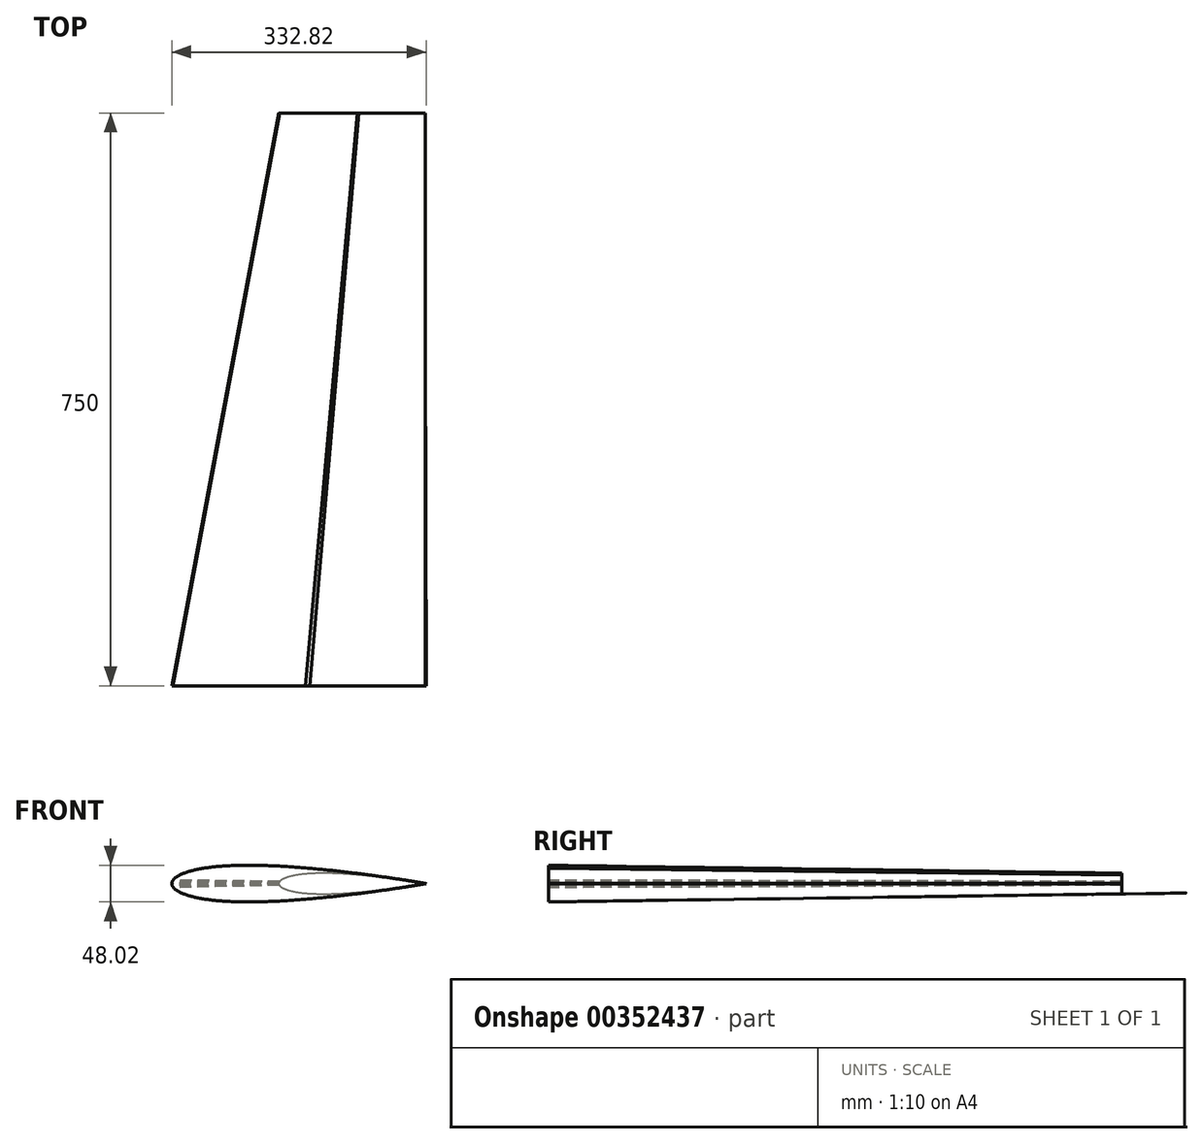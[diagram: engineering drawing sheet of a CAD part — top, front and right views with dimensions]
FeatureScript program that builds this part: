
annotation { "Feature Type Name" : "Feature", "Feature Type Description" : "" }
export const myFeature = defineFeature(function(context is Context, id is Id, definition is map)
    precondition{}
    {
        {
            var Q0;
            Q0=qCreatedBy(makeId("Front.planeOp"),FACE);
            cPlane(context, id + "F0", {"entities" : qUnion([Q0]), "cplaneType" : CPlaneType.OFFSET, "offset" : 750 * mm, "oppositeDirection" : true, "width" : 150 * mm, "height" : 150 * mm});
        }
        {
            var Q0;
            Q0=qCreatedBy(makeId("Front.planeOp"),FACE);
            var sketch = newSketch(context, id + "F1", { "sketchPlane" : qUnion([Q0])});
            skLineSegment(sketch, "E0", {"start": v(-170, 0) * mm, "end": v(170, 0) * mm, "construction": true});
            skLineSegment(sketch, "E1", {"start": v(170, 0.54) * mm, "end": v(169.98, 0.54) * mm});
            skLineSegment(sketch, "E2", {"start": v(169.98, 0.54) * mm, "end": v(169.92, 0.55) * mm});
            skLineSegment(sketch, "E3", {"start": v(169.92, 0.55) * mm, "end": v(169.8, 0.57) * mm});
            skLineSegment(sketch, "E4", {"start": v(169.8, 0.57) * mm, "end": v(169.66, 0.6) * mm});
            skLineSegment(sketch, "E5", {"start": v(169.66, 0.6) * mm, "end": v(169.47, 0.63) * mm});
            skLineSegment(sketch, "E6", {"start": v(169.47, 0.63) * mm, "end": v(169.24, 0.67) * mm});
            skLineSegment(sketch, "E7", {"start": v(169.24, 0.67) * mm, "end": v(168.96, 0.72) * mm});
            skLineSegment(sketch, "E8", {"start": v(168.96, 0.72) * mm, "end": v(168.65, 0.77) * mm});
            skLineSegment(sketch, "E9", {"start": v(168.65, 0.77) * mm, "end": v(168.29, 0.84) * mm});
            skLineSegment(sketch, "E10", {"start": v(168.29, 0.84) * mm, "end": v(167.89, 0.9) * mm});
            skLineSegment(sketch, "E11", {"start": v(167.89, 0.9) * mm, "end": v(167.44, 0.98) * mm});
            skLineSegment(sketch, "E12", {"start": v(167.44, 0.98) * mm, "end": v(166.96, 1.07) * mm});
            skLineSegment(sketch, "E13", {"start": v(166.96, 1.07) * mm, "end": v(166.43, 1.16) * mm});
            skLineSegment(sketch, "E14", {"start": v(166.43, 1.16) * mm, "end": v(165.86, 1.26) * mm});
            skLineSegment(sketch, "E15", {"start": v(165.86, 1.26) * mm, "end": v(165.26, 1.36) * mm});
            skLineSegment(sketch, "E16", {"start": v(165.26, 1.36) * mm, "end": v(164.6, 1.47) * mm});
            skLineSegment(sketch, "E17", {"start": v(164.6, 1.47) * mm, "end": v(163.91, 1.6) * mm});
            skLineSegment(sketch, "E18", {"start": v(163.91, 1.6) * mm, "end": v(163.18, 1.72) * mm});
            skLineSegment(sketch, "E19", {"start": v(163.18, 1.72) * mm, "end": v(162.4, 1.85) * mm});
            skLineSegment(sketch, "E20", {"start": v(162.4, 1.85) * mm, "end": v(161.6, 1.99) * mm});
            skLineSegment(sketch, "E21", {"start": v(161.6, 1.99) * mm, "end": v(160.74, 2.13) * mm});
            skLineSegment(sketch, "E22", {"start": v(160.74, 2.13) * mm, "end": v(159.85, 2.28) * mm});
            skLineSegment(sketch, "E23", {"start": v(159.85, 2.28) * mm, "end": v(158.92, 2.44) * mm});
            skLineSegment(sketch, "E24", {"start": v(158.92, 2.44) * mm, "end": v(157.94, 2.6) * mm});
            skLineSegment(sketch, "E25", {"start": v(157.94, 2.6) * mm, "end": v(156.93, 2.77) * mm});
            skLineSegment(sketch, "E26", {"start": v(156.93, 2.77) * mm, "end": v(155.88, 2.95) * mm});
            skLineSegment(sketch, "E27", {"start": v(155.88, 2.95) * mm, "end": v(154.79, 3.13) * mm});
            skLineSegment(sketch, "E28", {"start": v(154.79, 3.13) * mm, "end": v(153.66, 3.32) * mm});
            skLineSegment(sketch, "E29", {"start": v(153.66, 3.32) * mm, "end": v(152.5, 3.51) * mm});
            skLineSegment(sketch, "E30", {"start": v(152.5, 3.51) * mm, "end": v(151.29, 3.7) * mm});
            skLineSegment(sketch, "E31", {"start": v(151.29, 3.7) * mm, "end": v(150.05, 3.91) * mm});
            skLineSegment(sketch, "E32", {"start": v(150.05, 3.91) * mm, "end": v(148.76, 4.12) * mm});
            skLineSegment(sketch, "E33", {"start": v(148.76, 4.12) * mm, "end": v(147.45, 4.34) * mm});
            skLineSegment(sketch, "E34", {"start": v(147.45, 4.34) * mm, "end": v(146.1, 4.55) * mm});
            skLineSegment(sketch, "E35", {"start": v(146.1, 4.55) * mm, "end": v(144.7, 4.78) * mm});
            skLineSegment(sketch, "E36", {"start": v(144.7, 4.78) * mm, "end": v(143.28, 5) * mm});
            skLineSegment(sketch, "E37", {"start": v(143.28, 5) * mm, "end": v(141.81, 5.24) * mm});
            skLineSegment(sketch, "E38", {"start": v(141.81, 5.24) * mm, "end": v(140.32, 5.48) * mm});
            skLineSegment(sketch, "E39", {"start": v(140.32, 5.48) * mm, "end": v(138.78, 5.72) * mm});
            skLineSegment(sketch, "E40", {"start": v(138.78, 5.72) * mm, "end": v(137.22, 5.96) * mm});
            skLineSegment(sketch, "E41", {"start": v(137.22, 5.96) * mm, "end": v(135.62, 6.21) * mm});
            skLineSegment(sketch, "E42", {"start": v(135.62, 6.21) * mm, "end": v(133.98, 6.47) * mm});
            skLineSegment(sketch, "E43", {"start": v(133.98, 6.47) * mm, "end": v(132.31, 6.72) * mm});
            skLineSegment(sketch, "E44", {"start": v(132.31, 6.72) * mm, "end": v(130.6, 6.98) * mm});
            skLineSegment(sketch, "E45", {"start": v(130.6, 6.98) * mm, "end": v(128.88, 7.25) * mm});
            skLineSegment(sketch, "E46", {"start": v(128.88, 7.25) * mm, "end": v(127.1, 7.52) * mm});
            skLineSegment(sketch, "E47", {"start": v(127.1, 7.52) * mm, "end": v(125.31, 7.79) * mm});
            skLineSegment(sketch, "E48", {"start": v(125.31, 7.79) * mm, "end": v(123.48, 8.06) * mm});
            skLineSegment(sketch, "E49", {"start": v(123.48, 8.06) * mm, "end": v(121.62, 8.34) * mm});
            skLineSegment(sketch, "E50", {"start": v(121.62, 8.34) * mm, "end": v(119.73, 8.62) * mm});
            skLineSegment(sketch, "E51", {"start": v(119.73, 8.62) * mm, "end": v(117.81, 8.9) * mm});
            skLineSegment(sketch, "E52", {"start": v(117.81, 8.9) * mm, "end": v(115.86, 9.18) * mm});
            skLineSegment(sketch, "E53", {"start": v(115.86, 9.18) * mm, "end": v(113.89, 9.47) * mm});
            skLineSegment(sketch, "E54", {"start": v(113.89, 9.47) * mm, "end": v(111.88, 9.76) * mm});
            skLineSegment(sketch, "E55", {"start": v(111.88, 9.76) * mm, "end": v(109.84, 10.05) * mm});
            skLineSegment(sketch, "E56", {"start": v(109.84, 10.05) * mm, "end": v(107.78, 10.34) * mm});
            skLineSegment(sketch, "E57", {"start": v(107.78, 10.34) * mm, "end": v(105.7, 10.63) * mm});
            skLineSegment(sketch, "E58", {"start": v(105.7, 10.63) * mm, "end": v(103.58, 10.93) * mm});
            skLineSegment(sketch, "E59", {"start": v(103.58, 10.93) * mm, "end": v(101.44, 11.23) * mm});
            skLineSegment(sketch, "E60", {"start": v(101.44, 11.23) * mm, "end": v(99.27, 11.52) * mm});
            skLineSegment(sketch, "E61", {"start": v(99.27, 11.52) * mm, "end": v(97.08, 11.82) * mm});
            skLineSegment(sketch, "E62", {"start": v(97.08, 11.82) * mm, "end": v(94.86, 12.12) * mm});
            skLineSegment(sketch, "E63", {"start": v(94.86, 12.12) * mm, "end": v(92.63, 12.42) * mm});
            skLineSegment(sketch, "E64", {"start": v(92.63, 12.42) * mm, "end": v(90.36, 12.73) * mm});
            skLineSegment(sketch, "E65", {"start": v(90.36, 12.73) * mm, "end": v(88.08, 13.03) * mm});
            skLineSegment(sketch, "E66", {"start": v(88.08, 13.03) * mm, "end": v(85.77, 13.33) * mm});
            skLineSegment(sketch, "E67", {"start": v(85.77, 13.33) * mm, "end": v(83.45, 13.63) * mm});
            skLineSegment(sketch, "E68", {"start": v(83.45, 13.63) * mm, "end": v(81.1, 13.94) * mm});
            skLineSegment(sketch, "E69", {"start": v(81.1, 13.94) * mm, "end": v(78.73, 14.24) * mm});
            skLineSegment(sketch, "E70", {"start": v(78.73, 14.24) * mm, "end": v(76.34, 14.54) * mm});
            skLineSegment(sketch, "E71", {"start": v(76.34, 14.54) * mm, "end": v(73.93, 14.84) * mm});
            skLineSegment(sketch, "E72", {"start": v(73.93, 14.84) * mm, "end": v(71.5, 15.14) * mm});
            skLineSegment(sketch, "E73", {"start": v(71.5, 15.14) * mm, "end": v(69.06, 15.44) * mm});
            skLineSegment(sketch, "E74", {"start": v(69.06, 15.44) * mm, "end": v(66.6, 15.74) * mm});
            skLineSegment(sketch, "E75", {"start": v(66.6, 15.74) * mm, "end": v(64.13, 16.04) * mm});
            skLineSegment(sketch, "E76", {"start": v(64.13, 16.04) * mm, "end": v(61.63, 16.34) * mm});
            skLineSegment(sketch, "E77", {"start": v(61.63, 16.34) * mm, "end": v(59.12, 16.63) * mm});
            skLineSegment(sketch, "E78", {"start": v(59.12, 16.63) * mm, "end": v(56.6, 16.92) * mm});
            skLineSegment(sketch, "E79", {"start": v(56.6, 16.92) * mm, "end": v(54.06, 17.22) * mm});
            skLineSegment(sketch, "E80", {"start": v(54.06, 17.22) * mm, "end": v(51.51, 17.5) * mm});
            skLineSegment(sketch, "E81", {"start": v(51.51, 17.5) * mm, "end": v(48.95, 17.8) * mm});
            skLineSegment(sketch, "E82", {"start": v(48.95, 17.8) * mm, "end": v(46.37, 18.08) * mm});
            skLineSegment(sketch, "E83", {"start": v(46.37, 18.08) * mm, "end": v(43.78, 18.36) * mm});
            skLineSegment(sketch, "E84", {"start": v(43.78, 18.36) * mm, "end": v(41.18, 18.64) * mm});
            skLineSegment(sketch, "E85", {"start": v(41.18, 18.64) * mm, "end": v(38.58, 18.92) * mm});
            skLineSegment(sketch, "E86", {"start": v(38.58, 18.92) * mm, "end": v(35.96, 19.2) * mm});
            skLineSegment(sketch, "E87", {"start": v(35.96, 19.2) * mm, "end": v(33.33, 19.46) * mm});
            skLineSegment(sketch, "E88", {"start": v(33.33, 19.46) * mm, "end": v(30.7, 19.73) * mm});
            skLineSegment(sketch, "E89", {"start": v(30.7, 19.73) * mm, "end": v(28.05, 20) * mm});
            skLineSegment(sketch, "E90", {"start": v(28.05, 20) * mm, "end": v(25.4, 20.25) * mm});
            skLineSegment(sketch, "E91", {"start": v(25.4, 20.25) * mm, "end": v(22.74, 20.51) * mm});
            skLineSegment(sketch, "E92", {"start": v(22.74, 20.51) * mm, "end": v(20.08, 20.76) * mm});
            skLineSegment(sketch, "E93", {"start": v(20.08, 20.76) * mm, "end": v(17.41, 21) * mm});
            skLineSegment(sketch, "E94", {"start": v(17.41, 21) * mm, "end": v(14.74, 21.25) * mm});
            skLineSegment(sketch, "E95", {"start": v(14.74, 21.25) * mm, "end": v(12.07, 21.5) * mm});
            skLineSegment(sketch, "E96", {"start": v(12.07, 21.5) * mm, "end": v(9.39, 21.72) * mm});
            skLineSegment(sketch, "E97", {"start": v(9.39, 21.72) * mm, "end": v(6.7, 21.95) * mm});
            skLineSegment(sketch, "E98", {"start": v(6.7, 21.95) * mm, "end": v(4.03, 22.18) * mm});
            skLineSegment(sketch, "E99", {"start": v(4.03, 22.18) * mm, "end": v(1.34, 22.4) * mm});
            skLineSegment(sketch, "E100", {"start": v(1.34, 22.4) * mm, "end": v(-1.34, 22.6) * mm});
            skLineSegment(sketch, "E101", {"start": v(-1.34, 22.6) * mm, "end": v(-4.03, 22.81) * mm});
            skLineSegment(sketch, "E102", {"start": v(-4.03, 22.81) * mm, "end": v(-6.7, 23.01) * mm});
            skLineSegment(sketch, "E103", {"start": v(-6.7, 23.01) * mm, "end": v(-9.39, 23.2) * mm});
            skLineSegment(sketch, "E104", {"start": v(-9.39, 23.2) * mm, "end": v(-12.07, 23.4) * mm});
            skLineSegment(sketch, "E105", {"start": v(-12.07, 23.4) * mm, "end": v(-14.74, 23.57) * mm});
            skLineSegment(sketch, "E106", {"start": v(-14.74, 23.57) * mm, "end": v(-17.41, 23.74) * mm});
            skLineSegment(sketch, "E107", {"start": v(-17.41, 23.74) * mm, "end": v(-20.08, 23.91) * mm});
            skLineSegment(sketch, "E108", {"start": v(-20.08, 23.91) * mm, "end": v(-22.74, 24.07) * mm});
            skLineSegment(sketch, "E109", {"start": v(-22.74, 24.07) * mm, "end": v(-25.4, 24.22) * mm});
            skLineSegment(sketch, "E110", {"start": v(-25.4, 24.22) * mm, "end": v(-28.05, 24.37) * mm});
            skLineSegment(sketch, "E111", {"start": v(-28.05, 24.37) * mm, "end": v(-30.7, 24.5) * mm});
            skLineSegment(sketch, "E112", {"start": v(-30.7, 24.5) * mm, "end": v(-33.33, 24.63) * mm});
            skLineSegment(sketch, "E113", {"start": v(-33.33, 24.63) * mm, "end": v(-35.96, 24.75) * mm});
            skLineSegment(sketch, "E114", {"start": v(-35.96, 24.75) * mm, "end": v(-38.58, 24.86) * mm});
            skLineSegment(sketch, "E115", {"start": v(-38.58, 24.86) * mm, "end": v(-41.18, 24.97) * mm});
            skLineSegment(sketch, "E116", {"start": v(-41.18, 24.97) * mm, "end": v(-43.78, 25.06) * mm});
            skLineSegment(sketch, "E117", {"start": v(-43.78, 25.06) * mm, "end": v(-46.37, 25.15) * mm});
            skLineSegment(sketch, "E118", {"start": v(-46.37, 25.15) * mm, "end": v(-48.95, 25.23) * mm});
            skLineSegment(sketch, "E119", {"start": v(-48.95, 25.23) * mm, "end": v(-51.51, 25.3) * mm});
            skLineSegment(sketch, "E120", {"start": v(-51.51, 25.3) * mm, "end": v(-54.06, 25.35) * mm});
            skLineSegment(sketch, "E121", {"start": v(-54.06, 25.35) * mm, "end": v(-56.6, 25.4) * mm});
            skLineSegment(sketch, "E122", {"start": v(-56.6, 25.4) * mm, "end": v(-59.12, 25.44) * mm});
            skLineSegment(sketch, "E123", {"start": v(-59.12, 25.44) * mm, "end": v(-61.63, 25.47) * mm});
            skLineSegment(sketch, "E124", {"start": v(-61.63, 25.47) * mm, "end": v(-64.13, 25.5) * mm});
            skLineSegment(sketch, "E125", {"start": v(-64.13, 25.5) * mm, "end": v(-66.6, 25.5) * mm});
            skLineSegment(sketch, "E126", {"start": v(-66.6, 25.5) * mm, "end": v(-69.06, 25.5) * mm});
            skLineSegment(sketch, "E127", {"start": v(-69.06, 25.5) * mm, "end": v(-71.5, 25.5) * mm});
            skLineSegment(sketch, "E128", {"start": v(-71.5, 25.5) * mm, "end": v(-73.93, 25.48) * mm});
            skLineSegment(sketch, "E129", {"start": v(-73.93, 25.48) * mm, "end": v(-76.34, 25.45) * mm});
            skLineSegment(sketch, "E130", {"start": v(-76.34, 25.45) * mm, "end": v(-78.73, 25.4) * mm});
            skLineSegment(sketch, "E131", {"start": v(-78.73, 25.4) * mm, "end": v(-81.1, 25.36) * mm});
            skLineSegment(sketch, "E132", {"start": v(-81.1, 25.36) * mm, "end": v(-83.45, 25.3) * mm});
            skLineSegment(sketch, "E133", {"start": v(-83.45, 25.3) * mm, "end": v(-85.77, 25.23) * mm});
            skLineSegment(sketch, "E134", {"start": v(-85.77, 25.23) * mm, "end": v(-88.08, 25.14) * mm});
            skLineSegment(sketch, "E135", {"start": v(-88.08, 25.14) * mm, "end": v(-90.36, 25.05) * mm});
            skLineSegment(sketch, "E136", {"start": v(-90.36, 25.05) * mm, "end": v(-92.63, 24.95) * mm});
            skLineSegment(sketch, "E137", {"start": v(-92.63, 24.95) * mm, "end": v(-94.86, 24.83) * mm});
            skLineSegment(sketch, "E138", {"start": v(-94.86, 24.83) * mm, "end": v(-97.08, 24.7) * mm});
            skLineSegment(sketch, "E139", {"start": v(-97.08, 24.7) * mm, "end": v(-99.27, 24.57) * mm});
            skLineSegment(sketch, "E140", {"start": v(-99.27, 24.57) * mm, "end": v(-101.44, 24.42) * mm});
            skLineSegment(sketch, "E141", {"start": v(-101.44, 24.42) * mm, "end": v(-103.58, 24.27) * mm});
            skLineSegment(sketch, "E142", {"start": v(-103.58, 24.27) * mm, "end": v(-105.7, 24.1) * mm});
            skLineSegment(sketch, "E143", {"start": v(-105.7, 24.1) * mm, "end": v(-107.78, 23.92) * mm});
            skLineSegment(sketch, "E144", {"start": v(-107.78, 23.92) * mm, "end": v(-109.84, 23.73) * mm});
            skLineSegment(sketch, "E145", {"start": v(-109.84, 23.73) * mm, "end": v(-111.88, 23.53) * mm});
            skLineSegment(sketch, "E146", {"start": v(-111.88, 23.53) * mm, "end": v(-113.89, 23.32) * mm});
            skLineSegment(sketch, "E147", {"start": v(-113.89, 23.32) * mm, "end": v(-115.86, 23.1) * mm});
            skLineSegment(sketch, "E148", {"start": v(-115.86, 23.1) * mm, "end": v(-117.81, 22.87) * mm});
            skLineSegment(sketch, "E149", {"start": v(-117.81, 22.87) * mm, "end": v(-119.73, 22.62) * mm});
            skLineSegment(sketch, "E150", {"start": v(-119.73, 22.62) * mm, "end": v(-121.62, 22.37) * mm});
            skLineSegment(sketch, "E151", {"start": v(-121.62, 22.37) * mm, "end": v(-123.48, 22.1) * mm});
            skLineSegment(sketch, "E152", {"start": v(-123.48, 22.1) * mm, "end": v(-125.31, 21.83) * mm});
            skLineSegment(sketch, "E153", {"start": v(-125.31, 21.83) * mm, "end": v(-127.1, 21.55) * mm});
            skLineSegment(sketch, "E154", {"start": v(-127.1, 21.55) * mm, "end": v(-128.88, 21.26) * mm});
            skLineSegment(sketch, "E155", {"start": v(-128.88, 21.26) * mm, "end": v(-130.6, 20.95) * mm});
            skLineSegment(sketch, "E156", {"start": v(-130.6, 20.95) * mm, "end": v(-132.31, 20.64) * mm});
            skLineSegment(sketch, "E157", {"start": v(-132.31, 20.64) * mm, "end": v(-133.98, 20.32) * mm});
            skLineSegment(sketch, "E158", {"start": v(-133.98, 20.32) * mm, "end": v(-135.62, 19.98) * mm});
            skLineSegment(sketch, "E159", {"start": v(-135.62, 19.98) * mm, "end": v(-137.22, 19.64) * mm});
            skLineSegment(sketch, "E160", {"start": v(-137.22, 19.64) * mm, "end": v(-138.78, 19.29) * mm});
            skLineSegment(sketch, "E161", {"start": v(-138.78, 19.29) * mm, "end": v(-140.32, 18.93) * mm});
            skLineSegment(sketch, "E162", {"start": v(-140.32, 18.93) * mm, "end": v(-141.81, 18.56) * mm});
            skLineSegment(sketch, "E163", {"start": v(-141.81, 18.56) * mm, "end": v(-143.28, 18.18) * mm});
            skLineSegment(sketch, "E164", {"start": v(-143.28, 18.18) * mm, "end": v(-144.7, 17.8) * mm});
            skLineSegment(sketch, "E165", {"start": v(-144.7, 17.8) * mm, "end": v(-146.1, 17.4) * mm});
            skLineSegment(sketch, "E166", {"start": v(-146.1, 17.4) * mm, "end": v(-147.45, 17) * mm});
            skLineSegment(sketch, "E167", {"start": v(-147.45, 17) * mm, "end": v(-148.76, 16.58) * mm});
            skLineSegment(sketch, "E168", {"start": v(-148.76, 16.58) * mm, "end": v(-150.05, 16.16) * mm});
            skLineSegment(sketch, "E169", {"start": v(-150.05, 16.16) * mm, "end": v(-151.29, 15.73) * mm});
            skLineSegment(sketch, "E170", {"start": v(-151.29, 15.73) * mm, "end": v(-152.5, 15.3) * mm});
            skLineSegment(sketch, "E171", {"start": v(-152.5, 15.3) * mm, "end": v(-153.66, 14.85) * mm});
            skLineSegment(sketch, "E172", {"start": v(-153.66, 14.85) * mm, "end": v(-154.79, 14.4) * mm});
            skLineSegment(sketch, "E173", {"start": v(-154.79, 14.4) * mm, "end": v(-155.88, 13.95) * mm});
            skLineSegment(sketch, "E174", {"start": v(-155.88, 13.95) * mm, "end": v(-156.93, 13.48) * mm});
            skLineSegment(sketch, "E175", {"start": v(-156.93, 13.48) * mm, "end": v(-157.94, 13) * mm});
            skLineSegment(sketch, "E176", {"start": v(-157.94, 13) * mm, "end": v(-158.92, 12.53) * mm});
            skLineSegment(sketch, "E177", {"start": v(-158.92, 12.53) * mm, "end": v(-159.85, 12.04) * mm});
            skLineSegment(sketch, "E178", {"start": v(-159.85, 12.04) * mm, "end": v(-160.74, 11.55) * mm});
            skLineSegment(sketch, "E179", {"start": v(-160.74, 11.55) * mm, "end": v(-161.6, 11.05) * mm});
            skLineSegment(sketch, "E180", {"start": v(-161.6, 11.05) * mm, "end": v(-162.4, 10.55) * mm});
            skLineSegment(sketch, "E181", {"start": v(-162.4, 10.55) * mm, "end": v(-163.18, 10.04) * mm});
            skLineSegment(sketch, "E182", {"start": v(-163.18, 10.04) * mm, "end": v(-163.91, 9.53) * mm});
            skLineSegment(sketch, "E183", {"start": v(-163.91, 9.53) * mm, "end": v(-164.6, 9) * mm});
            skLineSegment(sketch, "E184", {"start": v(-164.6, 9) * mm, "end": v(-165.26, 8.48) * mm});
            skLineSegment(sketch, "E185", {"start": v(-165.26, 8.48) * mm, "end": v(-165.86, 7.95) * mm});
            skLineSegment(sketch, "E186", {"start": v(-165.86, 7.95) * mm, "end": v(-166.43, 7.4) * mm});
            skLineSegment(sketch, "E187", {"start": v(-166.43, 7.4) * mm, "end": v(-166.96, 6.87) * mm});
            skLineSegment(sketch, "E188", {"start": v(-166.96, 6.87) * mm, "end": v(-167.44, 6.32) * mm});
            skLineSegment(sketch, "E189", {"start": v(-167.44, 6.32) * mm, "end": v(-167.89, 5.77) * mm});
            skLineSegment(sketch, "E190", {"start": v(-167.89, 5.77) * mm, "end": v(-168.29, 5.2) * mm});
            skLineSegment(sketch, "E191", {"start": v(-168.29, 5.2) * mm, "end": v(-168.65, 4.65) * mm});
            skLineSegment(sketch, "E192", {"start": v(-168.65, 4.65) * mm, "end": v(-168.96, 4.08) * mm});
            skLineSegment(sketch, "E193", {"start": v(-168.96, 4.08) * mm, "end": v(-169.24, 3.51) * mm});
            skLineSegment(sketch, "E194", {"start": v(-169.24, 3.51) * mm, "end": v(-169.47, 2.94) * mm});
            skLineSegment(sketch, "E195", {"start": v(-169.47, 2.94) * mm, "end": v(-169.66, 2.36) * mm});
            skLineSegment(sketch, "E196", {"start": v(-169.66, 2.36) * mm, "end": v(-169.8, 1.77) * mm});
            skLineSegment(sketch, "E197", {"start": v(-169.8, 1.77) * mm, "end": v(-169.92, 1.19) * mm});
            skLineSegment(sketch, "E198", {"start": v(-169.92, 1.19) * mm, "end": v(-169.98, 0.6) * mm});
            skLineSegment(sketch, "E199", {"start": v(-169.98, 0.6) * mm, "end": v(-170, 0) * mm});
            skLineSegment(sketch, "E200", {"start": v(-170, 0) * mm, "end": v(-169.98, -0.6) * mm});
            skLineSegment(sketch, "E201", {"start": v(-169.98, -0.6) * mm, "end": v(-169.92, -1.19) * mm});
            skLineSegment(sketch, "E202", {"start": v(-169.92, -1.19) * mm, "end": v(-169.8, -1.77) * mm});
            skLineSegment(sketch, "E203", {"start": v(-169.8, -1.77) * mm, "end": v(-169.66, -2.36) * mm});
            skLineSegment(sketch, "E204", {"start": v(-169.66, -2.36) * mm, "end": v(-169.47, -2.94) * mm});
            skLineSegment(sketch, "E205", {"start": v(-169.47, -2.94) * mm, "end": v(-169.24, -3.51) * mm});
            skLineSegment(sketch, "E206", {"start": v(-169.24, -3.51) * mm, "end": v(-168.96, -4.08) * mm});
            skLineSegment(sketch, "E207", {"start": v(-168.96, -4.08) * mm, "end": v(-168.65, -4.65) * mm});
            skLineSegment(sketch, "E208", {"start": v(-168.65, -4.65) * mm, "end": v(-168.29, -5.2) * mm});
            skLineSegment(sketch, "E209", {"start": v(-168.29, -5.2) * mm, "end": v(-167.89, -5.77) * mm});
            skLineSegment(sketch, "E210", {"start": v(-167.89, -5.77) * mm, "end": v(-167.44, -6.32) * mm});
            skLineSegment(sketch, "E211", {"start": v(-167.44, -6.32) * mm, "end": v(-166.96, -6.87) * mm});
            skLineSegment(sketch, "E212", {"start": v(-166.96, -6.87) * mm, "end": v(-166.43, -7.4) * mm});
            skLineSegment(sketch, "E213", {"start": v(-166.43, -7.4) * mm, "end": v(-165.86, -7.95) * mm});
            skLineSegment(sketch, "E214", {"start": v(-165.86, -7.95) * mm, "end": v(-165.26, -8.48) * mm});
            skLineSegment(sketch, "E215", {"start": v(-165.26, -8.48) * mm, "end": v(-164.6, -9) * mm});
            skLineSegment(sketch, "E216", {"start": v(-164.6, -9) * mm, "end": v(-163.91, -9.53) * mm});
            skLineSegment(sketch, "E217", {"start": v(-163.91, -9.53) * mm, "end": v(-163.18, -10.04) * mm});
            skLineSegment(sketch, "E218", {"start": v(-163.18, -10.04) * mm, "end": v(-162.4, -10.55) * mm});
            skLineSegment(sketch, "E219", {"start": v(-162.4, -10.55) * mm, "end": v(-161.6, -11.05) * mm});
            skLineSegment(sketch, "E220", {"start": v(-161.6, -11.05) * mm, "end": v(-160.74, -11.55) * mm});
            skLineSegment(sketch, "E221", {"start": v(-160.74, -11.55) * mm, "end": v(-159.85, -12.04) * mm});
            skLineSegment(sketch, "E222", {"start": v(-159.85, -12.04) * mm, "end": v(-158.92, -12.53) * mm});
            skLineSegment(sketch, "E223", {"start": v(-158.92, -12.53) * mm, "end": v(-157.94, -13) * mm});
            skLineSegment(sketch, "E224", {"start": v(-157.94, -13) * mm, "end": v(-156.93, -13.48) * mm});
            skLineSegment(sketch, "E225", {"start": v(-156.93, -13.48) * mm, "end": v(-155.88, -13.95) * mm});
            skLineSegment(sketch, "E226", {"start": v(-155.88, -13.95) * mm, "end": v(-154.79, -14.4) * mm});
            skLineSegment(sketch, "E227", {"start": v(-154.79, -14.4) * mm, "end": v(-153.66, -14.85) * mm});
            skLineSegment(sketch, "E228", {"start": v(-153.66, -14.85) * mm, "end": v(-152.5, -15.3) * mm});
            skLineSegment(sketch, "E229", {"start": v(-152.5, -15.3) * mm, "end": v(-151.29, -15.73) * mm});
            skLineSegment(sketch, "E230", {"start": v(-151.29, -15.73) * mm, "end": v(-150.05, -16.16) * mm});
            skLineSegment(sketch, "E231", {"start": v(-150.05, -16.16) * mm, "end": v(-148.76, -16.58) * mm});
            skLineSegment(sketch, "E232", {"start": v(-148.76, -16.58) * mm, "end": v(-147.45, -17) * mm});
            skLineSegment(sketch, "E233", {"start": v(-147.45, -17) * mm, "end": v(-146.1, -17.4) * mm});
            skLineSegment(sketch, "E234", {"start": v(-146.1, -17.4) * mm, "end": v(-144.7, -17.8) * mm});
            skLineSegment(sketch, "E235", {"start": v(-144.7, -17.8) * mm, "end": v(-143.28, -18.18) * mm});
            skLineSegment(sketch, "E236", {"start": v(-143.28, -18.18) * mm, "end": v(-141.81, -18.56) * mm});
            skLineSegment(sketch, "E237", {"start": v(-141.81, -18.56) * mm, "end": v(-140.32, -18.93) * mm});
            skLineSegment(sketch, "E238", {"start": v(-140.32, -18.93) * mm, "end": v(-138.78, -19.29) * mm});
            skLineSegment(sketch, "E239", {"start": v(-138.78, -19.29) * mm, "end": v(-137.22, -19.64) * mm});
            skLineSegment(sketch, "E240", {"start": v(-137.22, -19.64) * mm, "end": v(-135.62, -19.98) * mm});
            skLineSegment(sketch, "E241", {"start": v(-135.62, -19.98) * mm, "end": v(-133.98, -20.32) * mm});
            skLineSegment(sketch, "E242", {"start": v(-133.98, -20.32) * mm, "end": v(-132.31, -20.64) * mm});
            skLineSegment(sketch, "E243", {"start": v(-132.31, -20.64) * mm, "end": v(-130.6, -20.95) * mm});
            skLineSegment(sketch, "E244", {"start": v(-130.6, -20.95) * mm, "end": v(-128.88, -21.26) * mm});
            skLineSegment(sketch, "E245", {"start": v(-128.88, -21.26) * mm, "end": v(-127.1, -21.55) * mm});
            skLineSegment(sketch, "E246", {"start": v(-127.1, -21.55) * mm, "end": v(-125.31, -21.83) * mm});
            skLineSegment(sketch, "E247", {"start": v(-125.31, -21.83) * mm, "end": v(-123.48, -22.1) * mm});
            skLineSegment(sketch, "E248", {"start": v(-123.48, -22.1) * mm, "end": v(-121.62, -22.37) * mm});
            skLineSegment(sketch, "E249", {"start": v(-121.62, -22.37) * mm, "end": v(-119.73, -22.62) * mm});
            skLineSegment(sketch, "E250", {"start": v(-119.73, -22.62) * mm, "end": v(-117.81, -22.87) * mm});
            skLineSegment(sketch, "E251", {"start": v(-117.81, -22.87) * mm, "end": v(-115.86, -23.1) * mm});
            skLineSegment(sketch, "E252", {"start": v(-115.86, -23.1) * mm, "end": v(-113.89, -23.32) * mm});
            skLineSegment(sketch, "E253", {"start": v(-113.89, -23.32) * mm, "end": v(-111.88, -23.53) * mm});
            skLineSegment(sketch, "E254", {"start": v(-111.88, -23.53) * mm, "end": v(-109.84, -23.73) * mm});
            skLineSegment(sketch, "E255", {"start": v(-109.84, -23.73) * mm, "end": v(-107.78, -23.92) * mm});
            skLineSegment(sketch, "E256", {"start": v(-107.78, -23.92) * mm, "end": v(-105.7, -24.1) * mm});
            skLineSegment(sketch, "E257", {"start": v(-105.7, -24.1) * mm, "end": v(-103.58, -24.27) * mm});
            skLineSegment(sketch, "E258", {"start": v(-103.58, -24.27) * mm, "end": v(-101.44, -24.42) * mm});
            skLineSegment(sketch, "E259", {"start": v(-101.44, -24.42) * mm, "end": v(-99.27, -24.57) * mm});
            skLineSegment(sketch, "E260", {"start": v(-99.27, -24.57) * mm, "end": v(-97.08, -24.7) * mm});
            skLineSegment(sketch, "E261", {"start": v(-97.08, -24.7) * mm, "end": v(-94.86, -24.83) * mm});
            skLineSegment(sketch, "E262", {"start": v(-94.86, -24.83) * mm, "end": v(-92.63, -24.95) * mm});
            skLineSegment(sketch, "E263", {"start": v(-92.63, -24.95) * mm, "end": v(-90.36, -25.05) * mm});
            skLineSegment(sketch, "E264", {"start": v(-90.36, -25.05) * mm, "end": v(-88.08, -25.14) * mm});
            skLineSegment(sketch, "E265", {"start": v(-88.08, -25.14) * mm, "end": v(-85.77, -25.23) * mm});
            skLineSegment(sketch, "E266", {"start": v(-85.77, -25.23) * mm, "end": v(-83.45, -25.3) * mm});
            skLineSegment(sketch, "E267", {"start": v(-83.45, -25.3) * mm, "end": v(-81.1, -25.36) * mm});
            skLineSegment(sketch, "E268", {"start": v(-81.1, -25.36) * mm, "end": v(-78.73, -25.4) * mm});
            skLineSegment(sketch, "E269", {"start": v(-78.73, -25.4) * mm, "end": v(-76.34, -25.45) * mm});
            skLineSegment(sketch, "E270", {"start": v(-76.34, -25.45) * mm, "end": v(-73.93, -25.48) * mm});
            skLineSegment(sketch, "E271", {"start": v(-73.93, -25.48) * mm, "end": v(-71.5, -25.5) * mm});
            skLineSegment(sketch, "E272", {"start": v(-71.5, -25.5) * mm, "end": v(-69.06, -25.5) * mm});
            skLineSegment(sketch, "E273", {"start": v(-69.06, -25.5) * mm, "end": v(-66.6, -25.5) * mm});
            skLineSegment(sketch, "E274", {"start": v(-66.6, -25.5) * mm, "end": v(-64.13, -25.5) * mm});
            skLineSegment(sketch, "E275", {"start": v(-64.13, -25.5) * mm, "end": v(-61.63, -25.47) * mm});
            skLineSegment(sketch, "E276", {"start": v(-61.63, -25.47) * mm, "end": v(-59.12, -25.44) * mm});
            skLineSegment(sketch, "E277", {"start": v(-59.12, -25.44) * mm, "end": v(-56.6, -25.4) * mm});
            skLineSegment(sketch, "E278", {"start": v(-56.6, -25.4) * mm, "end": v(-54.06, -25.35) * mm});
            skLineSegment(sketch, "E279", {"start": v(-54.06, -25.35) * mm, "end": v(-51.51, -25.3) * mm});
            skLineSegment(sketch, "E280", {"start": v(-51.51, -25.3) * mm, "end": v(-48.95, -25.23) * mm});
            skLineSegment(sketch, "E281", {"start": v(-48.95, -25.23) * mm, "end": v(-46.37, -25.15) * mm});
            skLineSegment(sketch, "E282", {"start": v(-46.37, -25.15) * mm, "end": v(-43.78, -25.06) * mm});
            skLineSegment(sketch, "E283", {"start": v(-43.78, -25.06) * mm, "end": v(-41.18, -24.97) * mm});
            skLineSegment(sketch, "E284", {"start": v(-41.18, -24.97) * mm, "end": v(-38.58, -24.86) * mm});
            skLineSegment(sketch, "E285", {"start": v(-38.58, -24.86) * mm, "end": v(-35.96, -24.75) * mm});
            skLineSegment(sketch, "E286", {"start": v(-35.96, -24.75) * mm, "end": v(-33.33, -24.63) * mm});
            skLineSegment(sketch, "E287", {"start": v(-33.33, -24.63) * mm, "end": v(-30.7, -24.5) * mm});
            skLineSegment(sketch, "E288", {"start": v(-30.7, -24.5) * mm, "end": v(-28.05, -24.37) * mm});
            skLineSegment(sketch, "E289", {"start": v(-28.05, -24.37) * mm, "end": v(-25.4, -24.22) * mm});
            skLineSegment(sketch, "E290", {"start": v(-25.4, -24.22) * mm, "end": v(-22.74, -24.07) * mm});
            skLineSegment(sketch, "E291", {"start": v(-22.74, -24.07) * mm, "end": v(-20.08, -23.91) * mm});
            skLineSegment(sketch, "E292", {"start": v(-20.08, -23.91) * mm, "end": v(-17.41, -23.74) * mm});
            skLineSegment(sketch, "E293", {"start": v(-17.41, -23.74) * mm, "end": v(-14.74, -23.57) * mm});
            skLineSegment(sketch, "E294", {"start": v(-14.74, -23.57) * mm, "end": v(-12.07, -23.4) * mm});
            skLineSegment(sketch, "E295", {"start": v(-12.07, -23.4) * mm, "end": v(-9.39, -23.2) * mm});
            skLineSegment(sketch, "E296", {"start": v(-9.39, -23.2) * mm, "end": v(-6.7, -23.01) * mm});
            skLineSegment(sketch, "E297", {"start": v(-6.7, -23.01) * mm, "end": v(-4.03, -22.81) * mm});
            skLineSegment(sketch, "E298", {"start": v(-4.03, -22.81) * mm, "end": v(-1.34, -22.6) * mm});
            skLineSegment(sketch, "E299", {"start": v(-1.34, -22.6) * mm, "end": v(1.34, -22.4) * mm});
            skLineSegment(sketch, "E300", {"start": v(1.34, -22.4) * mm, "end": v(4.03, -22.18) * mm});
            skLineSegment(sketch, "E301", {"start": v(4.03, -22.18) * mm, "end": v(6.7, -21.95) * mm});
            skLineSegment(sketch, "E302", {"start": v(6.7, -21.95) * mm, "end": v(9.39, -21.72) * mm});
            skLineSegment(sketch, "E303", {"start": v(9.39, -21.72) * mm, "end": v(12.07, -21.5) * mm});
            skLineSegment(sketch, "E304", {"start": v(12.07, -21.5) * mm, "end": v(14.74, -21.25) * mm});
            skLineSegment(sketch, "E305", {"start": v(14.74, -21.25) * mm, "end": v(17.41, -21) * mm});
            skLineSegment(sketch, "E306", {"start": v(17.41, -21) * mm, "end": v(20.08, -20.76) * mm});
            skLineSegment(sketch, "E307", {"start": v(20.08, -20.76) * mm, "end": v(22.74, -20.51) * mm});
            skLineSegment(sketch, "E308", {"start": v(22.74, -20.51) * mm, "end": v(25.4, -20.25) * mm});
            skLineSegment(sketch, "E309", {"start": v(25.4, -20.25) * mm, "end": v(28.05, -20) * mm});
            skLineSegment(sketch, "E310", {"start": v(28.05, -20) * mm, "end": v(30.7, -19.73) * mm});
            skLineSegment(sketch, "E311", {"start": v(30.7, -19.73) * mm, "end": v(33.33, -19.46) * mm});
            skLineSegment(sketch, "E312", {"start": v(33.33, -19.46) * mm, "end": v(35.96, -19.2) * mm});
            skLineSegment(sketch, "E313", {"start": v(35.96, -19.2) * mm, "end": v(38.58, -18.92) * mm});
            skLineSegment(sketch, "E314", {"start": v(38.58, -18.92) * mm, "end": v(41.18, -18.64) * mm});
            skLineSegment(sketch, "E315", {"start": v(41.18, -18.64) * mm, "end": v(43.78, -18.36) * mm});
            skLineSegment(sketch, "E316", {"start": v(43.78, -18.36) * mm, "end": v(46.37, -18.08) * mm});
            skLineSegment(sketch, "E317", {"start": v(46.37, -18.08) * mm, "end": v(48.95, -17.8) * mm});
            skLineSegment(sketch, "E318", {"start": v(48.95, -17.8) * mm, "end": v(51.51, -17.5) * mm});
            skLineSegment(sketch, "E319", {"start": v(51.51, -17.5) * mm, "end": v(54.06, -17.22) * mm});
            skLineSegment(sketch, "E320", {"start": v(54.06, -17.22) * mm, "end": v(56.6, -16.92) * mm});
            skLineSegment(sketch, "E321", {"start": v(56.6, -16.92) * mm, "end": v(59.12, -16.63) * mm});
            skLineSegment(sketch, "E322", {"start": v(59.12, -16.63) * mm, "end": v(61.63, -16.34) * mm});
            skLineSegment(sketch, "E323", {"start": v(61.63, -16.34) * mm, "end": v(64.13, -16.04) * mm});
            skLineSegment(sketch, "E324", {"start": v(64.13, -16.04) * mm, "end": v(66.6, -15.74) * mm});
            skLineSegment(sketch, "E325", {"start": v(66.6, -15.74) * mm, "end": v(69.06, -15.44) * mm});
            skLineSegment(sketch, "E326", {"start": v(69.06, -15.44) * mm, "end": v(71.5, -15.14) * mm});
            skLineSegment(sketch, "E327", {"start": v(71.5, -15.14) * mm, "end": v(73.93, -14.84) * mm});
            skLineSegment(sketch, "E328", {"start": v(73.93, -14.84) * mm, "end": v(76.34, -14.54) * mm});
            skLineSegment(sketch, "E329", {"start": v(76.34, -14.54) * mm, "end": v(78.73, -14.24) * mm});
            skLineSegment(sketch, "E330", {"start": v(78.73, -14.24) * mm, "end": v(81.1, -13.94) * mm});
            skLineSegment(sketch, "E331", {"start": v(81.1, -13.94) * mm, "end": v(83.45, -13.63) * mm});
            skLineSegment(sketch, "E332", {"start": v(83.45, -13.63) * mm, "end": v(85.77, -13.33) * mm});
            skLineSegment(sketch, "E333", {"start": v(85.77, -13.33) * mm, "end": v(88.08, -13.03) * mm});
            skLineSegment(sketch, "E334", {"start": v(88.08, -13.03) * mm, "end": v(90.36, -12.73) * mm});
            skLineSegment(sketch, "E335", {"start": v(90.36, -12.73) * mm, "end": v(92.63, -12.42) * mm});
            skLineSegment(sketch, "E336", {"start": v(92.63, -12.42) * mm, "end": v(94.86, -12.12) * mm});
            skLineSegment(sketch, "E337", {"start": v(94.86, -12.12) * mm, "end": v(97.08, -11.82) * mm});
            skLineSegment(sketch, "E338", {"start": v(97.08, -11.82) * mm, "end": v(99.27, -11.52) * mm});
            skLineSegment(sketch, "E339", {"start": v(99.27, -11.52) * mm, "end": v(101.44, -11.23) * mm});
            skLineSegment(sketch, "E340", {"start": v(101.44, -11.23) * mm, "end": v(103.58, -10.93) * mm});
            skLineSegment(sketch, "E341", {"start": v(103.58, -10.93) * mm, "end": v(105.7, -10.63) * mm});
            skLineSegment(sketch, "E342", {"start": v(105.7, -10.63) * mm, "end": v(107.78, -10.34) * mm});
            skLineSegment(sketch, "E343", {"start": v(107.78, -10.34) * mm, "end": v(109.84, -10.05) * mm});
            skLineSegment(sketch, "E344", {"start": v(109.84, -10.05) * mm, "end": v(111.88, -9.76) * mm});
            skLineSegment(sketch, "E345", {"start": v(111.88, -9.76) * mm, "end": v(113.89, -9.47) * mm});
            skLineSegment(sketch, "E346", {"start": v(113.89, -9.47) * mm, "end": v(115.86, -9.18) * mm});
            skLineSegment(sketch, "E347", {"start": v(115.86, -9.18) * mm, "end": v(117.81, -8.9) * mm});
            skLineSegment(sketch, "E348", {"start": v(117.81, -8.9) * mm, "end": v(119.73, -8.62) * mm});
            skLineSegment(sketch, "E349", {"start": v(119.73, -8.62) * mm, "end": v(121.62, -8.34) * mm});
            skLineSegment(sketch, "E350", {"start": v(121.62, -8.34) * mm, "end": v(123.48, -8.06) * mm});
            skLineSegment(sketch, "E351", {"start": v(123.48, -8.06) * mm, "end": v(125.31, -7.79) * mm});
            skLineSegment(sketch, "E352", {"start": v(125.31, -7.79) * mm, "end": v(127.1, -7.52) * mm});
            skLineSegment(sketch, "E353", {"start": v(127.1, -7.52) * mm, "end": v(128.88, -7.25) * mm});
            skLineSegment(sketch, "E354", {"start": v(128.88, -7.25) * mm, "end": v(130.6, -6.98) * mm});
            skLineSegment(sketch, "E355", {"start": v(130.6, -6.98) * mm, "end": v(132.31, -6.72) * mm});
            skLineSegment(sketch, "E356", {"start": v(132.31, -6.72) * mm, "end": v(133.98, -6.47) * mm});
            skLineSegment(sketch, "E357", {"start": v(133.98, -6.47) * mm, "end": v(135.62, -6.21) * mm});
            skLineSegment(sketch, "E358", {"start": v(135.62, -6.21) * mm, "end": v(137.22, -5.96) * mm});
            skLineSegment(sketch, "E359", {"start": v(137.22, -5.96) * mm, "end": v(138.78, -5.72) * mm});
            skLineSegment(sketch, "E360", {"start": v(138.78, -5.72) * mm, "end": v(140.32, -5.48) * mm});
            skLineSegment(sketch, "E361", {"start": v(140.32, -5.48) * mm, "end": v(141.81, -5.24) * mm});
            skLineSegment(sketch, "E362", {"start": v(141.81, -5.24) * mm, "end": v(143.28, -5) * mm});
            skLineSegment(sketch, "E363", {"start": v(143.28, -5) * mm, "end": v(144.7, -4.78) * mm});
            skLineSegment(sketch, "E364", {"start": v(144.7, -4.78) * mm, "end": v(146.1, -4.55) * mm});
            skLineSegment(sketch, "E365", {"start": v(146.1, -4.55) * mm, "end": v(147.45, -4.34) * mm});
            skLineSegment(sketch, "E366", {"start": v(147.45, -4.34) * mm, "end": v(148.76, -4.12) * mm});
            skLineSegment(sketch, "E367", {"start": v(148.76, -4.12) * mm, "end": v(150.05, -3.91) * mm});
            skLineSegment(sketch, "E368", {"start": v(150.05, -3.91) * mm, "end": v(151.29, -3.7) * mm});
            skLineSegment(sketch, "E369", {"start": v(151.29, -3.7) * mm, "end": v(152.5, -3.51) * mm});
            skLineSegment(sketch, "E370", {"start": v(152.5, -3.51) * mm, "end": v(153.66, -3.32) * mm});
            skLineSegment(sketch, "E371", {"start": v(153.66, -3.32) * mm, "end": v(154.79, -3.13) * mm});
            skLineSegment(sketch, "E372", {"start": v(154.79, -3.13) * mm, "end": v(155.88, -2.95) * mm});
            skLineSegment(sketch, "E373", {"start": v(155.88, -2.95) * mm, "end": v(156.93, -2.77) * mm});
            skLineSegment(sketch, "E374", {"start": v(156.93, -2.77) * mm, "end": v(157.94, -2.6) * mm});
            skLineSegment(sketch, "E375", {"start": v(157.94, -2.6) * mm, "end": v(158.92, -2.44) * mm});
            skLineSegment(sketch, "E376", {"start": v(158.92, -2.44) * mm, "end": v(159.85, -2.28) * mm});
            skLineSegment(sketch, "E377", {"start": v(159.85, -2.28) * mm, "end": v(160.74, -2.13) * mm});
            skLineSegment(sketch, "E378", {"start": v(160.74, -2.13) * mm, "end": v(161.6, -1.99) * mm});
            skLineSegment(sketch, "E379", {"start": v(161.6, -1.99) * mm, "end": v(162.4, -1.85) * mm});
            skLineSegment(sketch, "E380", {"start": v(162.4, -1.85) * mm, "end": v(163.18, -1.72) * mm});
            skLineSegment(sketch, "E381", {"start": v(163.18, -1.72) * mm, "end": v(163.91, -1.6) * mm});
            skLineSegment(sketch, "E382", {"start": v(163.91, -1.6) * mm, "end": v(164.6, -1.47) * mm});
            skLineSegment(sketch, "E383", {"start": v(164.6, -1.47) * mm, "end": v(165.26, -1.36) * mm});
            skLineSegment(sketch, "E384", {"start": v(165.26, -1.36) * mm, "end": v(165.86, -1.26) * mm});
            skLineSegment(sketch, "E385", {"start": v(165.86, -1.26) * mm, "end": v(166.43, -1.16) * mm});
            skLineSegment(sketch, "E386", {"start": v(166.43, -1.16) * mm, "end": v(166.96, -1.07) * mm});
            skLineSegment(sketch, "E387", {"start": v(166.96, -1.07) * mm, "end": v(167.44, -0.98) * mm});
            skLineSegment(sketch, "E388", {"start": v(167.44, -0.98) * mm, "end": v(167.89, -0.9) * mm});
            skLineSegment(sketch, "E389", {"start": v(167.89, -0.9) * mm, "end": v(168.29, -0.84) * mm});
            skLineSegment(sketch, "E390", {"start": v(168.29, -0.84) * mm, "end": v(168.65, -0.77) * mm});
            skLineSegment(sketch, "E391", {"start": v(168.65, -0.77) * mm, "end": v(168.96, -0.72) * mm});
            skLineSegment(sketch, "E392", {"start": v(168.96, -0.72) * mm, "end": v(169.24, -0.67) * mm});
            skLineSegment(sketch, "E393", {"start": v(169.24, -0.67) * mm, "end": v(169.47, -0.63) * mm});
            skLineSegment(sketch, "E394", {"start": v(169.47, -0.63) * mm, "end": v(169.66, -0.6) * mm});
            skLineSegment(sketch, "E395", {"start": v(169.66, -0.6) * mm, "end": v(169.8, -0.57) * mm});
            skLineSegment(sketch, "E396", {"start": v(169.8, -0.57) * mm, "end": v(169.92, -0.55) * mm});
            skLineSegment(sketch, "E397", {"start": v(169.92, -0.55) * mm, "end": v(169.98, -0.54) * mm});
            skLineSegment(sketch, "E398", {"start": v(169.98, -0.54) * mm, "end": v(170, -0.54) * mm});
            skLineSegment(sketch, "E399", {"start": v(170, -0.54) * mm, "end": v(170, 0.54) * mm});
            skLineSegment(sketch, "E400", {"start": v(164.32, 0) * mm, "end": v(163.66, 0.11) * mm});
            skLineSegment(sketch, "E401", {"start": v(163.66, 0.11) * mm, "end": v(162.93, 0.24) * mm});
            skLineSegment(sketch, "E402", {"start": v(162.93, 0.24) * mm, "end": v(162.16, 0.37) * mm});
            skLineSegment(sketch, "E403", {"start": v(162.16, 0.37) * mm, "end": v(161.34, 0.5) * mm});
            skLineSegment(sketch, "E404", {"start": v(161.34, 0.5) * mm, "end": v(160.5, 0.65) * mm});
            skLineSegment(sketch, "E405", {"start": v(160.5, 0.65) * mm, "end": v(159.6, 0.8) * mm});
            skLineSegment(sketch, "E406", {"start": v(159.6, 0.8) * mm, "end": v(158.67, 0.96) * mm});
            skLineSegment(sketch, "E407", {"start": v(158.67, 0.96) * mm, "end": v(157.7, 1.13) * mm});
            skLineSegment(sketch, "E408", {"start": v(157.7, 1.13) * mm, "end": v(156.68, 1.3) * mm});
            skLineSegment(sketch, "E409", {"start": v(156.68, 1.3) * mm, "end": v(155.63, 1.47) * mm});
            skLineSegment(sketch, "E410", {"start": v(155.63, 1.47) * mm, "end": v(154.54, 1.65) * mm});
            skLineSegment(sketch, "E411", {"start": v(154.54, 1.65) * mm, "end": v(153.42, 1.84) * mm});
            skLineSegment(sketch, "E412", {"start": v(153.42, 1.84) * mm, "end": v(152.25, 2.03) * mm});
            skLineSegment(sketch, "E413", {"start": v(152.25, 2.03) * mm, "end": v(151.04, 2.23) * mm});
            skLineSegment(sketch, "E414", {"start": v(151.04, 2.23) * mm, "end": v(149.8, 2.43) * mm});
            skLineSegment(sketch, "E415", {"start": v(149.8, 2.43) * mm, "end": v(148.52, 2.64) * mm});
            skLineSegment(sketch, "E416", {"start": v(148.52, 2.64) * mm, "end": v(147.2, 2.85) * mm});
            skLineSegment(sketch, "E417", {"start": v(147.2, 2.85) * mm, "end": v(145.85, 3.07) * mm});
            skLineSegment(sketch, "E418", {"start": v(145.85, 3.07) * mm, "end": v(144.47, 3.3) * mm});
            skLineSegment(sketch, "E419", {"start": v(144.47, 3.3) * mm, "end": v(143.04, 3.52) * mm});
            skLineSegment(sketch, "E420", {"start": v(143.04, 3.52) * mm, "end": v(141.58, 3.76) * mm});
            skLineSegment(sketch, "E421", {"start": v(141.58, 3.76) * mm, "end": v(140.08, 4) * mm});
            skLineSegment(sketch, "E422", {"start": v(140.08, 4) * mm, "end": v(138.55, 4.24) * mm});
            skLineSegment(sketch, "E423", {"start": v(138.55, 4.24) * mm, "end": v(136.99, 4.48) * mm});
            skLineSegment(sketch, "E424", {"start": v(136.99, 4.48) * mm, "end": v(135.39, 4.73) * mm});
            skLineSegment(sketch, "E425", {"start": v(135.39, 4.73) * mm, "end": v(133.75, 4.98) * mm});
            skLineSegment(sketch, "E426", {"start": v(133.75, 4.98) * mm, "end": v(132.08, 5.24) * mm});
            skLineSegment(sketch, "E427", {"start": v(132.08, 5.24) * mm, "end": v(130.38, 5.5) * mm});
            skLineSegment(sketch, "E428", {"start": v(130.38, 5.5) * mm, "end": v(128.65, 5.77) * mm});
            skLineSegment(sketch, "E429", {"start": v(128.65, 5.77) * mm, "end": v(126.89, 6.03) * mm});
            skLineSegment(sketch, "E430", {"start": v(126.89, 6.03) * mm, "end": v(125.09, 6.3) * mm});
            skLineSegment(sketch, "E431", {"start": v(125.09, 6.3) * mm, "end": v(123.26, 6.58) * mm});
            skLineSegment(sketch, "E432", {"start": v(123.26, 6.58) * mm, "end": v(121.4, 6.85) * mm});
            skLineSegment(sketch, "E433", {"start": v(121.4, 6.85) * mm, "end": v(119.51, 7.13) * mm});
            skLineSegment(sketch, "E434", {"start": v(119.51, 7.13) * mm, "end": v(117.6, 7.41) * mm});
            skLineSegment(sketch, "E435", {"start": v(117.6, 7.41) * mm, "end": v(115.65, 7.7) * mm});
            skLineSegment(sketch, "E436", {"start": v(115.65, 7.7) * mm, "end": v(113.67, 7.98) * mm});
            skLineSegment(sketch, "E437", {"start": v(113.67, 7.98) * mm, "end": v(111.67, 8.27) * mm});
            skLineSegment(sketch, "E438", {"start": v(111.67, 8.27) * mm, "end": v(109.63, 8.56) * mm});
            skLineSegment(sketch, "E439", {"start": v(109.63, 8.56) * mm, "end": v(107.57, 8.85) * mm});
            skLineSegment(sketch, "E440", {"start": v(107.57, 8.85) * mm, "end": v(105.48, 9.15) * mm});
            skLineSegment(sketch, "E441", {"start": v(105.48, 9.15) * mm, "end": v(103.37, 9.44) * mm});
            skLineSegment(sketch, "E442", {"start": v(103.37, 9.44) * mm, "end": v(101.23, 9.74) * mm});
            skLineSegment(sketch, "E443", {"start": v(101.23, 9.74) * mm, "end": v(99.07, 10.04) * mm});
            skLineSegment(sketch, "E444", {"start": v(99.07, 10.04) * mm, "end": v(96.88, 10.34) * mm});
            skLineSegment(sketch, "E445", {"start": v(96.88, 10.34) * mm, "end": v(94.66, 10.64) * mm});
            skLineSegment(sketch, "E446", {"start": v(94.66, 10.64) * mm, "end": v(92.43, 10.94) * mm});
            skLineSegment(sketch, "E447", {"start": v(92.43, 10.94) * mm, "end": v(90.17, 11.24) * mm});
            skLineSegment(sketch, "E448", {"start": v(90.17, 11.24) * mm, "end": v(87.88, 11.54) * mm});
            skLineSegment(sketch, "E449", {"start": v(87.88, 11.54) * mm, "end": v(85.58, 11.84) * mm});
            skLineSegment(sketch, "E450", {"start": v(85.58, 11.84) * mm, "end": v(83.25, 12.15) * mm});
            skLineSegment(sketch, "E451", {"start": v(83.25, 12.15) * mm, "end": v(80.9, 12.45) * mm});
            skLineSegment(sketch, "E452", {"start": v(80.9, 12.45) * mm, "end": v(78.54, 12.75) * mm});
            skLineSegment(sketch, "E453", {"start": v(78.54, 12.75) * mm, "end": v(76.15, 13.05) * mm});
            skLineSegment(sketch, "E454", {"start": v(76.15, 13.05) * mm, "end": v(73.75, 13.35) * mm});
            skLineSegment(sketch, "E455", {"start": v(73.75, 13.35) * mm, "end": v(71.32, 13.65) * mm});
            skLineSegment(sketch, "E456", {"start": v(71.32, 13.65) * mm, "end": v(68.88, 13.95) * mm});
            skLineSegment(sketch, "E457", {"start": v(68.88, 13.95) * mm, "end": v(66.42, 14.25) * mm});
            skLineSegment(sketch, "E458", {"start": v(66.42, 14.25) * mm, "end": v(63.95, 14.55) * mm});
            skLineSegment(sketch, "E459", {"start": v(63.95, 14.55) * mm, "end": v(61.46, 14.85) * mm});
            skLineSegment(sketch, "E460", {"start": v(61.46, 14.85) * mm, "end": v(58.95, 15.14) * mm});
            skLineSegment(sketch, "E461", {"start": v(58.95, 15.14) * mm, "end": v(56.43, 15.43) * mm});
            skLineSegment(sketch, "E462", {"start": v(56.43, 15.43) * mm, "end": v(53.9, 15.73) * mm});
            skLineSegment(sketch, "E463", {"start": v(53.9, 15.73) * mm, "end": v(51.34, 16.02) * mm});
            skLineSegment(sketch, "E464", {"start": v(51.34, 16.02) * mm, "end": v(48.78, 16.3) * mm});
            skLineSegment(sketch, "E465", {"start": v(48.78, 16.3) * mm, "end": v(46.2, 16.59) * mm});
            skLineSegment(sketch, "E466", {"start": v(46.2, 16.59) * mm, "end": v(43.62, 16.87) * mm});
            skLineSegment(sketch, "E467", {"start": v(43.62, 16.87) * mm, "end": v(41.03, 17.15) * mm});
            skLineSegment(sketch, "E468", {"start": v(41.03, 17.15) * mm, "end": v(38.42, 17.43) * mm});
            skLineSegment(sketch, "E469", {"start": v(38.42, 17.43) * mm, "end": v(35.8, 17.7) * mm});
            skLineSegment(sketch, "E470", {"start": v(35.8, 17.7) * mm, "end": v(33.18, 17.97) * mm});
            skLineSegment(sketch, "E471", {"start": v(33.18, 17.97) * mm, "end": v(30.54, 18.24) * mm});
            skLineSegment(sketch, "E472", {"start": v(30.54, 18.24) * mm, "end": v(27.9, 18.5) * mm});
            skLineSegment(sketch, "E473", {"start": v(27.9, 18.5) * mm, "end": v(25.26, 18.76) * mm});
            skLineSegment(sketch, "E474", {"start": v(25.26, 18.76) * mm, "end": v(22.6, 19.02) * mm});
            skLineSegment(sketch, "E475", {"start": v(22.6, 19.02) * mm, "end": v(19.94, 19.27) * mm});
            skLineSegment(sketch, "E476", {"start": v(19.94, 19.27) * mm, "end": v(17.28, 19.52) * mm});
            skLineSegment(sketch, "E477", {"start": v(17.28, 19.52) * mm, "end": v(14.6, 19.76) * mm});
            skLineSegment(sketch, "E478", {"start": v(14.6, 19.76) * mm, "end": v(11.94, 20) * mm});
            skLineSegment(sketch, "E479", {"start": v(11.94, 20) * mm, "end": v(9.26, 20.23) * mm});
            skLineSegment(sketch, "E480", {"start": v(9.26, 20.23) * mm, "end": v(6.58, 20.46) * mm});
            skLineSegment(sketch, "E481", {"start": v(6.58, 20.46) * mm, "end": v(3.9, 20.68) * mm});
            skLineSegment(sketch, "E482", {"start": v(3.9, 20.68) * mm, "end": v(1.22, 20.9) * mm});
            skLineSegment(sketch, "E483", {"start": v(1.22, 20.9) * mm, "end": v(-1.46, 21.1) * mm});
            skLineSegment(sketch, "E484", {"start": v(-1.46, 21.1) * mm, "end": v(-4.14, 21.31) * mm});
            skLineSegment(sketch, "E485", {"start": v(-4.14, 21.31) * mm, "end": v(-6.82, 21.51) * mm});
            skLineSegment(sketch, "E486", {"start": v(-6.82, 21.51) * mm, "end": v(-9.5, 21.7) * mm});
            skLineSegment(sketch, "E487", {"start": v(-9.5, 21.7) * mm, "end": v(-12.17, 21.9) * mm});
            skLineSegment(sketch, "E488", {"start": v(-12.17, 21.9) * mm, "end": v(-14.84, 22.07) * mm});
            skLineSegment(sketch, "E489", {"start": v(-14.84, 22.07) * mm, "end": v(-17.5, 22.25) * mm});
            skLineSegment(sketch, "E490", {"start": v(-17.5, 22.25) * mm, "end": v(-20.17, 22.41) * mm});
            skLineSegment(sketch, "E491", {"start": v(-20.17, 22.41) * mm, "end": v(-22.83, 22.57) * mm});
            skLineSegment(sketch, "E492", {"start": v(-22.83, 22.57) * mm, "end": v(-25.48, 22.72) * mm});
            skLineSegment(sketch, "E493", {"start": v(-25.48, 22.72) * mm, "end": v(-28.13, 22.87) * mm});
            skLineSegment(sketch, "E494", {"start": v(-28.13, 22.87) * mm, "end": v(-30.77, 23) * mm});
            skLineSegment(sketch, "E495", {"start": v(-30.77, 23) * mm, "end": v(-33.4, 23.13) * mm});
            skLineSegment(sketch, "E496", {"start": v(-33.4, 23.13) * mm, "end": v(-36.02, 23.25) * mm});
            skLineSegment(sketch, "E497", {"start": v(-36.02, 23.25) * mm, "end": v(-38.64, 23.37) * mm});
            skLineSegment(sketch, "E498", {"start": v(-38.64, 23.37) * mm, "end": v(-41.24, 23.47) * mm});
            skLineSegment(sketch, "E499", {"start": v(-41.24, 23.47) * mm, "end": v(-43.84, 23.56) * mm});
            skLineSegment(sketch, "E500", {"start": v(-43.84, 23.56) * mm, "end": v(-46.42, 23.65) * mm});
            skLineSegment(sketch, "E501", {"start": v(-46.42, 23.65) * mm, "end": v(-48.99, 23.73) * mm});
            skLineSegment(sketch, "E502", {"start": v(-48.99, 23.73) * mm, "end": v(-51.55, 23.8) * mm});
            skLineSegment(sketch, "E503", {"start": v(-51.55, 23.8) * mm, "end": v(-54.1, 23.85) * mm});
            skLineSegment(sketch, "E504", {"start": v(-54.1, 23.85) * mm, "end": v(-56.63, 23.9) * mm});
            skLineSegment(sketch, "E505", {"start": v(-56.63, 23.9) * mm, "end": v(-59.14, 23.94) * mm});
            skLineSegment(sketch, "E506", {"start": v(-59.14, 23.94) * mm, "end": v(-61.65, 23.97) * mm});
            skLineSegment(sketch, "E507", {"start": v(-61.65, 23.97) * mm, "end": v(-64.13, 24) * mm});
            skLineSegment(sketch, "E508", {"start": v(-64.13, 24) * mm, "end": v(-66.6, 24) * mm});
            skLineSegment(sketch, "E509", {"start": v(-66.6, 24) * mm, "end": v(-69.06, 24) * mm});
            skLineSegment(sketch, "E510", {"start": v(-69.06, 24) * mm, "end": v(-71.5, 24) * mm});
            skLineSegment(sketch, "E511", {"start": v(-71.5, 24) * mm, "end": v(-73.92, 23.98) * mm});
            skLineSegment(sketch, "E512", {"start": v(-73.92, 23.98) * mm, "end": v(-76.32, 23.95) * mm});
            skLineSegment(sketch, "E513", {"start": v(-76.32, 23.95) * mm, "end": v(-78.7, 23.9) * mm});
            skLineSegment(sketch, "E514", {"start": v(-78.7, 23.9) * mm, "end": v(-81.06, 23.86) * mm});
            skLineSegment(sketch, "E515", {"start": v(-81.06, 23.86) * mm, "end": v(-83.4, 23.8) * mm});
            skLineSegment(sketch, "E516", {"start": v(-83.4, 23.8) * mm, "end": v(-85.72, 23.73) * mm});
            skLineSegment(sketch, "E517", {"start": v(-85.72, 23.73) * mm, "end": v(-88.02, 23.64) * mm});
            skLineSegment(sketch, "E518", {"start": v(-88.02, 23.64) * mm, "end": v(-90.3, 23.55) * mm});
            skLineSegment(sketch, "E519", {"start": v(-90.3, 23.55) * mm, "end": v(-92.55, 23.45) * mm});
            skLineSegment(sketch, "E520", {"start": v(-92.55, 23.45) * mm, "end": v(-94.78, 23.33) * mm});
            skLineSegment(sketch, "E521", {"start": v(-94.78, 23.33) * mm, "end": v(-97, 23.2) * mm});
            skLineSegment(sketch, "E522", {"start": v(-97, 23.2) * mm, "end": v(-99.17, 23.07) * mm});
            skLineSegment(sketch, "E523", {"start": v(-99.17, 23.07) * mm, "end": v(-101.33, 22.93) * mm});
            skLineSegment(sketch, "E524", {"start": v(-101.33, 22.93) * mm, "end": v(-103.46, 22.77) * mm});
            skLineSegment(sketch, "E525", {"start": v(-103.46, 22.77) * mm, "end": v(-105.57, 22.6) * mm});
            skLineSegment(sketch, "E526", {"start": v(-105.57, 22.6) * mm, "end": v(-107.65, 22.43) * mm});
            skLineSegment(sketch, "E527", {"start": v(-107.65, 22.43) * mm, "end": v(-109.7, 22.24) * mm});
            skLineSegment(sketch, "E528", {"start": v(-109.7, 22.24) * mm, "end": v(-111.73, 22.04) * mm});
            skLineSegment(sketch, "E529", {"start": v(-111.73, 22.04) * mm, "end": v(-113.72, 21.83) * mm});
            skLineSegment(sketch, "E530", {"start": v(-113.72, 21.83) * mm, "end": v(-115.7, 21.6) * mm});
            skLineSegment(sketch, "E531", {"start": v(-115.7, 21.6) * mm, "end": v(-117.63, 21.38) * mm});
            skLineSegment(sketch, "E532", {"start": v(-117.63, 21.38) * mm, "end": v(-119.54, 21.14) * mm});
            skLineSegment(sketch, "E533", {"start": v(-119.54, 21.14) * mm, "end": v(-121.42, 20.88) * mm});
            skLineSegment(sketch, "E534", {"start": v(-121.42, 20.88) * mm, "end": v(-123.27, 20.62) * mm});
            skLineSegment(sketch, "E535", {"start": v(-123.27, 20.62) * mm, "end": v(-125.08, 20.35) * mm});
            skLineSegment(sketch, "E536", {"start": v(-125.08, 20.35) * mm, "end": v(-126.87, 20.07) * mm});
            skLineSegment(sketch, "E537", {"start": v(-126.87, 20.07) * mm, "end": v(-128.62, 19.78) * mm});
            skLineSegment(sketch, "E538", {"start": v(-128.62, 19.78) * mm, "end": v(-130.34, 19.48) * mm});
            skLineSegment(sketch, "E539", {"start": v(-130.34, 19.48) * mm, "end": v(-132.03, 19.16) * mm});
            skLineSegment(sketch, "E540", {"start": v(-132.03, 19.16) * mm, "end": v(-133.69, 18.84) * mm});
            skLineSegment(sketch, "E541", {"start": v(-133.69, 18.84) * mm, "end": v(-135.3, 18.51) * mm});
            skLineSegment(sketch, "E542", {"start": v(-135.3, 18.51) * mm, "end": v(-136.9, 18.18) * mm});
            skLineSegment(sketch, "E543", {"start": v(-136.9, 18.18) * mm, "end": v(-138.45, 17.83) * mm});
            skLineSegment(sketch, "E544", {"start": v(-138.45, 17.83) * mm, "end": v(-139.96, 17.47) * mm});
            skLineSegment(sketch, "E545", {"start": v(-139.96, 17.47) * mm, "end": v(-141.45, 17.1) * mm});
            skLineSegment(sketch, "E546", {"start": v(-141.45, 17.1) * mm, "end": v(-142.9, 16.73) * mm});
            skLineSegment(sketch, "E547", {"start": v(-142.9, 16.73) * mm, "end": v(-144.3, 16.35) * mm});
            skLineSegment(sketch, "E548", {"start": v(-144.3, 16.35) * mm, "end": v(-145.67, 15.96) * mm});
            skLineSegment(sketch, "E549", {"start": v(-145.67, 15.96) * mm, "end": v(-147, 15.56) * mm});
            skLineSegment(sketch, "E550", {"start": v(-147, 15.56) * mm, "end": v(-148.3, 15.15) * mm});
            skLineSegment(sketch, "E551", {"start": v(-148.3, 15.15) * mm, "end": v(-149.57, 14.74) * mm});
            skLineSegment(sketch, "E552", {"start": v(-149.57, 14.74) * mm, "end": v(-150.79, 14.32) * mm});
            skLineSegment(sketch, "E553", {"start": v(-150.79, 14.32) * mm, "end": v(-151.97, 13.9) * mm});
            skLineSegment(sketch, "E554", {"start": v(-151.97, 13.9) * mm, "end": v(-153.12, 13.46) * mm});
            skLineSegment(sketch, "E555", {"start": v(-153.12, 13.46) * mm, "end": v(-154.22, 13.01) * mm});
            skLineSegment(sketch, "E556", {"start": v(-154.22, 13.01) * mm, "end": v(-155.29, 12.57) * mm});
            skLineSegment(sketch, "E557", {"start": v(-155.29, 12.57) * mm, "end": v(-156.31, 12.11) * mm});
            skLineSegment(sketch, "E558", {"start": v(-156.31, 12.11) * mm, "end": v(-157.3, 11.66) * mm});
            skLineSegment(sketch, "E559", {"start": v(-157.3, 11.66) * mm, "end": v(-158.24, 11.2) * mm});
            skLineSegment(sketch, "E560", {"start": v(-158.24, 11.2) * mm, "end": v(-159.14, 10.72) * mm});
            skLineSegment(sketch, "E561", {"start": v(-159.14, 10.72) * mm, "end": v(-160, 10.25) * mm});
            skLineSegment(sketch, "E562", {"start": v(-160, 10.25) * mm, "end": v(-160.82, 9.77) * mm});
            skLineSegment(sketch, "E563", {"start": v(-160.82, 9.77) * mm, "end": v(-161.6, 9.29) * mm});
            skLineSegment(sketch, "E564", {"start": v(-161.6, 9.29) * mm, "end": v(-162.34, 8.8) * mm});
            skLineSegment(sketch, "E565", {"start": v(-162.34, 8.8) * mm, "end": v(-163.03, 8.31) * mm});
            skLineSegment(sketch, "E566", {"start": v(-163.03, 8.31) * mm, "end": v(-163.68, 7.82) * mm});
            skLineSegment(sketch, "E567", {"start": v(-163.68, 7.82) * mm, "end": v(-164.3, 7.33) * mm});
            skLineSegment(sketch, "E568", {"start": v(-164.3, 7.33) * mm, "end": v(-164.86, 6.84) * mm});
            skLineSegment(sketch, "E569", {"start": v(-164.86, 6.84) * mm, "end": v(-165.38, 6.34) * mm});
            skLineSegment(sketch, "E570", {"start": v(-165.38, 6.34) * mm, "end": v(-165.86, 5.85) * mm});
            skLineSegment(sketch, "E571", {"start": v(-165.86, 5.85) * mm, "end": v(-166.3, 5.35) * mm});
            skLineSegment(sketch, "E572", {"start": v(-166.3, 5.35) * mm, "end": v(-166.7, 4.86) * mm});
            skLineSegment(sketch, "E573", {"start": v(-166.7, 4.86) * mm, "end": v(-167.05, 4.37) * mm});
            skLineSegment(sketch, "E574", {"start": v(-167.05, 4.37) * mm, "end": v(-167.36, 3.88) * mm});
            skLineSegment(sketch, "E575", {"start": v(-167.36, 3.88) * mm, "end": v(-167.63, 3.39) * mm});
            skLineSegment(sketch, "E576", {"start": v(-167.63, 3.39) * mm, "end": v(-167.87, 2.9) * mm});
            skLineSegment(sketch, "E577", {"start": v(-167.87, 2.9) * mm, "end": v(-168.06, 2.42) * mm});
            skLineSegment(sketch, "E578", {"start": v(-168.06, 2.42) * mm, "end": v(-168.22, 1.94) * mm});
            skLineSegment(sketch, "E579", {"start": v(-168.22, 1.94) * mm, "end": v(-168.34, 1.46) * mm});
            skLineSegment(sketch, "E580", {"start": v(-168.34, 1.46) * mm, "end": v(-168.43, 0.97) * mm});
            skLineSegment(sketch, "E581", {"start": v(-168.43, 0.97) * mm, "end": v(-168.48, 0.49) * mm});
            skLineSegment(sketch, "E582", {"start": v(-168.48, 0.49) * mm, "end": v(-168.5, 0) * mm});
            skLineSegment(sketch, "E583", {"start": v(-168.5, 0) * mm, "end": v(-168.48, -0.49) * mm});
            skLineSegment(sketch, "E584", {"start": v(-168.48, -0.49) * mm, "end": v(-168.43, -0.97) * mm});
            skLineSegment(sketch, "E585", {"start": v(-168.43, -0.97) * mm, "end": v(-168.34, -1.46) * mm});
            skLineSegment(sketch, "E586", {"start": v(-168.34, -1.46) * mm, "end": v(-168.22, -1.94) * mm});
            skLineSegment(sketch, "E587", {"start": v(-168.22, -1.94) * mm, "end": v(-168.06, -2.42) * mm});
            skLineSegment(sketch, "E588", {"start": v(-168.06, -2.42) * mm, "end": v(-167.87, -2.9) * mm});
            skLineSegment(sketch, "E589", {"start": v(-167.87, -2.9) * mm, "end": v(-167.63, -3.39) * mm});
            skLineSegment(sketch, "E590", {"start": v(-167.63, -3.39) * mm, "end": v(-167.36, -3.88) * mm});
            skLineSegment(sketch, "E591", {"start": v(-167.36, -3.88) * mm, "end": v(-167.05, -4.37) * mm});
            skLineSegment(sketch, "E592", {"start": v(-167.05, -4.37) * mm, "end": v(-166.7, -4.86) * mm});
            skLineSegment(sketch, "E593", {"start": v(-166.7, -4.86) * mm, "end": v(-166.3, -5.35) * mm});
            skLineSegment(sketch, "E594", {"start": v(-166.3, -5.35) * mm, "end": v(-165.86, -5.85) * mm});
            skLineSegment(sketch, "E595", {"start": v(-165.86, -5.85) * mm, "end": v(-165.38, -6.34) * mm});
            skLineSegment(sketch, "E596", {"start": v(-165.38, -6.34) * mm, "end": v(-164.86, -6.84) * mm});
            skLineSegment(sketch, "E597", {"start": v(-164.86, -6.84) * mm, "end": v(-164.3, -7.33) * mm});
            skLineSegment(sketch, "E598", {"start": v(-164.3, -7.33) * mm, "end": v(-163.68, -7.82) * mm});
            skLineSegment(sketch, "E599", {"start": v(-163.68, -7.82) * mm, "end": v(-163.03, -8.31) * mm});
            skLineSegment(sketch, "E600", {"start": v(-163.03, -8.31) * mm, "end": v(-162.34, -8.8) * mm});
            skLineSegment(sketch, "E601", {"start": v(-162.34, -8.8) * mm, "end": v(-161.6, -9.29) * mm});
            skLineSegment(sketch, "E602", {"start": v(-161.6, -9.29) * mm, "end": v(-160.82, -9.77) * mm});
            skLineSegment(sketch, "E603", {"start": v(-160.82, -9.77) * mm, "end": v(-160, -10.25) * mm});
            skLineSegment(sketch, "E604", {"start": v(-160, -10.25) * mm, "end": v(-159.14, -10.72) * mm});
            skLineSegment(sketch, "E605", {"start": v(-159.14, -10.72) * mm, "end": v(-158.24, -11.2) * mm});
            skLineSegment(sketch, "E606", {"start": v(-158.24, -11.2) * mm, "end": v(-157.3, -11.66) * mm});
            skLineSegment(sketch, "E607", {"start": v(-157.3, -11.66) * mm, "end": v(-156.31, -12.11) * mm});
            skLineSegment(sketch, "E608", {"start": v(-156.31, -12.11) * mm, "end": v(-155.29, -12.57) * mm});
            skLineSegment(sketch, "E609", {"start": v(-155.29, -12.57) * mm, "end": v(-154.22, -13.01) * mm});
            skLineSegment(sketch, "E610", {"start": v(-154.22, -13.01) * mm, "end": v(-153.12, -13.46) * mm});
            skLineSegment(sketch, "E611", {"start": v(-153.12, -13.46) * mm, "end": v(-151.97, -13.9) * mm});
            skLineSegment(sketch, "E612", {"start": v(-151.97, -13.9) * mm, "end": v(-150.79, -14.32) * mm});
            skLineSegment(sketch, "E613", {"start": v(-150.79, -14.32) * mm, "end": v(-149.57, -14.74) * mm});
            skLineSegment(sketch, "E614", {"start": v(-149.57, -14.74) * mm, "end": v(-148.3, -15.15) * mm});
            skLineSegment(sketch, "E615", {"start": v(-148.3, -15.15) * mm, "end": v(-147, -15.56) * mm});
            skLineSegment(sketch, "E616", {"start": v(-147, -15.56) * mm, "end": v(-145.67, -15.96) * mm});
            skLineSegment(sketch, "E617", {"start": v(-145.67, -15.96) * mm, "end": v(-144.3, -16.35) * mm});
            skLineSegment(sketch, "E618", {"start": v(-144.3, -16.35) * mm, "end": v(-142.9, -16.73) * mm});
            skLineSegment(sketch, "E619", {"start": v(-142.9, -16.73) * mm, "end": v(-141.45, -17.1) * mm});
            skLineSegment(sketch, "E620", {"start": v(-141.45, -17.1) * mm, "end": v(-139.96, -17.47) * mm});
            skLineSegment(sketch, "E621", {"start": v(-139.96, -17.47) * mm, "end": v(-138.45, -17.83) * mm});
            skLineSegment(sketch, "E622", {"start": v(-138.45, -17.83) * mm, "end": v(-136.9, -18.18) * mm});
            skLineSegment(sketch, "E623", {"start": v(-136.9, -18.18) * mm, "end": v(-135.3, -18.51) * mm});
            skLineSegment(sketch, "E624", {"start": v(-135.3, -18.51) * mm, "end": v(-133.69, -18.84) * mm});
            skLineSegment(sketch, "E625", {"start": v(-133.69, -18.84) * mm, "end": v(-132.03, -19.16) * mm});
            skLineSegment(sketch, "E626", {"start": v(-132.03, -19.16) * mm, "end": v(-130.34, -19.48) * mm});
            skLineSegment(sketch, "E627", {"start": v(-130.34, -19.48) * mm, "end": v(-128.62, -19.78) * mm});
            skLineSegment(sketch, "E628", {"start": v(-128.62, -19.78) * mm, "end": v(-126.87, -20.07) * mm});
            skLineSegment(sketch, "E629", {"start": v(-126.87, -20.07) * mm, "end": v(-125.08, -20.35) * mm});
            skLineSegment(sketch, "E630", {"start": v(-125.08, -20.35) * mm, "end": v(-123.27, -20.62) * mm});
            skLineSegment(sketch, "E631", {"start": v(-123.27, -20.62) * mm, "end": v(-121.42, -20.88) * mm});
            skLineSegment(sketch, "E632", {"start": v(-121.42, -20.88) * mm, "end": v(-119.54, -21.14) * mm});
            skLineSegment(sketch, "E633", {"start": v(-119.54, -21.14) * mm, "end": v(-117.63, -21.38) * mm});
            skLineSegment(sketch, "E634", {"start": v(-117.63, -21.38) * mm, "end": v(-115.7, -21.6) * mm});
            skLineSegment(sketch, "E635", {"start": v(-115.7, -21.6) * mm, "end": v(-113.72, -21.83) * mm});
            skLineSegment(sketch, "E636", {"start": v(-113.72, -21.83) * mm, "end": v(-111.73, -22.04) * mm});
            skLineSegment(sketch, "E637", {"start": v(-111.73, -22.04) * mm, "end": v(-109.7, -22.24) * mm});
            skLineSegment(sketch, "E638", {"start": v(-109.7, -22.24) * mm, "end": v(-107.65, -22.43) * mm});
            skLineSegment(sketch, "E639", {"start": v(-107.65, -22.43) * mm, "end": v(-105.57, -22.6) * mm});
            skLineSegment(sketch, "E640", {"start": v(-105.57, -22.6) * mm, "end": v(-103.46, -22.77) * mm});
            skLineSegment(sketch, "E641", {"start": v(-103.46, -22.77) * mm, "end": v(-101.33, -22.93) * mm});
            skLineSegment(sketch, "E642", {"start": v(-101.33, -22.93) * mm, "end": v(-99.17, -23.07) * mm});
            skLineSegment(sketch, "E643", {"start": v(-99.17, -23.07) * mm, "end": v(-97, -23.2) * mm});
            skLineSegment(sketch, "E644", {"start": v(-97, -23.2) * mm, "end": v(-94.78, -23.33) * mm});
            skLineSegment(sketch, "E645", {"start": v(-94.78, -23.33) * mm, "end": v(-92.55, -23.45) * mm});
            skLineSegment(sketch, "E646", {"start": v(-92.55, -23.45) * mm, "end": v(-90.3, -23.55) * mm});
            skLineSegment(sketch, "E647", {"start": v(-90.3, -23.55) * mm, "end": v(-88.02, -23.64) * mm});
            skLineSegment(sketch, "E648", {"start": v(-88.02, -23.64) * mm, "end": v(-85.72, -23.73) * mm});
            skLineSegment(sketch, "E649", {"start": v(-85.72, -23.73) * mm, "end": v(-83.4, -23.8) * mm});
            skLineSegment(sketch, "E650", {"start": v(-83.4, -23.8) * mm, "end": v(-81.06, -23.86) * mm});
            skLineSegment(sketch, "E651", {"start": v(-81.06, -23.86) * mm, "end": v(-78.7, -23.9) * mm});
            skLineSegment(sketch, "E652", {"start": v(-78.7, -23.9) * mm, "end": v(-76.32, -23.95) * mm});
            skLineSegment(sketch, "E653", {"start": v(-76.32, -23.95) * mm, "end": v(-73.92, -23.98) * mm});
            skLineSegment(sketch, "E654", {"start": v(-73.92, -23.98) * mm, "end": v(-71.5, -24) * mm});
            skLineSegment(sketch, "E655", {"start": v(-71.5, -24) * mm, "end": v(-69.06, -24) * mm});
            skLineSegment(sketch, "E656", {"start": v(-69.06, -24) * mm, "end": v(-66.6, -24) * mm});
            skLineSegment(sketch, "E657", {"start": v(-66.6, -24) * mm, "end": v(-64.13, -24) * mm});
            skLineSegment(sketch, "E658", {"start": v(-64.13, -24) * mm, "end": v(-61.65, -23.97) * mm});
            skLineSegment(sketch, "E659", {"start": v(-61.65, -23.97) * mm, "end": v(-59.14, -23.94) * mm});
            skLineSegment(sketch, "E660", {"start": v(-59.14, -23.94) * mm, "end": v(-56.63, -23.9) * mm});
            skLineSegment(sketch, "E661", {"start": v(-56.63, -23.9) * mm, "end": v(-54.1, -23.85) * mm});
            skLineSegment(sketch, "E662", {"start": v(-54.1, -23.85) * mm, "end": v(-51.55, -23.8) * mm});
            skLineSegment(sketch, "E663", {"start": v(-51.55, -23.8) * mm, "end": v(-48.99, -23.73) * mm});
            skLineSegment(sketch, "E664", {"start": v(-48.99, -23.73) * mm, "end": v(-46.42, -23.65) * mm});
            skLineSegment(sketch, "E665", {"start": v(-46.42, -23.65) * mm, "end": v(-43.84, -23.56) * mm});
            skLineSegment(sketch, "E666", {"start": v(-43.84, -23.56) * mm, "end": v(-41.24, -23.47) * mm});
            skLineSegment(sketch, "E667", {"start": v(-41.24, -23.47) * mm, "end": v(-38.64, -23.37) * mm});
            skLineSegment(sketch, "E668", {"start": v(-38.64, -23.37) * mm, "end": v(-36.02, -23.25) * mm});
            skLineSegment(sketch, "E669", {"start": v(-36.02, -23.25) * mm, "end": v(-33.4, -23.13) * mm});
            skLineSegment(sketch, "E670", {"start": v(-33.4, -23.13) * mm, "end": v(-30.77, -23) * mm});
            skLineSegment(sketch, "E671", {"start": v(-30.77, -23) * mm, "end": v(-28.13, -22.87) * mm});
            skLineSegment(sketch, "E672", {"start": v(-28.13, -22.87) * mm, "end": v(-25.48, -22.72) * mm});
            skLineSegment(sketch, "E673", {"start": v(-25.48, -22.72) * mm, "end": v(-22.83, -22.57) * mm});
            skLineSegment(sketch, "E674", {"start": v(-22.83, -22.57) * mm, "end": v(-20.17, -22.41) * mm});
            skLineSegment(sketch, "E675", {"start": v(-20.17, -22.41) * mm, "end": v(-17.5, -22.25) * mm});
            skLineSegment(sketch, "E676", {"start": v(-17.5, -22.25) * mm, "end": v(-14.84, -22.07) * mm});
            skLineSegment(sketch, "E677", {"start": v(-14.84, -22.07) * mm, "end": v(-12.17, -21.9) * mm});
            skLineSegment(sketch, "E678", {"start": v(-12.17, -21.9) * mm, "end": v(-9.5, -21.7) * mm});
            skLineSegment(sketch, "E679", {"start": v(-9.5, -21.7) * mm, "end": v(-6.82, -21.51) * mm});
            skLineSegment(sketch, "E680", {"start": v(-6.82, -21.51) * mm, "end": v(-4.14, -21.31) * mm});
            skLineSegment(sketch, "E681", {"start": v(-4.14, -21.31) * mm, "end": v(-1.46, -21.1) * mm});
            skLineSegment(sketch, "E682", {"start": v(-1.46, -21.1) * mm, "end": v(1.22, -20.9) * mm});
            skLineSegment(sketch, "E683", {"start": v(1.22, -20.9) * mm, "end": v(3.9, -20.68) * mm});
            skLineSegment(sketch, "E684", {"start": v(3.9, -20.68) * mm, "end": v(6.58, -20.46) * mm});
            skLineSegment(sketch, "E685", {"start": v(6.58, -20.46) * mm, "end": v(9.26, -20.23) * mm});
            skLineSegment(sketch, "E686", {"start": v(9.26, -20.23) * mm, "end": v(11.94, -20) * mm});
            skLineSegment(sketch, "E687", {"start": v(11.94, -20) * mm, "end": v(14.6, -19.76) * mm});
            skLineSegment(sketch, "E688", {"start": v(14.6, -19.76) * mm, "end": v(17.28, -19.52) * mm});
            skLineSegment(sketch, "E689", {"start": v(17.28, -19.52) * mm, "end": v(19.94, -19.27) * mm});
            skLineSegment(sketch, "E690", {"start": v(19.94, -19.27) * mm, "end": v(22.6, -19.02) * mm});
            skLineSegment(sketch, "E691", {"start": v(22.6, -19.02) * mm, "end": v(25.26, -18.76) * mm});
            skLineSegment(sketch, "E692", {"start": v(25.26, -18.76) * mm, "end": v(27.9, -18.5) * mm});
            skLineSegment(sketch, "E693", {"start": v(27.9, -18.5) * mm, "end": v(30.54, -18.24) * mm});
            skLineSegment(sketch, "E694", {"start": v(30.54, -18.24) * mm, "end": v(33.18, -17.97) * mm});
            skLineSegment(sketch, "E695", {"start": v(33.18, -17.97) * mm, "end": v(35.8, -17.7) * mm});
            skLineSegment(sketch, "E696", {"start": v(35.8, -17.7) * mm, "end": v(38.42, -17.43) * mm});
            skLineSegment(sketch, "E697", {"start": v(38.42, -17.43) * mm, "end": v(41.03, -17.15) * mm});
            skLineSegment(sketch, "E698", {"start": v(41.03, -17.15) * mm, "end": v(43.62, -16.87) * mm});
            skLineSegment(sketch, "E699", {"start": v(43.62, -16.87) * mm, "end": v(46.2, -16.59) * mm});
            skLineSegment(sketch, "E700", {"start": v(46.2, -16.59) * mm, "end": v(48.78, -16.3) * mm});
            skLineSegment(sketch, "E701", {"start": v(48.78, -16.3) * mm, "end": v(51.34, -16.02) * mm});
            skLineSegment(sketch, "E702", {"start": v(51.34, -16.02) * mm, "end": v(53.9, -15.73) * mm});
            skLineSegment(sketch, "E703", {"start": v(53.9, -15.73) * mm, "end": v(56.43, -15.43) * mm});
            skLineSegment(sketch, "E704", {"start": v(56.43, -15.43) * mm, "end": v(58.95, -15.14) * mm});
            skLineSegment(sketch, "E705", {"start": v(58.95, -15.14) * mm, "end": v(61.46, -14.85) * mm});
            skLineSegment(sketch, "E706", {"start": v(61.46, -14.85) * mm, "end": v(63.95, -14.55) * mm});
            skLineSegment(sketch, "E707", {"start": v(63.95, -14.55) * mm, "end": v(66.42, -14.25) * mm});
            skLineSegment(sketch, "E708", {"start": v(66.42, -14.25) * mm, "end": v(68.88, -13.95) * mm});
            skLineSegment(sketch, "E709", {"start": v(68.88, -13.95) * mm, "end": v(71.32, -13.65) * mm});
            skLineSegment(sketch, "E710", {"start": v(71.32, -13.65) * mm, "end": v(73.75, -13.35) * mm});
            skLineSegment(sketch, "E711", {"start": v(73.75, -13.35) * mm, "end": v(76.15, -13.05) * mm});
            skLineSegment(sketch, "E712", {"start": v(76.15, -13.05) * mm, "end": v(78.54, -12.75) * mm});
            skLineSegment(sketch, "E713", {"start": v(78.54, -12.75) * mm, "end": v(80.9, -12.45) * mm});
            skLineSegment(sketch, "E714", {"start": v(80.9, -12.45) * mm, "end": v(83.25, -12.15) * mm});
            skLineSegment(sketch, "E715", {"start": v(83.25, -12.15) * mm, "end": v(85.58, -11.84) * mm});
            skLineSegment(sketch, "E716", {"start": v(85.58, -11.84) * mm, "end": v(87.88, -11.54) * mm});
            skLineSegment(sketch, "E717", {"start": v(87.88, -11.54) * mm, "end": v(90.17, -11.24) * mm});
            skLineSegment(sketch, "E718", {"start": v(90.17, -11.24) * mm, "end": v(92.43, -10.94) * mm});
            skLineSegment(sketch, "E719", {"start": v(92.43, -10.94) * mm, "end": v(94.66, -10.64) * mm});
            skLineSegment(sketch, "E720", {"start": v(94.66, -10.64) * mm, "end": v(96.88, -10.34) * mm});
            skLineSegment(sketch, "E721", {"start": v(96.88, -10.34) * mm, "end": v(99.07, -10.04) * mm});
            skLineSegment(sketch, "E722", {"start": v(99.07, -10.04) * mm, "end": v(101.23, -9.74) * mm});
            skLineSegment(sketch, "E723", {"start": v(101.23, -9.74) * mm, "end": v(103.37, -9.44) * mm});
            skLineSegment(sketch, "E724", {"start": v(103.37, -9.44) * mm, "end": v(105.48, -9.15) * mm});
            skLineSegment(sketch, "E725", {"start": v(105.48, -9.15) * mm, "end": v(107.57, -8.85) * mm});
            skLineSegment(sketch, "E726", {"start": v(107.57, -8.85) * mm, "end": v(109.63, -8.56) * mm});
            skLineSegment(sketch, "E727", {"start": v(109.63, -8.56) * mm, "end": v(111.67, -8.27) * mm});
            skLineSegment(sketch, "E728", {"start": v(111.67, -8.27) * mm, "end": v(113.67, -7.98) * mm});
            skLineSegment(sketch, "E729", {"start": v(113.67, -7.98) * mm, "end": v(115.65, -7.7) * mm});
            skLineSegment(sketch, "E730", {"start": v(115.65, -7.7) * mm, "end": v(117.6, -7.41) * mm});
            skLineSegment(sketch, "E731", {"start": v(117.6, -7.41) * mm, "end": v(119.51, -7.13) * mm});
            skLineSegment(sketch, "E732", {"start": v(119.51, -7.13) * mm, "end": v(121.4, -6.85) * mm});
            skLineSegment(sketch, "E733", {"start": v(121.4, -6.85) * mm, "end": v(123.26, -6.58) * mm});
            skLineSegment(sketch, "E734", {"start": v(123.26, -6.58) * mm, "end": v(125.09, -6.3) * mm});
            skLineSegment(sketch, "E735", {"start": v(125.09, -6.3) * mm, "end": v(126.89, -6.03) * mm});
            skLineSegment(sketch, "E736", {"start": v(126.89, -6.03) * mm, "end": v(128.65, -5.77) * mm});
            skLineSegment(sketch, "E737", {"start": v(128.65, -5.77) * mm, "end": v(130.38, -5.5) * mm});
            skLineSegment(sketch, "E738", {"start": v(130.38, -5.5) * mm, "end": v(132.08, -5.24) * mm});
            skLineSegment(sketch, "E739", {"start": v(132.08, -5.24) * mm, "end": v(133.75, -4.98) * mm});
            skLineSegment(sketch, "E740", {"start": v(133.75, -4.98) * mm, "end": v(135.39, -4.73) * mm});
            skLineSegment(sketch, "E741", {"start": v(135.39, -4.73) * mm, "end": v(136.99, -4.48) * mm});
            skLineSegment(sketch, "E742", {"start": v(136.99, -4.48) * mm, "end": v(138.55, -4.24) * mm});
            skLineSegment(sketch, "E743", {"start": v(138.55, -4.24) * mm, "end": v(140.08, -4) * mm});
            skLineSegment(sketch, "E744", {"start": v(140.08, -4) * mm, "end": v(141.58, -3.76) * mm});
            skLineSegment(sketch, "E745", {"start": v(141.58, -3.76) * mm, "end": v(143.04, -3.52) * mm});
            skLineSegment(sketch, "E746", {"start": v(143.04, -3.52) * mm, "end": v(144.47, -3.3) * mm});
            skLineSegment(sketch, "E747", {"start": v(144.47, -3.3) * mm, "end": v(145.85, -3.07) * mm});
            skLineSegment(sketch, "E748", {"start": v(145.85, -3.07) * mm, "end": v(147.2, -2.85) * mm});
            skLineSegment(sketch, "E749", {"start": v(147.2, -2.85) * mm, "end": v(148.52, -2.64) * mm});
            skLineSegment(sketch, "E750", {"start": v(148.52, -2.64) * mm, "end": v(149.8, -2.43) * mm});
            skLineSegment(sketch, "E751", {"start": v(149.8, -2.43) * mm, "end": v(151.04, -2.23) * mm});
            skLineSegment(sketch, "E752", {"start": v(151.04, -2.23) * mm, "end": v(152.25, -2.03) * mm});
            skLineSegment(sketch, "E753", {"start": v(152.25, -2.03) * mm, "end": v(153.42, -1.84) * mm});
            skLineSegment(sketch, "E754", {"start": v(153.42, -1.84) * mm, "end": v(154.54, -1.65) * mm});
            skLineSegment(sketch, "E755", {"start": v(154.54, -1.65) * mm, "end": v(155.63, -1.47) * mm});
            skLineSegment(sketch, "E756", {"start": v(155.63, -1.47) * mm, "end": v(156.68, -1.3) * mm});
            skLineSegment(sketch, "E757", {"start": v(156.68, -1.3) * mm, "end": v(157.7, -1.13) * mm});
            skLineSegment(sketch, "E758", {"start": v(157.7, -1.13) * mm, "end": v(158.67, -0.96) * mm});
            skLineSegment(sketch, "E759", {"start": v(158.67, -0.96) * mm, "end": v(159.6, -0.8) * mm});
            skLineSegment(sketch, "E760", {"start": v(159.6, -0.8) * mm, "end": v(160.5, -0.65) * mm});
            skLineSegment(sketch, "E761", {"start": v(160.5, -0.65) * mm, "end": v(161.34, -0.5) * mm});
            skLineSegment(sketch, "E762", {"start": v(161.34, -0.5) * mm, "end": v(162.16, -0.37) * mm});
            skLineSegment(sketch, "E763", {"start": v(162.16, -0.37) * mm, "end": v(162.93, -0.24) * mm});
            skLineSegment(sketch, "E764", {"start": v(162.93, -0.24) * mm, "end": v(163.66, -0.11) * mm});
            skLineSegment(sketch, "E765", {"start": v(163.66, -0.11) * mm, "end": v(164.32, 0) * mm});
            skSolve(sketch);
        }
        {
            var Q0;
            Q0=qCreatedBy(id+"F0.planeOp",FACE);
            var sketch = newSketch(context, id + "F2", { "sketchPlane" : qUnion([Q0])});
            skLineSegment(sketch, "E766", {"start": v(-30, 0.01) * mm, "end": v(170, 0.01) * mm, "construction": true});
            skLineSegment(sketch, "E767", {"start": v(169.96, 0.33) * mm, "end": v(169.95, 0.33) * mm});
            skLineSegment(sketch, "E768", {"start": v(169.95, 0.33) * mm, "end": v(169.91, 0.34) * mm});
            skLineSegment(sketch, "E769", {"start": v(169.91, 0.34) * mm, "end": v(169.85, 0.35) * mm});
            skLineSegment(sketch, "E770", {"start": v(169.85, 0.35) * mm, "end": v(169.76, 0.36) * mm});
            skLineSegment(sketch, "E771", {"start": v(169.76, 0.36) * mm, "end": v(169.65, 0.38) * mm});
            skLineSegment(sketch, "E772", {"start": v(169.65, 0.38) * mm, "end": v(169.51, 0.4) * mm});
            skLineSegment(sketch, "E773", {"start": v(169.51, 0.4) * mm, "end": v(169.35, 0.43) * mm});
            skLineSegment(sketch, "E774", {"start": v(169.35, 0.43) * mm, "end": v(169.16, 0.47) * mm});
            skLineSegment(sketch, "E775", {"start": v(169.16, 0.47) * mm, "end": v(168.95, 0.5) * mm});
            skLineSegment(sketch, "E776", {"start": v(168.95, 0.5) * mm, "end": v(168.72, 0.54) * mm});
            skLineSegment(sketch, "E777", {"start": v(168.72, 0.54) * mm, "end": v(168.46, 0.59) * mm});
            skLineSegment(sketch, "E778", {"start": v(168.46, 0.59) * mm, "end": v(168.17, 0.64) * mm});
            skLineSegment(sketch, "E779", {"start": v(168.17, 0.64) * mm, "end": v(167.86, 0.7) * mm});
            skLineSegment(sketch, "E780", {"start": v(167.86, 0.7) * mm, "end": v(167.53, 0.75) * mm});
            skLineSegment(sketch, "E781", {"start": v(167.53, 0.75) * mm, "end": v(167.17, 0.81) * mm});
            skLineSegment(sketch, "E782", {"start": v(167.17, 0.81) * mm, "end": v(166.79, 0.88) * mm});
            skLineSegment(sketch, "E783", {"start": v(166.79, 0.88) * mm, "end": v(166.38, 0.95) * mm});
            skLineSegment(sketch, "E784", {"start": v(166.38, 0.95) * mm, "end": v(165.95, 1.02) * mm});
            skLineSegment(sketch, "E785", {"start": v(165.95, 1.02) * mm, "end": v(165.5, 1.1) * mm});
            skLineSegment(sketch, "E786", {"start": v(165.5, 1.1) * mm, "end": v(165.02, 1.18) * mm});
            skLineSegment(sketch, "E787", {"start": v(165.02, 1.18) * mm, "end": v(164.52, 1.27) * mm});
            skLineSegment(sketch, "E788", {"start": v(164.52, 1.27) * mm, "end": v(163.99, 1.35) * mm});
            skLineSegment(sketch, "E789", {"start": v(163.99, 1.35) * mm, "end": v(163.44, 1.45) * mm});
            skLineSegment(sketch, "E790", {"start": v(163.44, 1.45) * mm, "end": v(162.87, 1.54) * mm});
            skLineSegment(sketch, "E791", {"start": v(162.87, 1.54) * mm, "end": v(162.27, 1.64) * mm});
            skLineSegment(sketch, "E792", {"start": v(162.27, 1.64) * mm, "end": v(161.65, 1.75) * mm});
            skLineSegment(sketch, "E793", {"start": v(161.65, 1.75) * mm, "end": v(161.01, 1.85) * mm});
            skLineSegment(sketch, "E794", {"start": v(161.01, 1.85) * mm, "end": v(160.35, 1.96) * mm});
            skLineSegment(sketch, "E795", {"start": v(160.35, 1.96) * mm, "end": v(159.66, 2.08) * mm});
            skLineSegment(sketch, "E796", {"start": v(159.66, 2.08) * mm, "end": v(158.95, 2.2) * mm});
            skLineSegment(sketch, "E797", {"start": v(158.95, 2.2) * mm, "end": v(158.22, 2.31) * mm});
            skLineSegment(sketch, "E798", {"start": v(158.22, 2.31) * mm, "end": v(157.47, 2.44) * mm});
            skLineSegment(sketch, "E799", {"start": v(157.47, 2.44) * mm, "end": v(156.7, 2.56) * mm});
            skLineSegment(sketch, "E800", {"start": v(156.7, 2.56) * mm, "end": v(155.9, 2.7) * mm});
            skLineSegment(sketch, "E801", {"start": v(155.9, 2.7) * mm, "end": v(155.08, 2.82) * mm});
            skLineSegment(sketch, "E802", {"start": v(155.08, 2.82) * mm, "end": v(154.24, 2.96) * mm});
            skLineSegment(sketch, "E803", {"start": v(154.24, 2.96) * mm, "end": v(153.38, 3.1) * mm});
            skLineSegment(sketch, "E804", {"start": v(153.38, 3.1) * mm, "end": v(152.5, 3.23) * mm});
            skLineSegment(sketch, "E805", {"start": v(152.5, 3.23) * mm, "end": v(151.6, 3.37) * mm});
            skLineSegment(sketch, "E806", {"start": v(151.6, 3.37) * mm, "end": v(150.68, 3.52) * mm});
            skLineSegment(sketch, "E807", {"start": v(150.68, 3.52) * mm, "end": v(149.73, 3.67) * mm});
            skLineSegment(sketch, "E808", {"start": v(149.73, 3.67) * mm, "end": v(148.77, 3.81) * mm});
            skLineSegment(sketch, "E809", {"start": v(148.77, 3.81) * mm, "end": v(147.8, 3.97) * mm});
            skLineSegment(sketch, "E810", {"start": v(147.8, 3.97) * mm, "end": v(146.79, 4.12) * mm});
            skLineSegment(sketch, "E811", {"start": v(146.79, 4.12) * mm, "end": v(145.77, 4.27) * mm});
            skLineSegment(sketch, "E812", {"start": v(145.77, 4.27) * mm, "end": v(144.73, 4.43) * mm});
            skLineSegment(sketch, "E813", {"start": v(144.73, 4.43) * mm, "end": v(143.67, 4.6) * mm});
            skLineSegment(sketch, "E814", {"start": v(143.67, 4.6) * mm, "end": v(142.6, 4.75) * mm});
            skLineSegment(sketch, "E815", {"start": v(142.6, 4.75) * mm, "end": v(141.5, 4.92) * mm});
            skLineSegment(sketch, "E816", {"start": v(141.5, 4.92) * mm, "end": v(140.4, 5.08) * mm});
            skLineSegment(sketch, "E817", {"start": v(140.4, 5.08) * mm, "end": v(139.26, 5.25) * mm});
            skLineSegment(sketch, "E818", {"start": v(139.26, 5.25) * mm, "end": v(138.12, 5.41) * mm});
            skLineSegment(sketch, "E819", {"start": v(138.12, 5.41) * mm, "end": v(136.95, 5.58) * mm});
            skLineSegment(sketch, "E820", {"start": v(136.95, 5.58) * mm, "end": v(135.77, 5.75) * mm});
            skLineSegment(sketch, "E821", {"start": v(135.77, 5.75) * mm, "end": v(134.57, 5.92) * mm});
            skLineSegment(sketch, "E822", {"start": v(134.57, 5.92) * mm, "end": v(133.36, 6.1) * mm});
            skLineSegment(sketch, "E823", {"start": v(133.36, 6.1) * mm, "end": v(132.13, 6.27) * mm});
            skLineSegment(sketch, "E824", {"start": v(132.13, 6.27) * mm, "end": v(130.89, 6.44) * mm});
            skLineSegment(sketch, "E825", {"start": v(130.89, 6.44) * mm, "end": v(129.63, 6.61) * mm});
            skLineSegment(sketch, "E826", {"start": v(129.63, 6.61) * mm, "end": v(128.36, 6.8) * mm});
            skLineSegment(sketch, "E827", {"start": v(128.36, 6.8) * mm, "end": v(127.07, 6.97) * mm});
            skLineSegment(sketch, "E828", {"start": v(127.07, 6.97) * mm, "end": v(125.76, 7.14) * mm});
            skLineSegment(sketch, "E829", {"start": v(125.76, 7.14) * mm, "end": v(124.45, 7.32) * mm});
            skLineSegment(sketch, "E830", {"start": v(124.45, 7.32) * mm, "end": v(123.12, 7.5) * mm});
            skLineSegment(sketch, "E831", {"start": v(123.12, 7.5) * mm, "end": v(121.77, 7.67) * mm});
            skLineSegment(sketch, "E832", {"start": v(121.77, 7.67) * mm, "end": v(120.42, 7.85) * mm});
            skLineSegment(sketch, "E833", {"start": v(120.42, 7.85) * mm, "end": v(119.05, 8.03) * mm});
            skLineSegment(sketch, "E834", {"start": v(119.05, 8.03) * mm, "end": v(117.66, 8.2) * mm});
            skLineSegment(sketch, "E835", {"start": v(117.66, 8.2) * mm, "end": v(116.27, 8.39) * mm});
            skLineSegment(sketch, "E836", {"start": v(116.27, 8.39) * mm, "end": v(114.87, 8.56) * mm});
            skLineSegment(sketch, "E837", {"start": v(114.87, 8.56) * mm, "end": v(113.45, 8.74) * mm});
            skLineSegment(sketch, "E838", {"start": v(113.45, 8.74) * mm, "end": v(112.02, 8.92) * mm});
            skLineSegment(sketch, "E839", {"start": v(112.02, 8.92) * mm, "end": v(110.59, 9.1) * mm});
            skLineSegment(sketch, "E840", {"start": v(110.59, 9.1) * mm, "end": v(109.14, 9.27) * mm});
            skLineSegment(sketch, "E841", {"start": v(109.14, 9.27) * mm, "end": v(107.68, 9.45) * mm});
            skLineSegment(sketch, "E842", {"start": v(107.68, 9.45) * mm, "end": v(106.21, 9.62) * mm});
            skLineSegment(sketch, "E843", {"start": v(106.21, 9.62) * mm, "end": v(104.74, 9.8) * mm});
            skLineSegment(sketch, "E844", {"start": v(104.74, 9.8) * mm, "end": v(103.25, 9.97) * mm});
            skLineSegment(sketch, "E845", {"start": v(103.25, 9.97) * mm, "end": v(101.76, 10.14) * mm});
            skLineSegment(sketch, "E846", {"start": v(101.76, 10.14) * mm, "end": v(100.26, 10.3) * mm});
            skLineSegment(sketch, "E847", {"start": v(100.26, 10.3) * mm, "end": v(98.75, 10.48) * mm});
            skLineSegment(sketch, "E848", {"start": v(98.75, 10.48) * mm, "end": v(97.24, 10.65) * mm});
            skLineSegment(sketch, "E849", {"start": v(97.24, 10.65) * mm, "end": v(95.72, 10.81) * mm});
            skLineSegment(sketch, "E850", {"start": v(95.72, 10.81) * mm, "end": v(94.19, 10.98) * mm});
            skLineSegment(sketch, "E851", {"start": v(94.19, 10.98) * mm, "end": v(92.65, 11.14) * mm});
            skLineSegment(sketch, "E852", {"start": v(92.65, 11.14) * mm, "end": v(91.11, 11.3) * mm});
            skLineSegment(sketch, "E853", {"start": v(91.11, 11.3) * mm, "end": v(89.57, 11.46) * mm});
            skLineSegment(sketch, "E854", {"start": v(89.57, 11.46) * mm, "end": v(88.02, 11.62) * mm});
            skLineSegment(sketch, "E855", {"start": v(88.02, 11.62) * mm, "end": v(86.46, 11.77) * mm});
            skLineSegment(sketch, "E856", {"start": v(86.46, 11.77) * mm, "end": v(84.9, 11.93) * mm});
            skLineSegment(sketch, "E857", {"start": v(84.9, 11.93) * mm, "end": v(83.34, 12.08) * mm});
            skLineSegment(sketch, "E858", {"start": v(83.34, 12.08) * mm, "end": v(81.77, 12.22) * mm});
            skLineSegment(sketch, "E859", {"start": v(81.77, 12.22) * mm, "end": v(80.2, 12.37) * mm});
            skLineSegment(sketch, "E860", {"start": v(80.2, 12.37) * mm, "end": v(78.63, 12.51) * mm});
            skLineSegment(sketch, "E861", {"start": v(78.63, 12.51) * mm, "end": v(77.06, 12.65) * mm});
            skLineSegment(sketch, "E862", {"start": v(77.06, 12.65) * mm, "end": v(75.48, 12.8) * mm});
            skLineSegment(sketch, "E863", {"start": v(75.48, 12.8) * mm, "end": v(73.9, 12.92) * mm});
            skLineSegment(sketch, "E864", {"start": v(73.9, 12.92) * mm, "end": v(72.33, 13.06) * mm});
            skLineSegment(sketch, "E865", {"start": v(72.33, 13.06) * mm, "end": v(70.75, 13.18) * mm});
            skLineSegment(sketch, "E866", {"start": v(70.75, 13.18) * mm, "end": v(69.17, 13.3) * mm});
            skLineSegment(sketch, "E867", {"start": v(69.17, 13.3) * mm, "end": v(67.6, 13.43) * mm});
            skLineSegment(sketch, "E868", {"start": v(67.6, 13.43) * mm, "end": v(66.01, 13.55) * mm});
            skLineSegment(sketch, "E869", {"start": v(66.01, 13.55) * mm, "end": v(64.44, 13.66) * mm});
            skLineSegment(sketch, "E870", {"start": v(64.44, 13.66) * mm, "end": v(62.86, 13.77) * mm});
            skLineSegment(sketch, "E871", {"start": v(62.86, 13.77) * mm, "end": v(61.29, 13.88) * mm});
            skLineSegment(sketch, "E872", {"start": v(61.29, 13.88) * mm, "end": v(59.72, 13.98) * mm});
            skLineSegment(sketch, "E873", {"start": v(59.72, 13.98) * mm, "end": v(58.15, 14.08) * mm});
            skLineSegment(sketch, "E874", {"start": v(58.15, 14.08) * mm, "end": v(56.58, 14.17) * mm});
            skLineSegment(sketch, "E875", {"start": v(56.58, 14.17) * mm, "end": v(55.02, 14.26) * mm});
            skLineSegment(sketch, "E876", {"start": v(55.02, 14.26) * mm, "end": v(53.46, 14.34) * mm});
            skLineSegment(sketch, "E877", {"start": v(53.46, 14.34) * mm, "end": v(51.9, 14.42) * mm});
            skLineSegment(sketch, "E878", {"start": v(51.9, 14.42) * mm, "end": v(50.35, 14.5) * mm});
            skLineSegment(sketch, "E879", {"start": v(50.35, 14.5) * mm, "end": v(48.8, 14.57) * mm});
            skLineSegment(sketch, "E880", {"start": v(48.8, 14.57) * mm, "end": v(47.27, 14.64) * mm});
            skLineSegment(sketch, "E881", {"start": v(47.27, 14.64) * mm, "end": v(45.73, 14.7) * mm});
            skLineSegment(sketch, "E882", {"start": v(45.73, 14.7) * mm, "end": v(44.2, 14.75) * mm});
            skLineSegment(sketch, "E883", {"start": v(44.2, 14.75) * mm, "end": v(42.68, 14.8) * mm});
            skLineSegment(sketch, "E884", {"start": v(42.68, 14.8) * mm, "end": v(41.17, 14.85) * mm});
            skLineSegment(sketch, "E885", {"start": v(41.17, 14.85) * mm, "end": v(39.66, 14.9) * mm});
            skLineSegment(sketch, "E886", {"start": v(39.66, 14.9) * mm, "end": v(38.16, 14.93) * mm});
            skLineSegment(sketch, "E887", {"start": v(38.16, 14.93) * mm, "end": v(36.67, 14.95) * mm});
            skLineSegment(sketch, "E888", {"start": v(36.67, 14.95) * mm, "end": v(35.18, 14.98) * mm});
            skLineSegment(sketch, "E889", {"start": v(35.18, 14.98) * mm, "end": v(33.7, 15) * mm});
            skLineSegment(sketch, "E890", {"start": v(33.7, 15) * mm, "end": v(32.24, 15) * mm});
            skLineSegment(sketch, "E891", {"start": v(32.24, 15) * mm, "end": v(30.78, 15.01) * mm});
            skLineSegment(sketch, "E892", {"start": v(30.78, 15.01) * mm, "end": v(29.33, 15.02) * mm});
            skLineSegment(sketch, "E893", {"start": v(29.33, 15.02) * mm, "end": v(27.9, 15) * mm});
            skLineSegment(sketch, "E894", {"start": v(27.9, 15) * mm, "end": v(26.47, 15) * mm});
            skLineSegment(sketch, "E895", {"start": v(26.47, 15) * mm, "end": v(25.05, 14.98) * mm});
            skLineSegment(sketch, "E896", {"start": v(25.05, 14.98) * mm, "end": v(23.65, 14.96) * mm});
            skLineSegment(sketch, "E897", {"start": v(23.65, 14.96) * mm, "end": v(22.26, 14.93) * mm});
            skLineSegment(sketch, "E898", {"start": v(22.26, 14.93) * mm, "end": v(20.87, 14.9) * mm});
            skLineSegment(sketch, "E899", {"start": v(20.87, 14.9) * mm, "end": v(19.5, 14.85) * mm});
            skLineSegment(sketch, "E900", {"start": v(19.5, 14.85) * mm, "end": v(18.15, 14.8) * mm});
            skLineSegment(sketch, "E901", {"start": v(18.15, 14.8) * mm, "end": v(16.8, 14.75) * mm});
            skLineSegment(sketch, "E902", {"start": v(16.8, 14.75) * mm, "end": v(15.47, 14.69) * mm});
            skLineSegment(sketch, "E903", {"start": v(15.47, 14.69) * mm, "end": v(14.16, 14.62) * mm});
            skLineSegment(sketch, "E904", {"start": v(14.16, 14.62) * mm, "end": v(12.85, 14.54) * mm});
            skLineSegment(sketch, "E905", {"start": v(12.85, 14.54) * mm, "end": v(11.57, 14.47) * mm});
            skLineSegment(sketch, "E906", {"start": v(11.57, 14.47) * mm, "end": v(10.3, 14.38) * mm});
            skLineSegment(sketch, "E907", {"start": v(10.3, 14.38) * mm, "end": v(9.03, 14.29) * mm});
            skLineSegment(sketch, "E908", {"start": v(9.03, 14.29) * mm, "end": v(7.79, 14.19) * mm});
            skLineSegment(sketch, "E909", {"start": v(7.79, 14.19) * mm, "end": v(6.56, 14.08) * mm});
            skLineSegment(sketch, "E910", {"start": v(6.56, 14.08) * mm, "end": v(5.35, 13.97) * mm});
            skLineSegment(sketch, "E911", {"start": v(5.35, 13.97) * mm, "end": v(4.15, 13.85) * mm});
            skLineSegment(sketch, "E912", {"start": v(4.15, 13.85) * mm, "end": v(2.97, 13.73) * mm});
            skLineSegment(sketch, "E913", {"start": v(2.97, 13.73) * mm, "end": v(1.8, 13.6) * mm});
            skLineSegment(sketch, "E914", {"start": v(1.8, 13.6) * mm, "end": v(0.66, 13.46) * mm});
            skLineSegment(sketch, "E915", {"start": v(0.66, 13.46) * mm, "end": v(-0.47, 13.32) * mm});
            skLineSegment(sketch, "E916", {"start": v(-0.47, 13.32) * mm, "end": v(-1.58, 13.17) * mm});
            skLineSegment(sketch, "E917", {"start": v(-1.58, 13.17) * mm, "end": v(-2.68, 13.02) * mm});
            skLineSegment(sketch, "E918", {"start": v(-2.68, 13.02) * mm, "end": v(-3.75, 12.85) * mm});
            skLineSegment(sketch, "E919", {"start": v(-3.75, 12.85) * mm, "end": v(-4.81, 12.69) * mm});
            skLineSegment(sketch, "E920", {"start": v(-4.81, 12.69) * mm, "end": v(-5.85, 12.51) * mm});
            skLineSegment(sketch, "E921", {"start": v(-5.85, 12.51) * mm, "end": v(-6.87, 12.34) * mm});
            skLineSegment(sketch, "E922", {"start": v(-6.87, 12.34) * mm, "end": v(-7.87, 12.15) * mm});
            skLineSegment(sketch, "E923", {"start": v(-7.87, 12.15) * mm, "end": v(-8.85, 11.96) * mm});
            skLineSegment(sketch, "E924", {"start": v(-8.85, 11.96) * mm, "end": v(-9.81, 11.77) * mm});
            skLineSegment(sketch, "E925", {"start": v(-9.81, 11.77) * mm, "end": v(-10.76, 11.56) * mm});
            skLineSegment(sketch, "E926", {"start": v(-10.76, 11.56) * mm, "end": v(-11.68, 11.36) * mm});
            skLineSegment(sketch, "E927", {"start": v(-11.68, 11.36) * mm, "end": v(-12.58, 11.15) * mm});
            skLineSegment(sketch, "E928", {"start": v(-12.58, 11.15) * mm, "end": v(-13.46, 10.93) * mm});
            skLineSegment(sketch, "E929", {"start": v(-13.46, 10.93) * mm, "end": v(-14.32, 10.7) * mm});
            skLineSegment(sketch, "E930", {"start": v(-14.32, 10.7) * mm, "end": v(-15.16, 10.48) * mm});
            skLineSegment(sketch, "E931", {"start": v(-15.16, 10.48) * mm, "end": v(-15.98, 10.25) * mm});
            skLineSegment(sketch, "E932", {"start": v(-15.98, 10.25) * mm, "end": v(-16.77, 10) * mm});
            skLineSegment(sketch, "E933", {"start": v(-16.77, 10) * mm, "end": v(-17.55, 9.77) * mm});
            skLineSegment(sketch, "E934", {"start": v(-17.55, 9.77) * mm, "end": v(-18.3, 9.52) * mm});
            skLineSegment(sketch, "E935", {"start": v(-18.3, 9.52) * mm, "end": v(-19.03, 9.27) * mm});
            skLineSegment(sketch, "E936", {"start": v(-19.03, 9.27) * mm, "end": v(-19.74, 9) * mm});
            skLineSegment(sketch, "E937", {"start": v(-19.74, 9) * mm, "end": v(-20.43, 8.75) * mm});
            skLineSegment(sketch, "E938", {"start": v(-20.43, 8.75) * mm, "end": v(-21.1, 8.48) * mm});
            skLineSegment(sketch, "E939", {"start": v(-21.1, 8.48) * mm, "end": v(-21.73, 8.21) * mm});
            skLineSegment(sketch, "E940", {"start": v(-21.73, 8.21) * mm, "end": v(-22.35, 7.94) * mm});
            skLineSegment(sketch, "E941", {"start": v(-22.35, 7.94) * mm, "end": v(-22.95, 7.66) * mm});
            skLineSegment(sketch, "E942", {"start": v(-22.95, 7.66) * mm, "end": v(-23.52, 7.38) * mm});
            skLineSegment(sketch, "E943", {"start": v(-23.52, 7.38) * mm, "end": v(-24.07, 7.1) * mm});
            skLineSegment(sketch, "E944", {"start": v(-24.07, 7.1) * mm, "end": v(-24.6, 6.8) * mm});
            skLineSegment(sketch, "E945", {"start": v(-24.6, 6.8) * mm, "end": v(-25.1, 6.51) * mm});
            skLineSegment(sketch, "E946", {"start": v(-25.1, 6.51) * mm, "end": v(-25.57, 6.22) * mm});
            skLineSegment(sketch, "E947", {"start": v(-25.57, 6.22) * mm, "end": v(-26.03, 5.92) * mm});
            skLineSegment(sketch, "E948", {"start": v(-26.03, 5.92) * mm, "end": v(-26.46, 5.61) * mm});
            skLineSegment(sketch, "E949", {"start": v(-26.46, 5.61) * mm, "end": v(-26.87, 5.3) * mm});
            skLineSegment(sketch, "E950", {"start": v(-26.87, 5.3) * mm, "end": v(-27.25, 5) * mm});
            skLineSegment(sketch, "E951", {"start": v(-27.25, 5) * mm, "end": v(-27.6, 4.69) * mm});
            skLineSegment(sketch, "E952", {"start": v(-27.6, 4.69) * mm, "end": v(-27.94, 4.37) * mm});
            skLineSegment(sketch, "E953", {"start": v(-27.94, 4.37) * mm, "end": v(-28.25, 4.05) * mm});
            skLineSegment(sketch, "E954", {"start": v(-28.25, 4.05) * mm, "end": v(-28.54, 3.73) * mm});
            skLineSegment(sketch, "E955", {"start": v(-28.54, 3.73) * mm, "end": v(-28.8, 3.4) * mm});
            skLineSegment(sketch, "E956", {"start": v(-28.8, 3.4) * mm, "end": v(-29.03, 3.08) * mm});
            skLineSegment(sketch, "E957", {"start": v(-29.03, 3.08) * mm, "end": v(-29.24, 2.75) * mm});
            skLineSegment(sketch, "E958", {"start": v(-29.24, 2.75) * mm, "end": v(-29.43, 2.41) * mm});
            skLineSegment(sketch, "E959", {"start": v(-29.43, 2.41) * mm, "end": v(-29.6, 2.08) * mm});
            skLineSegment(sketch, "E960", {"start": v(-29.6, 2.08) * mm, "end": v(-29.73, 1.74) * mm});
            skLineSegment(sketch, "E961", {"start": v(-29.73, 1.74) * mm, "end": v(-29.84, 1.4) * mm});
            skLineSegment(sketch, "E962", {"start": v(-29.84, 1.4) * mm, "end": v(-29.93, 1.06) * mm});
            skLineSegment(sketch, "E963", {"start": v(-29.93, 1.06) * mm, "end": v(-29.99, 0.7) * mm});
            skLineSegment(sketch, "E964", {"start": v(-29.99, 0.7) * mm, "end": v(-30.03, 0.36) * mm});
            skLineSegment(sketch, "E965", {"start": v(-30.03, 0.36) * mm, "end": v(-30.04, 0.01) * mm});
            skLineSegment(sketch, "E966", {"start": v(-30.04, 0.01) * mm, "end": v(-30.03, -0.34) * mm});
            skLineSegment(sketch, "E967", {"start": v(-30.03, -0.34) * mm, "end": v(-29.99, -0.69) * mm});
            skLineSegment(sketch, "E968", {"start": v(-29.99, -0.69) * mm, "end": v(-29.93, -1.03) * mm});
            skLineSegment(sketch, "E969", {"start": v(-29.93, -1.03) * mm, "end": v(-29.84, -1.38) * mm});
            skLineSegment(sketch, "E970", {"start": v(-29.84, -1.38) * mm, "end": v(-29.73, -1.72) * mm});
            skLineSegment(sketch, "E971", {"start": v(-29.73, -1.72) * mm, "end": v(-29.6, -2.05) * mm});
            skLineSegment(sketch, "E972", {"start": v(-29.6, -2.05) * mm, "end": v(-29.43, -2.4) * mm});
            skLineSegment(sketch, "E973", {"start": v(-29.43, -2.4) * mm, "end": v(-29.24, -2.72) * mm});
            skLineSegment(sketch, "E974", {"start": v(-29.24, -2.72) * mm, "end": v(-29.03, -3.05) * mm});
            skLineSegment(sketch, "E975", {"start": v(-29.03, -3.05) * mm, "end": v(-28.8, -3.38) * mm});
            skLineSegment(sketch, "E976", {"start": v(-28.8, -3.38) * mm, "end": v(-28.54, -3.7) * mm});
            skLineSegment(sketch, "E977", {"start": v(-28.54, -3.7) * mm, "end": v(-28.25, -4.03) * mm});
            skLineSegment(sketch, "E978", {"start": v(-28.25, -4.03) * mm, "end": v(-27.94, -4.35) * mm});
            skLineSegment(sketch, "E979", {"start": v(-27.94, -4.35) * mm, "end": v(-27.6, -4.66) * mm});
            skLineSegment(sketch, "E980", {"start": v(-27.6, -4.66) * mm, "end": v(-27.25, -4.98) * mm});
            skLineSegment(sketch, "E981", {"start": v(-27.25, -4.98) * mm, "end": v(-26.87, -5.29) * mm});
            skLineSegment(sketch, "E982", {"start": v(-26.87, -5.29) * mm, "end": v(-26.46, -5.6) * mm});
            skLineSegment(sketch, "E983", {"start": v(-26.46, -5.6) * mm, "end": v(-26.03, -5.9) * mm});
            skLineSegment(sketch, "E984", {"start": v(-26.03, -5.9) * mm, "end": v(-25.57, -6.2) * mm});
            skLineSegment(sketch, "E985", {"start": v(-25.57, -6.2) * mm, "end": v(-25.1, -6.5) * mm});
            skLineSegment(sketch, "E986", {"start": v(-25.1, -6.5) * mm, "end": v(-24.6, -6.78) * mm});
            skLineSegment(sketch, "E987", {"start": v(-24.6, -6.78) * mm, "end": v(-24.07, -7.07) * mm});
            skLineSegment(sketch, "E988", {"start": v(-24.07, -7.07) * mm, "end": v(-23.52, -7.36) * mm});
            skLineSegment(sketch, "E989", {"start": v(-23.52, -7.36) * mm, "end": v(-22.95, -7.64) * mm});
            skLineSegment(sketch, "E990", {"start": v(-22.95, -7.64) * mm, "end": v(-22.35, -7.92) * mm});
            skLineSegment(sketch, "E991", {"start": v(-22.35, -7.92) * mm, "end": v(-21.73, -8.2) * mm});
            skLineSegment(sketch, "E992", {"start": v(-21.73, -8.2) * mm, "end": v(-21.1, -8.46) * mm});
            skLineSegment(sketch, "E993", {"start": v(-21.1, -8.46) * mm, "end": v(-20.43, -8.73) * mm});
            skLineSegment(sketch, "E994", {"start": v(-20.43, -8.73) * mm, "end": v(-19.74, -8.99) * mm});
            skLineSegment(sketch, "E995", {"start": v(-19.74, -8.99) * mm, "end": v(-19.03, -9.24) * mm});
            skLineSegment(sketch, "E996", {"start": v(-19.03, -9.24) * mm, "end": v(-18.3, -9.5) * mm});
            skLineSegment(sketch, "E997", {"start": v(-18.3, -9.5) * mm, "end": v(-17.55, -9.74) * mm});
            skLineSegment(sketch, "E998", {"start": v(-17.55, -9.74) * mm, "end": v(-16.77, -9.99) * mm});
            skLineSegment(sketch, "E999", {"start": v(-16.77, -9.99) * mm, "end": v(-15.98, -10.22) * mm});
            skLineSegment(sketch, "E1000", {"start": v(-15.98, -10.22) * mm, "end": v(-15.16, -10.46) * mm});
            skLineSegment(sketch, "E1001", {"start": v(-15.16, -10.46) * mm, "end": v(-14.32, -10.68) * mm});
            skLineSegment(sketch, "E1002", {"start": v(-14.32, -10.68) * mm, "end": v(-13.46, -10.9) * mm});
            skLineSegment(sketch, "E1003", {"start": v(-13.46, -10.9) * mm, "end": v(-12.58, -11.12) * mm});
            skLineSegment(sketch, "E1004", {"start": v(-12.58, -11.12) * mm, "end": v(-11.68, -11.34) * mm});
            skLineSegment(sketch, "E1005", {"start": v(-11.68, -11.34) * mm, "end": v(-10.76, -11.54) * mm});
            skLineSegment(sketch, "E1006", {"start": v(-10.76, -11.54) * mm, "end": v(-9.81, -11.74) * mm});
            skLineSegment(sketch, "E1007", {"start": v(-9.81, -11.74) * mm, "end": v(-8.85, -11.94) * mm});
            skLineSegment(sketch, "E1008", {"start": v(-8.85, -11.94) * mm, "end": v(-7.87, -12.13) * mm});
            skLineSegment(sketch, "E1009", {"start": v(-7.87, -12.13) * mm, "end": v(-6.87, -12.31) * mm});
            skLineSegment(sketch, "E1010", {"start": v(-6.87, -12.31) * mm, "end": v(-5.85, -12.5) * mm});
            skLineSegment(sketch, "E1011", {"start": v(-5.85, -12.5) * mm, "end": v(-4.81, -12.66) * mm});
            skLineSegment(sketch, "E1012", {"start": v(-4.81, -12.66) * mm, "end": v(-3.75, -12.83) * mm});
            skLineSegment(sketch, "E1013", {"start": v(-3.75, -12.83) * mm, "end": v(-2.68, -13) * mm});
            skLineSegment(sketch, "E1014", {"start": v(-2.68, -13) * mm, "end": v(-1.58, -13.15) * mm});
            skLineSegment(sketch, "E1015", {"start": v(-1.58, -13.15) * mm, "end": v(-0.47, -13.3) * mm});
            skLineSegment(sketch, "E1016", {"start": v(-0.47, -13.3) * mm, "end": v(0.66, -13.44) * mm});
            skLineSegment(sketch, "E1017", {"start": v(0.66, -13.44) * mm, "end": v(1.8, -13.58) * mm});
            skLineSegment(sketch, "E1018", {"start": v(1.8, -13.58) * mm, "end": v(2.97, -13.7) * mm});
            skLineSegment(sketch, "E1019", {"start": v(2.97, -13.7) * mm, "end": v(4.15, -13.83) * mm});
            skLineSegment(sketch, "E1020", {"start": v(4.15, -13.83) * mm, "end": v(5.35, -13.95) * mm});
            skLineSegment(sketch, "E1021", {"start": v(5.35, -13.95) * mm, "end": v(6.56, -14.06) * mm});
            skLineSegment(sketch, "E1022", {"start": v(6.56, -14.06) * mm, "end": v(7.79, -14.16) * mm});
            skLineSegment(sketch, "E1023", {"start": v(7.79, -14.16) * mm, "end": v(9.03, -14.26) * mm});
            skLineSegment(sketch, "E1024", {"start": v(9.03, -14.26) * mm, "end": v(10.3, -14.36) * mm});
            skLineSegment(sketch, "E1025", {"start": v(10.3, -14.36) * mm, "end": v(11.57, -14.44) * mm});
            skLineSegment(sketch, "E1026", {"start": v(11.57, -14.44) * mm, "end": v(12.85, -14.52) * mm});
            skLineSegment(sketch, "E1027", {"start": v(12.85, -14.52) * mm, "end": v(14.16, -14.6) * mm});
            skLineSegment(sketch, "E1028", {"start": v(14.16, -14.6) * mm, "end": v(15.47, -14.66) * mm});
            skLineSegment(sketch, "E1029", {"start": v(15.47, -14.66) * mm, "end": v(16.8, -14.72) * mm});
            skLineSegment(sketch, "E1030", {"start": v(16.8, -14.72) * mm, "end": v(18.15, -14.78) * mm});
            skLineSegment(sketch, "E1031", {"start": v(18.15, -14.78) * mm, "end": v(19.5, -14.83) * mm});
            skLineSegment(sketch, "E1032", {"start": v(19.5, -14.83) * mm, "end": v(20.87, -14.87) * mm});
            skLineSegment(sketch, "E1033", {"start": v(20.87, -14.87) * mm, "end": v(22.26, -14.9) * mm});
            skLineSegment(sketch, "E1034", {"start": v(22.26, -14.9) * mm, "end": v(23.65, -14.93) * mm});
            skLineSegment(sketch, "E1035", {"start": v(23.65, -14.93) * mm, "end": v(25.05, -14.96) * mm});
            skLineSegment(sketch, "E1036", {"start": v(25.05, -14.96) * mm, "end": v(26.47, -14.98) * mm});
            skLineSegment(sketch, "E1037", {"start": v(26.47, -14.98) * mm, "end": v(27.9, -14.99) * mm});
            skLineSegment(sketch, "E1038", {"start": v(27.9, -14.99) * mm, "end": v(29.33, -15) * mm});
            skLineSegment(sketch, "E1039", {"start": v(29.33, -15) * mm, "end": v(30.78, -15) * mm});
            skLineSegment(sketch, "E1040", {"start": v(30.78, -15) * mm, "end": v(32.24, -14.99) * mm});
            skLineSegment(sketch, "E1041", {"start": v(32.24, -14.99) * mm, "end": v(33.7, -14.97) * mm});
            skLineSegment(sketch, "E1042", {"start": v(33.7, -14.97) * mm, "end": v(35.18, -14.96) * mm});
            skLineSegment(sketch, "E1043", {"start": v(35.18, -14.96) * mm, "end": v(36.67, -14.93) * mm});
            skLineSegment(sketch, "E1044", {"start": v(36.67, -14.93) * mm, "end": v(38.16, -14.9) * mm});
            skLineSegment(sketch, "E1045", {"start": v(38.16, -14.9) * mm, "end": v(39.66, -14.87) * mm});
            skLineSegment(sketch, "E1046", {"start": v(39.66, -14.87) * mm, "end": v(41.17, -14.83) * mm});
            skLineSegment(sketch, "E1047", {"start": v(41.17, -14.83) * mm, "end": v(42.68, -14.78) * mm});
            skLineSegment(sketch, "E1048", {"start": v(42.68, -14.78) * mm, "end": v(44.2, -14.73) * mm});
            skLineSegment(sketch, "E1049", {"start": v(44.2, -14.73) * mm, "end": v(45.73, -14.68) * mm});
            skLineSegment(sketch, "E1050", {"start": v(45.73, -14.68) * mm, "end": v(47.27, -14.61) * mm});
            skLineSegment(sketch, "E1051", {"start": v(47.27, -14.61) * mm, "end": v(48.8, -14.55) * mm});
            skLineSegment(sketch, "E1052", {"start": v(48.8, -14.55) * mm, "end": v(50.35, -14.48) * mm});
            skLineSegment(sketch, "E1053", {"start": v(50.35, -14.48) * mm, "end": v(51.9, -14.4) * mm});
            skLineSegment(sketch, "E1054", {"start": v(51.9, -14.4) * mm, "end": v(53.46, -14.32) * mm});
            skLineSegment(sketch, "E1055", {"start": v(53.46, -14.32) * mm, "end": v(55.02, -14.24) * mm});
            skLineSegment(sketch, "E1056", {"start": v(55.02, -14.24) * mm, "end": v(56.58, -14.15) * mm});
            skLineSegment(sketch, "E1057", {"start": v(56.58, -14.15) * mm, "end": v(58.15, -14.05) * mm});
            skLineSegment(sketch, "E1058", {"start": v(58.15, -14.05) * mm, "end": v(59.72, -13.96) * mm});
            skLineSegment(sketch, "E1059", {"start": v(59.72, -13.96) * mm, "end": v(61.29, -13.85) * mm});
            skLineSegment(sketch, "E1060", {"start": v(61.29, -13.85) * mm, "end": v(62.86, -13.75) * mm});
            skLineSegment(sketch, "E1061", {"start": v(62.86, -13.75) * mm, "end": v(64.44, -13.64) * mm});
            skLineSegment(sketch, "E1062", {"start": v(64.44, -13.64) * mm, "end": v(66.01, -13.52) * mm});
            skLineSegment(sketch, "E1063", {"start": v(66.01, -13.52) * mm, "end": v(67.6, -13.4) * mm});
            skLineSegment(sketch, "E1064", {"start": v(67.6, -13.4) * mm, "end": v(69.17, -13.29) * mm});
            skLineSegment(sketch, "E1065", {"start": v(69.17, -13.29) * mm, "end": v(70.75, -13.16) * mm});
            skLineSegment(sketch, "E1066", {"start": v(70.75, -13.16) * mm, "end": v(72.33, -13.03) * mm});
            skLineSegment(sketch, "E1067", {"start": v(72.33, -13.03) * mm, "end": v(73.9, -12.9) * mm});
            skLineSegment(sketch, "E1068", {"start": v(73.9, -12.9) * mm, "end": v(75.48, -12.77) * mm});
            skLineSegment(sketch, "E1069", {"start": v(75.48, -12.77) * mm, "end": v(77.06, -12.63) * mm});
            skLineSegment(sketch, "E1070", {"start": v(77.06, -12.63) * mm, "end": v(78.63, -12.5) * mm});
            skLineSegment(sketch, "E1071", {"start": v(78.63, -12.5) * mm, "end": v(80.2, -12.35) * mm});
            skLineSegment(sketch, "E1072", {"start": v(80.2, -12.35) * mm, "end": v(81.77, -12.2) * mm});
            skLineSegment(sketch, "E1073", {"start": v(81.77, -12.2) * mm, "end": v(83.34, -12.05) * mm});
            skLineSegment(sketch, "E1074", {"start": v(83.34, -12.05) * mm, "end": v(84.9, -11.9) * mm});
            skLineSegment(sketch, "E1075", {"start": v(84.9, -11.9) * mm, "end": v(86.46, -11.75) * mm});
            skLineSegment(sketch, "E1076", {"start": v(86.46, -11.75) * mm, "end": v(88.02, -11.6) * mm});
            skLineSegment(sketch, "E1077", {"start": v(88.02, -11.6) * mm, "end": v(89.57, -11.44) * mm});
            skLineSegment(sketch, "E1078", {"start": v(89.57, -11.44) * mm, "end": v(91.11, -11.28) * mm});
            skLineSegment(sketch, "E1079", {"start": v(91.11, -11.28) * mm, "end": v(92.65, -11.12) * mm});
            skLineSegment(sketch, "E1080", {"start": v(92.65, -11.12) * mm, "end": v(94.19, -10.95) * mm});
            skLineSegment(sketch, "E1081", {"start": v(94.19, -10.95) * mm, "end": v(95.72, -10.79) * mm});
            skLineSegment(sketch, "E1082", {"start": v(95.72, -10.79) * mm, "end": v(97.24, -10.62) * mm});
            skLineSegment(sketch, "E1083", {"start": v(97.24, -10.62) * mm, "end": v(98.75, -10.46) * mm});
            skLineSegment(sketch, "E1084", {"start": v(98.75, -10.46) * mm, "end": v(100.26, -10.29) * mm});
            skLineSegment(sketch, "E1085", {"start": v(100.26, -10.29) * mm, "end": v(101.76, -10.12) * mm});
            skLineSegment(sketch, "E1086", {"start": v(101.76, -10.12) * mm, "end": v(103.25, -9.94) * mm});
            skLineSegment(sketch, "E1087", {"start": v(103.25, -9.94) * mm, "end": v(104.74, -9.77) * mm});
            skLineSegment(sketch, "E1088", {"start": v(104.74, -9.77) * mm, "end": v(106.21, -9.6) * mm});
            skLineSegment(sketch, "E1089", {"start": v(106.21, -9.6) * mm, "end": v(107.68, -9.42) * mm});
            skLineSegment(sketch, "E1090", {"start": v(107.68, -9.42) * mm, "end": v(109.14, -9.25) * mm});
            skLineSegment(sketch, "E1091", {"start": v(109.14, -9.25) * mm, "end": v(110.59, -9.07) * mm});
            skLineSegment(sketch, "E1092", {"start": v(110.59, -9.07) * mm, "end": v(112.02, -8.9) * mm});
            skLineSegment(sketch, "E1093", {"start": v(112.02, -8.9) * mm, "end": v(113.45, -8.72) * mm});
            skLineSegment(sketch, "E1094", {"start": v(113.45, -8.72) * mm, "end": v(114.87, -8.54) * mm});
            skLineSegment(sketch, "E1095", {"start": v(114.87, -8.54) * mm, "end": v(116.27, -8.36) * mm});
            skLineSegment(sketch, "E1096", {"start": v(116.27, -8.36) * mm, "end": v(117.66, -8.19) * mm});
            skLineSegment(sketch, "E1097", {"start": v(117.66, -8.19) * mm, "end": v(119.05, -8) * mm});
            skLineSegment(sketch, "E1098", {"start": v(119.05, -8) * mm, "end": v(120.42, -7.83) * mm});
            skLineSegment(sketch, "E1099", {"start": v(120.42, -7.83) * mm, "end": v(121.77, -7.65) * mm});
            skLineSegment(sketch, "E1100", {"start": v(121.77, -7.65) * mm, "end": v(123.12, -7.47) * mm});
            skLineSegment(sketch, "E1101", {"start": v(123.12, -7.47) * mm, "end": v(124.45, -7.3) * mm});
            skLineSegment(sketch, "E1102", {"start": v(124.45, -7.3) * mm, "end": v(125.76, -7.12) * mm});
            skLineSegment(sketch, "E1103", {"start": v(125.76, -7.12) * mm, "end": v(127.07, -6.94) * mm});
            skLineSegment(sketch, "E1104", {"start": v(127.07, -6.94) * mm, "end": v(128.36, -6.77) * mm});
            skLineSegment(sketch, "E1105", {"start": v(128.36, -6.77) * mm, "end": v(129.63, -6.6) * mm});
            skLineSegment(sketch, "E1106", {"start": v(129.63, -6.6) * mm, "end": v(130.89, -6.42) * mm});
            skLineSegment(sketch, "E1107", {"start": v(130.89, -6.42) * mm, "end": v(132.13, -6.24) * mm});
            skLineSegment(sketch, "E1108", {"start": v(132.13, -6.24) * mm, "end": v(133.36, -6.07) * mm});
            skLineSegment(sketch, "E1109", {"start": v(133.36, -6.07) * mm, "end": v(134.57, -5.9) * mm});
            skLineSegment(sketch, "E1110", {"start": v(134.57, -5.9) * mm, "end": v(135.77, -5.73) * mm});
            skLineSegment(sketch, "E1111", {"start": v(135.77, -5.73) * mm, "end": v(136.95, -5.56) * mm});
            skLineSegment(sketch, "E1112", {"start": v(136.95, -5.56) * mm, "end": v(138.12, -5.39) * mm});
            skLineSegment(sketch, "E1113", {"start": v(138.12, -5.39) * mm, "end": v(139.26, -5.22) * mm});
            skLineSegment(sketch, "E1114", {"start": v(139.26, -5.22) * mm, "end": v(140.4, -5.06) * mm});
            skLineSegment(sketch, "E1115", {"start": v(140.4, -5.06) * mm, "end": v(141.5, -4.9) * mm});
            skLineSegment(sketch, "E1116", {"start": v(141.5, -4.9) * mm, "end": v(142.6, -4.73) * mm});
            skLineSegment(sketch, "E1117", {"start": v(142.6, -4.73) * mm, "end": v(143.67, -4.57) * mm});
            skLineSegment(sketch, "E1118", {"start": v(143.67, -4.57) * mm, "end": v(144.73, -4.4) * mm});
            skLineSegment(sketch, "E1119", {"start": v(144.73, -4.4) * mm, "end": v(145.77, -4.25) * mm});
            skLineSegment(sketch, "E1120", {"start": v(145.77, -4.25) * mm, "end": v(146.79, -4.1) * mm});
            skLineSegment(sketch, "E1121", {"start": v(146.79, -4.1) * mm, "end": v(147.8, -3.94) * mm});
            skLineSegment(sketch, "E1122", {"start": v(147.8, -3.94) * mm, "end": v(148.77, -3.8) * mm});
            skLineSegment(sketch, "E1123", {"start": v(148.77, -3.8) * mm, "end": v(149.73, -3.64) * mm});
            skLineSegment(sketch, "E1124", {"start": v(149.73, -3.64) * mm, "end": v(150.68, -3.5) * mm});
            skLineSegment(sketch, "E1125", {"start": v(150.68, -3.5) * mm, "end": v(151.6, -3.35) * mm});
            skLineSegment(sketch, "E1126", {"start": v(151.6, -3.35) * mm, "end": v(152.5, -3.2) * mm});
            skLineSegment(sketch, "E1127", {"start": v(152.5, -3.2) * mm, "end": v(153.38, -3.07) * mm});
            skLineSegment(sketch, "E1128", {"start": v(153.38, -3.07) * mm, "end": v(154.24, -2.93) * mm});
            skLineSegment(sketch, "E1129", {"start": v(154.24, -2.93) * mm, "end": v(155.08, -2.8) * mm});
            skLineSegment(sketch, "E1130", {"start": v(155.08, -2.8) * mm, "end": v(155.9, -2.67) * mm});
            skLineSegment(sketch, "E1131", {"start": v(155.9, -2.67) * mm, "end": v(156.7, -2.54) * mm});
            skLineSegment(sketch, "E1132", {"start": v(156.7, -2.54) * mm, "end": v(157.47, -2.41) * mm});
            skLineSegment(sketch, "E1133", {"start": v(157.47, -2.41) * mm, "end": v(158.22, -2.3) * mm});
            skLineSegment(sketch, "E1134", {"start": v(158.22, -2.3) * mm, "end": v(158.95, -2.17) * mm});
            skLineSegment(sketch, "E1135", {"start": v(158.95, -2.17) * mm, "end": v(159.66, -2.05) * mm});
            skLineSegment(sketch, "E1136", {"start": v(159.66, -2.05) * mm, "end": v(160.35, -1.94) * mm});
            skLineSegment(sketch, "E1137", {"start": v(160.35, -1.94) * mm, "end": v(161.01, -1.83) * mm});
            skLineSegment(sketch, "E1138", {"start": v(161.01, -1.83) * mm, "end": v(161.65, -1.72) * mm});
            skLineSegment(sketch, "E1139", {"start": v(161.65, -1.72) * mm, "end": v(162.27, -1.62) * mm});
            skLineSegment(sketch, "E1140", {"start": v(162.27, -1.62) * mm, "end": v(162.87, -1.52) * mm});
            skLineSegment(sketch, "E1141", {"start": v(162.87, -1.52) * mm, "end": v(163.44, -1.42) * mm});
            skLineSegment(sketch, "E1142", {"start": v(163.44, -1.42) * mm, "end": v(163.99, -1.33) * mm});
            skLineSegment(sketch, "E1143", {"start": v(163.99, -1.33) * mm, "end": v(164.52, -1.24) * mm});
            skLineSegment(sketch, "E1144", {"start": v(164.52, -1.24) * mm, "end": v(165.02, -1.16) * mm});
            skLineSegment(sketch, "E1145", {"start": v(165.02, -1.16) * mm, "end": v(165.5, -1.08) * mm});
            skLineSegment(sketch, "E1146", {"start": v(165.5, -1.08) * mm, "end": v(165.95, -1) * mm});
            skLineSegment(sketch, "E1147", {"start": v(165.95, -1) * mm, "end": v(166.38, -0.92) * mm});
            skLineSegment(sketch, "E1148", {"start": v(166.38, -0.92) * mm, "end": v(166.79, -0.85) * mm});
            skLineSegment(sketch, "E1149", {"start": v(166.79, -0.85) * mm, "end": v(167.17, -0.79) * mm});
            skLineSegment(sketch, "E1150", {"start": v(167.17, -0.79) * mm, "end": v(167.53, -0.73) * mm});
            skLineSegment(sketch, "E1151", {"start": v(167.53, -0.73) * mm, "end": v(167.86, -0.67) * mm});
            skLineSegment(sketch, "E1152", {"start": v(167.86, -0.67) * mm, "end": v(168.17, -0.62) * mm});
            skLineSegment(sketch, "E1153", {"start": v(168.17, -0.62) * mm, "end": v(168.46, -0.57) * mm});
            skLineSegment(sketch, "E1154", {"start": v(168.46, -0.57) * mm, "end": v(168.72, -0.52) * mm});
            skLineSegment(sketch, "E1155", {"start": v(168.72, -0.52) * mm, "end": v(168.95, -0.48) * mm});
            skLineSegment(sketch, "E1156", {"start": v(168.95, -0.48) * mm, "end": v(169.16, -0.44) * mm});
            skLineSegment(sketch, "E1157", {"start": v(169.16, -0.44) * mm, "end": v(169.35, -0.41) * mm});
            skLineSegment(sketch, "E1158", {"start": v(169.35, -0.41) * mm, "end": v(169.51, -0.38) * mm});
            skLineSegment(sketch, "E1159", {"start": v(169.51, -0.38) * mm, "end": v(169.65, -0.36) * mm});
            skLineSegment(sketch, "E1160", {"start": v(169.65, -0.36) * mm, "end": v(169.76, -0.34) * mm});
            skLineSegment(sketch, "E1161", {"start": v(169.76, -0.34) * mm, "end": v(169.85, -0.32) * mm});
            skLineSegment(sketch, "E1162", {"start": v(169.85, -0.32) * mm, "end": v(169.91, -0.31) * mm});
            skLineSegment(sketch, "E1163", {"start": v(169.91, -0.31) * mm, "end": v(169.95, -0.3) * mm});
            skLineSegment(sketch, "E1164", {"start": v(169.95, -0.3) * mm, "end": v(169.96, -0.3) * mm});
            skLineSegment(sketch, "E1165", {"start": v(169.96, -0.3) * mm, "end": v(169.96, 0.33) * mm});
            skLineSegment(sketch, "E1166", {"start": v(162.93, 0.01) * mm, "end": v(162.62, 0.06) * mm});
            skLineSegment(sketch, "E1167", {"start": v(162.62, 0.06) * mm, "end": v(162.02, 0.16) * mm});
            skLineSegment(sketch, "E1168", {"start": v(162.02, 0.16) * mm, "end": v(161.4, 0.27) * mm});
            skLineSegment(sketch, "E1169", {"start": v(161.4, 0.27) * mm, "end": v(160.77, 0.37) * mm});
            skLineSegment(sketch, "E1170", {"start": v(160.77, 0.37) * mm, "end": v(160.1, 0.48) * mm});
            skLineSegment(sketch, "E1171", {"start": v(160.1, 0.48) * mm, "end": v(159.42, 0.6) * mm});
            skLineSegment(sketch, "E1172", {"start": v(159.42, 0.6) * mm, "end": v(158.71, 0.71) * mm});
            skLineSegment(sketch, "E1173", {"start": v(158.71, 0.71) * mm, "end": v(157.98, 0.83) * mm});
            skLineSegment(sketch, "E1174", {"start": v(157.98, 0.83) * mm, "end": v(157.23, 0.96) * mm});
            skLineSegment(sketch, "E1175", {"start": v(157.23, 0.96) * mm, "end": v(156.45, 1.08) * mm});
            skLineSegment(sketch, "E1176", {"start": v(156.45, 1.08) * mm, "end": v(155.66, 1.2) * mm});
            skLineSegment(sketch, "E1177", {"start": v(155.66, 1.2) * mm, "end": v(154.84, 1.34) * mm});
            skLineSegment(sketch, "E1178", {"start": v(154.84, 1.34) * mm, "end": v(154, 1.47) * mm});
            skLineSegment(sketch, "E1179", {"start": v(154, 1.47) * mm, "end": v(153.15, 1.61) * mm});
            skLineSegment(sketch, "E1180", {"start": v(153.15, 1.61) * mm, "end": v(152.27, 1.75) * mm});
            skLineSegment(sketch, "E1181", {"start": v(152.27, 1.75) * mm, "end": v(151.37, 1.9) * mm});
            skLineSegment(sketch, "E1182", {"start": v(151.37, 1.9) * mm, "end": v(150.44, 2.04) * mm});
            skLineSegment(sketch, "E1183", {"start": v(150.44, 2.04) * mm, "end": v(149.5, 2.18) * mm});
            skLineSegment(sketch, "E1184", {"start": v(149.5, 2.18) * mm, "end": v(148.54, 2.33) * mm});
            skLineSegment(sketch, "E1185", {"start": v(148.54, 2.33) * mm, "end": v(147.56, 2.48) * mm});
            skLineSegment(sketch, "E1186", {"start": v(147.56, 2.48) * mm, "end": v(146.56, 2.64) * mm});
            skLineSegment(sketch, "E1187", {"start": v(146.56, 2.64) * mm, "end": v(145.54, 2.8) * mm});
            skLineSegment(sketch, "E1188", {"start": v(145.54, 2.8) * mm, "end": v(144.5, 2.95) * mm});
            skLineSegment(sketch, "E1189", {"start": v(144.5, 2.95) * mm, "end": v(143.45, 3.1) * mm});
            skLineSegment(sketch, "E1190", {"start": v(143.45, 3.1) * mm, "end": v(142.38, 3.27) * mm});
            skLineSegment(sketch, "E1191", {"start": v(142.38, 3.27) * mm, "end": v(141.28, 3.43) * mm});
            skLineSegment(sketch, "E1192", {"start": v(141.28, 3.43) * mm, "end": v(140.17, 3.6) * mm});
            skLineSegment(sketch, "E1193", {"start": v(140.17, 3.6) * mm, "end": v(139.04, 3.76) * mm});
            skLineSegment(sketch, "E1194", {"start": v(139.04, 3.76) * mm, "end": v(137.9, 3.93) * mm});
            skLineSegment(sketch, "E1195", {"start": v(137.9, 3.93) * mm, "end": v(136.74, 4.1) * mm});
            skLineSegment(sketch, "E1196", {"start": v(136.74, 4.1) * mm, "end": v(135.56, 4.27) * mm});
            skLineSegment(sketch, "E1197", {"start": v(135.56, 4.27) * mm, "end": v(134.36, 4.44) * mm});
            skLineSegment(sketch, "E1198", {"start": v(134.36, 4.44) * mm, "end": v(133.15, 4.6) * mm});
            skLineSegment(sketch, "E1199", {"start": v(133.15, 4.6) * mm, "end": v(131.92, 4.78) * mm});
            skLineSegment(sketch, "E1200", {"start": v(131.92, 4.78) * mm, "end": v(130.68, 4.95) * mm});
            skLineSegment(sketch, "E1201", {"start": v(130.68, 4.95) * mm, "end": v(129.42, 5.13) * mm});
            skLineSegment(sketch, "E1202", {"start": v(129.42, 5.13) * mm, "end": v(128.15, 5.3) * mm});
            skLineSegment(sketch, "E1203", {"start": v(128.15, 5.3) * mm, "end": v(126.86, 5.48) * mm});
            skLineSegment(sketch, "E1204", {"start": v(126.86, 5.48) * mm, "end": v(125.56, 5.66) * mm});
            skLineSegment(sketch, "E1205", {"start": v(125.56, 5.66) * mm, "end": v(124.25, 5.83) * mm});
            skLineSegment(sketch, "E1206", {"start": v(124.25, 5.83) * mm, "end": v(122.92, 6.01) * mm});
            skLineSegment(sketch, "E1207", {"start": v(122.92, 6.01) * mm, "end": v(121.58, 6.19) * mm});
            skLineSegment(sketch, "E1208", {"start": v(121.58, 6.19) * mm, "end": v(120.22, 6.37) * mm});
            skLineSegment(sketch, "E1209", {"start": v(120.22, 6.37) * mm, "end": v(118.85, 6.54) * mm});
            skLineSegment(sketch, "E1210", {"start": v(118.85, 6.54) * mm, "end": v(117.47, 6.72) * mm});
            skLineSegment(sketch, "E1211", {"start": v(117.47, 6.72) * mm, "end": v(116.08, 6.9) * mm});
            skLineSegment(sketch, "E1212", {"start": v(116.08, 6.9) * mm, "end": v(114.68, 7.08) * mm});
            skLineSegment(sketch, "E1213", {"start": v(114.68, 7.08) * mm, "end": v(113.26, 7.25) * mm});
            skLineSegment(sketch, "E1214", {"start": v(113.26, 7.25) * mm, "end": v(111.84, 7.43) * mm});
            skLineSegment(sketch, "E1215", {"start": v(111.84, 7.43) * mm, "end": v(110.4, 7.6) * mm});
            skLineSegment(sketch, "E1216", {"start": v(110.4, 7.6) * mm, "end": v(108.96, 7.78) * mm});
            skLineSegment(sketch, "E1217", {"start": v(108.96, 7.78) * mm, "end": v(107.5, 7.96) * mm});
            skLineSegment(sketch, "E1218", {"start": v(107.5, 7.96) * mm, "end": v(106.04, 8.13) * mm});
            skLineSegment(sketch, "E1219", {"start": v(106.04, 8.13) * mm, "end": v(104.56, 8.3) * mm});
            skLineSegment(sketch, "E1220", {"start": v(104.56, 8.3) * mm, "end": v(103.08, 8.48) * mm});
            skLineSegment(sketch, "E1221", {"start": v(103.08, 8.48) * mm, "end": v(101.6, 8.65) * mm});
            skLineSegment(sketch, "E1222", {"start": v(101.6, 8.65) * mm, "end": v(100.1, 8.82) * mm});
            skLineSegment(sketch, "E1223", {"start": v(100.1, 8.82) * mm, "end": v(98.59, 8.99) * mm});
            skLineSegment(sketch, "E1224", {"start": v(98.59, 8.99) * mm, "end": v(97.07, 9.15) * mm});
            skLineSegment(sketch, "E1225", {"start": v(97.07, 9.15) * mm, "end": v(95.55, 9.32) * mm});
            skLineSegment(sketch, "E1226", {"start": v(95.55, 9.32) * mm, "end": v(94.03, 9.49) * mm});
            skLineSegment(sketch, "E1227", {"start": v(94.03, 9.49) * mm, "end": v(92.5, 9.65) * mm});
            skLineSegment(sketch, "E1228", {"start": v(92.5, 9.65) * mm, "end": v(90.96, 9.8) * mm});
            skLineSegment(sketch, "E1229", {"start": v(90.96, 9.8) * mm, "end": v(89.41, 9.97) * mm});
            skLineSegment(sketch, "E1230", {"start": v(89.41, 9.97) * mm, "end": v(87.87, 10.13) * mm});
            skLineSegment(sketch, "E1231", {"start": v(87.87, 10.13) * mm, "end": v(86.31, 10.28) * mm});
            skLineSegment(sketch, "E1232", {"start": v(86.31, 10.28) * mm, "end": v(84.76, 10.43) * mm});
            skLineSegment(sketch, "E1233", {"start": v(84.76, 10.43) * mm, "end": v(83.2, 10.58) * mm});
            skLineSegment(sketch, "E1234", {"start": v(83.2, 10.58) * mm, "end": v(81.63, 10.73) * mm});
            skLineSegment(sketch, "E1235", {"start": v(81.63, 10.73) * mm, "end": v(80.07, 10.88) * mm});
            skLineSegment(sketch, "E1236", {"start": v(80.07, 10.88) * mm, "end": v(78.5, 11.02) * mm});
            skLineSegment(sketch, "E1237", {"start": v(78.5, 11.02) * mm, "end": v(76.93, 11.16) * mm});
            skLineSegment(sketch, "E1238", {"start": v(76.93, 11.16) * mm, "end": v(75.35, 11.3) * mm});
            skLineSegment(sketch, "E1239", {"start": v(75.35, 11.3) * mm, "end": v(73.78, 11.43) * mm});
            skLineSegment(sketch, "E1240", {"start": v(73.78, 11.43) * mm, "end": v(72.2, 11.56) * mm});
            skLineSegment(sketch, "E1241", {"start": v(72.2, 11.56) * mm, "end": v(70.63, 11.69) * mm});
            skLineSegment(sketch, "E1242", {"start": v(70.63, 11.69) * mm, "end": v(69.05, 11.81) * mm});
            skLineSegment(sketch, "E1243", {"start": v(69.05, 11.81) * mm, "end": v(67.48, 11.93) * mm});
            skLineSegment(sketch, "E1244", {"start": v(67.48, 11.93) * mm, "end": v(65.9, 12.05) * mm});
            skLineSegment(sketch, "E1245", {"start": v(65.9, 12.05) * mm, "end": v(64.33, 12.16) * mm});
            skLineSegment(sketch, "E1246", {"start": v(64.33, 12.16) * mm, "end": v(62.76, 12.27) * mm});
            skLineSegment(sketch, "E1247", {"start": v(62.76, 12.27) * mm, "end": v(61.19, 12.38) * mm});
            skLineSegment(sketch, "E1248", {"start": v(61.19, 12.38) * mm, "end": v(59.62, 12.48) * mm});
            skLineSegment(sketch, "E1249", {"start": v(59.62, 12.48) * mm, "end": v(58.06, 12.58) * mm});
            skLineSegment(sketch, "E1250", {"start": v(58.06, 12.58) * mm, "end": v(56.5, 12.67) * mm});
            skLineSegment(sketch, "E1251", {"start": v(56.5, 12.67) * mm, "end": v(54.94, 12.76) * mm});
            skLineSegment(sketch, "E1252", {"start": v(54.94, 12.76) * mm, "end": v(53.38, 12.85) * mm});
            skLineSegment(sketch, "E1253", {"start": v(53.38, 12.85) * mm, "end": v(51.83, 12.93) * mm});
            skLineSegment(sketch, "E1254", {"start": v(51.83, 12.93) * mm, "end": v(50.28, 13) * mm});
            skLineSegment(sketch, "E1255", {"start": v(50.28, 13) * mm, "end": v(48.74, 13.07) * mm});
            skLineSegment(sketch, "E1256", {"start": v(48.74, 13.07) * mm, "end": v(47.2, 13.14) * mm});
            skLineSegment(sketch, "E1257", {"start": v(47.2, 13.14) * mm, "end": v(45.68, 13.2) * mm});
            skLineSegment(sketch, "E1258", {"start": v(45.68, 13.2) * mm, "end": v(44.15, 13.26) * mm});
            skLineSegment(sketch, "E1259", {"start": v(44.15, 13.26) * mm, "end": v(42.64, 13.3) * mm});
            skLineSegment(sketch, "E1260", {"start": v(42.64, 13.3) * mm, "end": v(41.13, 13.35) * mm});
            skLineSegment(sketch, "E1261", {"start": v(41.13, 13.35) * mm, "end": v(39.62, 13.4) * mm});
            skLineSegment(sketch, "E1262", {"start": v(39.62, 13.4) * mm, "end": v(38.13, 13.43) * mm});
            skLineSegment(sketch, "E1263", {"start": v(38.13, 13.43) * mm, "end": v(36.64, 13.45) * mm});
            skLineSegment(sketch, "E1264", {"start": v(36.64, 13.45) * mm, "end": v(35.16, 13.48) * mm});
            skLineSegment(sketch, "E1265", {"start": v(35.16, 13.48) * mm, "end": v(33.7, 13.5) * mm});
            skLineSegment(sketch, "E1266", {"start": v(33.7, 13.5) * mm, "end": v(32.23, 13.5) * mm});
            skLineSegment(sketch, "E1267", {"start": v(32.23, 13.5) * mm, "end": v(30.78, 13.51) * mm});
            skLineSegment(sketch, "E1268", {"start": v(30.78, 13.51) * mm, "end": v(29.34, 13.52) * mm});
            skLineSegment(sketch, "E1269", {"start": v(29.34, 13.52) * mm, "end": v(27.9, 13.5) * mm});
            skLineSegment(sketch, "E1270", {"start": v(27.9, 13.5) * mm, "end": v(26.49, 13.5) * mm});
            skLineSegment(sketch, "E1271", {"start": v(26.49, 13.5) * mm, "end": v(25.08, 13.48) * mm});
            skLineSegment(sketch, "E1272", {"start": v(25.08, 13.48) * mm, "end": v(23.68, 13.46) * mm});
            skLineSegment(sketch, "E1273", {"start": v(23.68, 13.46) * mm, "end": v(22.3, 13.43) * mm});
            skLineSegment(sketch, "E1274", {"start": v(22.3, 13.43) * mm, "end": v(20.92, 13.4) * mm});
            skLineSegment(sketch, "E1275", {"start": v(20.92, 13.4) * mm, "end": v(19.55, 13.35) * mm});
            skLineSegment(sketch, "E1276", {"start": v(19.55, 13.35) * mm, "end": v(18.2, 13.3) * mm});
            skLineSegment(sketch, "E1277", {"start": v(18.2, 13.3) * mm, "end": v(16.87, 13.25) * mm});
            skLineSegment(sketch, "E1278", {"start": v(16.87, 13.25) * mm, "end": v(15.55, 13.19) * mm});
            skLineSegment(sketch, "E1279", {"start": v(15.55, 13.19) * mm, "end": v(14.24, 13.12) * mm});
            skLineSegment(sketch, "E1280", {"start": v(14.24, 13.12) * mm, "end": v(12.94, 13.05) * mm});
            skLineSegment(sketch, "E1281", {"start": v(12.94, 13.05) * mm, "end": v(11.66, 12.97) * mm});
            skLineSegment(sketch, "E1282", {"start": v(11.66, 12.97) * mm, "end": v(10.4, 12.88) * mm});
            skLineSegment(sketch, "E1283", {"start": v(10.4, 12.88) * mm, "end": v(9.15, 12.8) * mm});
            skLineSegment(sketch, "E1284", {"start": v(9.15, 12.8) * mm, "end": v(7.91, 12.7) * mm});
            skLineSegment(sketch, "E1285", {"start": v(7.91, 12.7) * mm, "end": v(6.7, 12.59) * mm});
            skLineSegment(sketch, "E1286", {"start": v(6.7, 12.59) * mm, "end": v(5.49, 12.48) * mm});
            skLineSegment(sketch, "E1287", {"start": v(5.49, 12.48) * mm, "end": v(4.3, 12.36) * mm});
            skLineSegment(sketch, "E1288", {"start": v(4.3, 12.36) * mm, "end": v(3.13, 12.24) * mm});
            skLineSegment(sketch, "E1289", {"start": v(3.13, 12.24) * mm, "end": v(1.98, 12.1) * mm});
            skLineSegment(sketch, "E1290", {"start": v(1.98, 12.1) * mm, "end": v(0.84, 11.97) * mm});
            skLineSegment(sketch, "E1291", {"start": v(0.84, 11.97) * mm, "end": v(-0.28, 11.83) * mm});
            skLineSegment(sketch, "E1292", {"start": v(-0.28, 11.83) * mm, "end": v(-1.38, 11.68) * mm});
            skLineSegment(sketch, "E1293", {"start": v(-1.38, 11.68) * mm, "end": v(-2.46, 11.53) * mm});
            skLineSegment(sketch, "E1294", {"start": v(-2.46, 11.53) * mm, "end": v(-3.52, 11.37) * mm});
            skLineSegment(sketch, "E1295", {"start": v(-3.52, 11.37) * mm, "end": v(-4.57, 11.2) * mm});
            skLineSegment(sketch, "E1296", {"start": v(-4.57, 11.2) * mm, "end": v(-5.6, 11.04) * mm});
            skLineSegment(sketch, "E1297", {"start": v(-5.6, 11.04) * mm, "end": v(-6.6, 10.86) * mm});
            skLineSegment(sketch, "E1298", {"start": v(-6.6, 10.86) * mm, "end": v(-7.6, 10.68) * mm});
            skLineSegment(sketch, "E1299", {"start": v(-7.6, 10.68) * mm, "end": v(-8.56, 10.5) * mm});
            skLineSegment(sketch, "E1300", {"start": v(-8.56, 10.5) * mm, "end": v(-9.5, 10.3) * mm});
            skLineSegment(sketch, "E1301", {"start": v(-9.5, 10.3) * mm, "end": v(-10.43, 10.1) * mm});
            skLineSegment(sketch, "E1302", {"start": v(-10.43, 10.1) * mm, "end": v(-11.34, 9.9) * mm});
            skLineSegment(sketch, "E1303", {"start": v(-11.34, 9.9) * mm, "end": v(-12.23, 9.69) * mm});
            skLineSegment(sketch, "E1304", {"start": v(-12.23, 9.69) * mm, "end": v(-13.1, 9.47) * mm});
            skLineSegment(sketch, "E1305", {"start": v(-13.1, 9.47) * mm, "end": v(-13.94, 9.26) * mm});
            skLineSegment(sketch, "E1306", {"start": v(-13.94, 9.26) * mm, "end": v(-14.76, 9.03) * mm});
            skLineSegment(sketch, "E1307", {"start": v(-14.76, 9.03) * mm, "end": v(-15.56, 8.8) * mm});
            skLineSegment(sketch, "E1308", {"start": v(-15.56, 8.8) * mm, "end": v(-16.34, 8.57) * mm});
            skLineSegment(sketch, "E1309", {"start": v(-16.34, 8.57) * mm, "end": v(-17.1, 8.34) * mm});
            skLineSegment(sketch, "E1310", {"start": v(-17.1, 8.34) * mm, "end": v(-17.82, 8.1) * mm});
            skLineSegment(sketch, "E1311", {"start": v(-17.82, 8.1) * mm, "end": v(-18.53, 7.85) * mm});
            skLineSegment(sketch, "E1312", {"start": v(-18.53, 7.85) * mm, "end": v(-19.22, 7.6) * mm});
            skLineSegment(sketch, "E1313", {"start": v(-19.22, 7.6) * mm, "end": v(-19.88, 7.35) * mm});
            skLineSegment(sketch, "E1314", {"start": v(-19.88, 7.35) * mm, "end": v(-20.52, 7.1) * mm});
            skLineSegment(sketch, "E1315", {"start": v(-20.52, 7.1) * mm, "end": v(-21.14, 6.84) * mm});
            skLineSegment(sketch, "E1316", {"start": v(-21.14, 6.84) * mm, "end": v(-21.73, 6.57) * mm});
            skLineSegment(sketch, "E1317", {"start": v(-21.73, 6.57) * mm, "end": v(-22.3, 6.31) * mm});
            skLineSegment(sketch, "E1318", {"start": v(-22.3, 6.31) * mm, "end": v(-22.84, 6.04) * mm});
            skLineSegment(sketch, "E1319", {"start": v(-22.84, 6.04) * mm, "end": v(-23.36, 5.77) * mm});
            skLineSegment(sketch, "E1320", {"start": v(-23.36, 5.77) * mm, "end": v(-23.86, 5.5) * mm});
            skLineSegment(sketch, "E1321", {"start": v(-23.86, 5.5) * mm, "end": v(-24.32, 5.23) * mm});
            skLineSegment(sketch, "E1322", {"start": v(-24.32, 5.23) * mm, "end": v(-24.77, 4.95) * mm});
            skLineSegment(sketch, "E1323", {"start": v(-24.77, 4.95) * mm, "end": v(-25.18, 4.68) * mm});
            skLineSegment(sketch, "E1324", {"start": v(-25.18, 4.68) * mm, "end": v(-25.58, 4.4) * mm});
            skLineSegment(sketch, "E1325", {"start": v(-25.58, 4.4) * mm, "end": v(-25.94, 4.13) * mm});
            skLineSegment(sketch, "E1326", {"start": v(-25.94, 4.13) * mm, "end": v(-26.28, 3.85) * mm});
            skLineSegment(sketch, "E1327", {"start": v(-26.28, 3.85) * mm, "end": v(-26.6, 3.58) * mm});
            skLineSegment(sketch, "E1328", {"start": v(-26.6, 3.58) * mm, "end": v(-26.89, 3.3) * mm});
            skLineSegment(sketch, "E1329", {"start": v(-26.89, 3.3) * mm, "end": v(-27.15, 3.03) * mm});
            skLineSegment(sketch, "E1330", {"start": v(-27.15, 3.03) * mm, "end": v(-27.39, 2.76) * mm});
            skLineSegment(sketch, "E1331", {"start": v(-27.39, 2.76) * mm, "end": v(-27.6, 2.5) * mm});
            skLineSegment(sketch, "E1332", {"start": v(-27.6, 2.5) * mm, "end": v(-27.8, 2.23) * mm});
            skLineSegment(sketch, "E1333", {"start": v(-27.8, 2.23) * mm, "end": v(-27.96, 1.97) * mm});
            skLineSegment(sketch, "E1334", {"start": v(-27.96, 1.97) * mm, "end": v(-28.1, 1.72) * mm});
            skLineSegment(sketch, "E1335", {"start": v(-28.1, 1.72) * mm, "end": v(-28.22, 1.47) * mm});
            skLineSegment(sketch, "E1336", {"start": v(-28.22, 1.47) * mm, "end": v(-28.32, 1.22) * mm});
            skLineSegment(sketch, "E1337", {"start": v(-28.32, 1.22) * mm, "end": v(-28.4, 0.98) * mm});
            skLineSegment(sketch, "E1338", {"start": v(-28.4, 0.98) * mm, "end": v(-28.46, 0.74) * mm});
            skLineSegment(sketch, "E1339", {"start": v(-28.46, 0.74) * mm, "end": v(-28.5, 0.5) * mm});
            skLineSegment(sketch, "E1340", {"start": v(-28.5, 0.5) * mm, "end": v(-28.53, 0.26) * mm});
            skLineSegment(sketch, "E1341", {"start": v(-28.53, 0.26) * mm, "end": v(-28.54, 0.01) * mm});
            skLineSegment(sketch, "E1342", {"start": v(-28.54, 0.01) * mm, "end": v(-28.53, -0.23) * mm});
            skLineSegment(sketch, "E1343", {"start": v(-28.53, -0.23) * mm, "end": v(-28.5, -0.47) * mm});
            skLineSegment(sketch, "E1344", {"start": v(-28.5, -0.47) * mm, "end": v(-28.46, -0.71) * mm});
            skLineSegment(sketch, "E1345", {"start": v(-28.46, -0.71) * mm, "end": v(-28.4, -0.96) * mm});
            skLineSegment(sketch, "E1346", {"start": v(-28.4, -0.96) * mm, "end": v(-28.32, -1.2) * mm});
            skLineSegment(sketch, "E1347", {"start": v(-28.32, -1.2) * mm, "end": v(-28.22, -1.45) * mm});
            skLineSegment(sketch, "E1348", {"start": v(-28.22, -1.45) * mm, "end": v(-28.1, -1.7) * mm});
            skLineSegment(sketch, "E1349", {"start": v(-28.1, -1.7) * mm, "end": v(-27.96, -1.95) * mm});
            skLineSegment(sketch, "E1350", {"start": v(-27.96, -1.95) * mm, "end": v(-27.8, -2.2) * mm});
            skLineSegment(sketch, "E1351", {"start": v(-27.8, -2.2) * mm, "end": v(-27.6, -2.47) * mm});
            skLineSegment(sketch, "E1352", {"start": v(-27.6, -2.47) * mm, "end": v(-27.39, -2.74) * mm});
            skLineSegment(sketch, "E1353", {"start": v(-27.39, -2.74) * mm, "end": v(-27.15, -3) * mm});
            skLineSegment(sketch, "E1354", {"start": v(-27.15, -3) * mm, "end": v(-26.89, -3.28) * mm});
            skLineSegment(sketch, "E1355", {"start": v(-26.89, -3.28) * mm, "end": v(-26.6, -3.55) * mm});
            skLineSegment(sketch, "E1356", {"start": v(-26.6, -3.55) * mm, "end": v(-26.28, -3.83) * mm});
            skLineSegment(sketch, "E1357", {"start": v(-26.28, -3.83) * mm, "end": v(-25.94, -4.1) * mm});
            skLineSegment(sketch, "E1358", {"start": v(-25.94, -4.1) * mm, "end": v(-25.58, -4.38) * mm});
            skLineSegment(sketch, "E1359", {"start": v(-25.58, -4.38) * mm, "end": v(-25.18, -4.66) * mm});
            skLineSegment(sketch, "E1360", {"start": v(-25.18, -4.66) * mm, "end": v(-24.77, -4.93) * mm});
            skLineSegment(sketch, "E1361", {"start": v(-24.77, -4.93) * mm, "end": v(-24.32, -5.2) * mm});
            skLineSegment(sketch, "E1362", {"start": v(-24.32, -5.2) * mm, "end": v(-23.86, -5.48) * mm});
            skLineSegment(sketch, "E1363", {"start": v(-23.86, -5.48) * mm, "end": v(-23.36, -5.75) * mm});
            skLineSegment(sketch, "E1364", {"start": v(-23.36, -5.75) * mm, "end": v(-22.84, -6.02) * mm});
            skLineSegment(sketch, "E1365", {"start": v(-22.84, -6.02) * mm, "end": v(-22.3, -6.29) * mm});
            skLineSegment(sketch, "E1366", {"start": v(-22.3, -6.29) * mm, "end": v(-21.73, -6.55) * mm});
            skLineSegment(sketch, "E1367", {"start": v(-21.73, -6.55) * mm, "end": v(-21.14, -6.81) * mm});
            skLineSegment(sketch, "E1368", {"start": v(-21.14, -6.81) * mm, "end": v(-20.52, -7.07) * mm});
            skLineSegment(sketch, "E1369", {"start": v(-20.52, -7.07) * mm, "end": v(-19.88, -7.33) * mm});
            skLineSegment(sketch, "E1370", {"start": v(-19.88, -7.33) * mm, "end": v(-19.22, -7.58) * mm});
            skLineSegment(sketch, "E1371", {"start": v(-19.22, -7.58) * mm, "end": v(-18.53, -7.83) * mm});
            skLineSegment(sketch, "E1372", {"start": v(-18.53, -7.83) * mm, "end": v(-17.82, -8.07) * mm});
            skLineSegment(sketch, "E1373", {"start": v(-17.82, -8.07) * mm, "end": v(-17.1, -8.31) * mm});
            skLineSegment(sketch, "E1374", {"start": v(-17.1, -8.31) * mm, "end": v(-16.34, -8.55) * mm});
            skLineSegment(sketch, "E1375", {"start": v(-16.34, -8.55) * mm, "end": v(-15.56, -8.78) * mm});
            skLineSegment(sketch, "E1376", {"start": v(-15.56, -8.78) * mm, "end": v(-14.76, -9.01) * mm});
            skLineSegment(sketch, "E1377", {"start": v(-14.76, -9.01) * mm, "end": v(-13.94, -9.23) * mm});
            skLineSegment(sketch, "E1378", {"start": v(-13.94, -9.23) * mm, "end": v(-13.1, -9.45) * mm});
            skLineSegment(sketch, "E1379", {"start": v(-13.1, -9.45) * mm, "end": v(-12.23, -9.66) * mm});
            skLineSegment(sketch, "E1380", {"start": v(-12.23, -9.66) * mm, "end": v(-11.34, -9.87) * mm});
            skLineSegment(sketch, "E1381", {"start": v(-11.34, -9.87) * mm, "end": v(-10.43, -10.08) * mm});
            skLineSegment(sketch, "E1382", {"start": v(-10.43, -10.08) * mm, "end": v(-9.5, -10.27) * mm});
            skLineSegment(sketch, "E1383", {"start": v(-9.5, -10.27) * mm, "end": v(-8.56, -10.47) * mm});
            skLineSegment(sketch, "E1384", {"start": v(-8.56, -10.47) * mm, "end": v(-7.6, -10.65) * mm});
            skLineSegment(sketch, "E1385", {"start": v(-7.6, -10.65) * mm, "end": v(-6.6, -10.84) * mm});
            skLineSegment(sketch, "E1386", {"start": v(-6.6, -10.84) * mm, "end": v(-5.6, -11.01) * mm});
            skLineSegment(sketch, "E1387", {"start": v(-5.6, -11.01) * mm, "end": v(-4.57, -11.18) * mm});
            skLineSegment(sketch, "E1388", {"start": v(-4.57, -11.18) * mm, "end": v(-3.52, -11.35) * mm});
            skLineSegment(sketch, "E1389", {"start": v(-3.52, -11.35) * mm, "end": v(-2.46, -11.5) * mm});
            skLineSegment(sketch, "E1390", {"start": v(-2.46, -11.5) * mm, "end": v(-1.38, -11.66) * mm});
            skLineSegment(sketch, "E1391", {"start": v(-1.38, -11.66) * mm, "end": v(-0.28, -11.8) * mm});
            skLineSegment(sketch, "E1392", {"start": v(-0.28, -11.8) * mm, "end": v(0.84, -11.95) * mm});
            skLineSegment(sketch, "E1393", {"start": v(0.84, -11.95) * mm, "end": v(1.98, -12.09) * mm});
            skLineSegment(sketch, "E1394", {"start": v(1.98, -12.09) * mm, "end": v(3.13, -12.21) * mm});
            skLineSegment(sketch, "E1395", {"start": v(3.13, -12.21) * mm, "end": v(4.3, -12.34) * mm});
            skLineSegment(sketch, "E1396", {"start": v(4.3, -12.34) * mm, "end": v(5.49, -12.45) * mm});
            skLineSegment(sketch, "E1397", {"start": v(5.49, -12.45) * mm, "end": v(6.7, -12.57) * mm});
            skLineSegment(sketch, "E1398", {"start": v(6.7, -12.57) * mm, "end": v(7.91, -12.67) * mm});
            skLineSegment(sketch, "E1399", {"start": v(7.91, -12.67) * mm, "end": v(9.15, -12.77) * mm});
            skLineSegment(sketch, "E1400", {"start": v(9.15, -12.77) * mm, "end": v(10.4, -12.86) * mm});
            skLineSegment(sketch, "E1401", {"start": v(10.4, -12.86) * mm, "end": v(11.66, -12.95) * mm});
            skLineSegment(sketch, "E1402", {"start": v(11.66, -12.95) * mm, "end": v(12.94, -13.02) * mm});
            skLineSegment(sketch, "E1403", {"start": v(12.94, -13.02) * mm, "end": v(14.24, -13.1) * mm});
            skLineSegment(sketch, "E1404", {"start": v(14.24, -13.1) * mm, "end": v(15.55, -13.16) * mm});
            skLineSegment(sketch, "E1405", {"start": v(15.55, -13.16) * mm, "end": v(16.87, -13.23) * mm});
            skLineSegment(sketch, "E1406", {"start": v(16.87, -13.23) * mm, "end": v(18.2, -13.28) * mm});
            skLineSegment(sketch, "E1407", {"start": v(18.2, -13.28) * mm, "end": v(19.55, -13.33) * mm});
            skLineSegment(sketch, "E1408", {"start": v(19.55, -13.33) * mm, "end": v(20.92, -13.37) * mm});
            skLineSegment(sketch, "E1409", {"start": v(20.92, -13.37) * mm, "end": v(22.3, -13.4) * mm});
            skLineSegment(sketch, "E1410", {"start": v(22.3, -13.4) * mm, "end": v(23.68, -13.43) * mm});
            skLineSegment(sketch, "E1411", {"start": v(23.68, -13.43) * mm, "end": v(25.08, -13.46) * mm});
            skLineSegment(sketch, "E1412", {"start": v(25.08, -13.46) * mm, "end": v(26.49, -13.48) * mm});
            skLineSegment(sketch, "E1413", {"start": v(26.49, -13.48) * mm, "end": v(27.9, -13.49) * mm});
            skLineSegment(sketch, "E1414", {"start": v(27.9, -13.49) * mm, "end": v(29.34, -13.5) * mm});
            skLineSegment(sketch, "E1415", {"start": v(29.34, -13.5) * mm, "end": v(30.78, -13.5) * mm});
            skLineSegment(sketch, "E1416", {"start": v(30.78, -13.5) * mm, "end": v(32.23, -13.49) * mm});
            skLineSegment(sketch, "E1417", {"start": v(32.23, -13.49) * mm, "end": v(33.7, -13.47) * mm});
            skLineSegment(sketch, "E1418", {"start": v(33.7, -13.47) * mm, "end": v(35.16, -13.46) * mm});
            skLineSegment(sketch, "E1419", {"start": v(35.16, -13.46) * mm, "end": v(36.64, -13.43) * mm});
            skLineSegment(sketch, "E1420", {"start": v(36.64, -13.43) * mm, "end": v(38.13, -13.4) * mm});
            skLineSegment(sketch, "E1421", {"start": v(38.13, -13.4) * mm, "end": v(39.62, -13.37) * mm});
            skLineSegment(sketch, "E1422", {"start": v(39.62, -13.37) * mm, "end": v(41.13, -13.33) * mm});
            skLineSegment(sketch, "E1423", {"start": v(41.13, -13.33) * mm, "end": v(42.64, -13.28) * mm});
            skLineSegment(sketch, "E1424", {"start": v(42.64, -13.28) * mm, "end": v(44.15, -13.23) * mm});
            skLineSegment(sketch, "E1425", {"start": v(44.15, -13.23) * mm, "end": v(45.68, -13.18) * mm});
            skLineSegment(sketch, "E1426", {"start": v(45.68, -13.18) * mm, "end": v(47.2, -13.12) * mm});
            skLineSegment(sketch, "E1427", {"start": v(47.2, -13.12) * mm, "end": v(48.74, -13.05) * mm});
            skLineSegment(sketch, "E1428", {"start": v(48.74, -13.05) * mm, "end": v(50.28, -12.98) * mm});
            skLineSegment(sketch, "E1429", {"start": v(50.28, -12.98) * mm, "end": v(51.83, -12.9) * mm});
            skLineSegment(sketch, "E1430", {"start": v(51.83, -12.9) * mm, "end": v(53.38, -12.82) * mm});
            skLineSegment(sketch, "E1431", {"start": v(53.38, -12.82) * mm, "end": v(54.94, -12.74) * mm});
            skLineSegment(sketch, "E1432", {"start": v(54.94, -12.74) * mm, "end": v(56.5, -12.65) * mm});
            skLineSegment(sketch, "E1433", {"start": v(56.5, -12.65) * mm, "end": v(58.06, -12.56) * mm});
            skLineSegment(sketch, "E1434", {"start": v(58.06, -12.56) * mm, "end": v(59.62, -12.46) * mm});
            skLineSegment(sketch, "E1435", {"start": v(59.62, -12.46) * mm, "end": v(61.19, -12.36) * mm});
            skLineSegment(sketch, "E1436", {"start": v(61.19, -12.36) * mm, "end": v(62.76, -12.25) * mm});
            skLineSegment(sketch, "E1437", {"start": v(62.76, -12.25) * mm, "end": v(64.33, -12.14) * mm});
            skLineSegment(sketch, "E1438", {"start": v(64.33, -12.14) * mm, "end": v(65.9, -12.03) * mm});
            skLineSegment(sketch, "E1439", {"start": v(65.9, -12.03) * mm, "end": v(67.48, -11.91) * mm});
            skLineSegment(sketch, "E1440", {"start": v(67.48, -11.91) * mm, "end": v(69.05, -11.8) * mm});
            skLineSegment(sketch, "E1441", {"start": v(69.05, -11.8) * mm, "end": v(70.63, -11.67) * mm});
            skLineSegment(sketch, "E1442", {"start": v(70.63, -11.67) * mm, "end": v(72.2, -11.54) * mm});
            skLineSegment(sketch, "E1443", {"start": v(72.2, -11.54) * mm, "end": v(73.78, -11.4) * mm});
            skLineSegment(sketch, "E1444", {"start": v(73.78, -11.4) * mm, "end": v(75.35, -11.27) * mm});
            skLineSegment(sketch, "E1445", {"start": v(75.35, -11.27) * mm, "end": v(76.93, -11.14) * mm});
            skLineSegment(sketch, "E1446", {"start": v(76.93, -11.14) * mm, "end": v(78.5, -11) * mm});
            skLineSegment(sketch, "E1447", {"start": v(78.5, -11) * mm, "end": v(80.07, -10.85) * mm});
            skLineSegment(sketch, "E1448", {"start": v(80.07, -10.85) * mm, "end": v(81.63, -10.7) * mm});
            skLineSegment(sketch, "E1449", {"start": v(81.63, -10.7) * mm, "end": v(83.2, -10.56) * mm});
            skLineSegment(sketch, "E1450", {"start": v(83.2, -10.56) * mm, "end": v(84.76, -10.41) * mm});
            skLineSegment(sketch, "E1451", {"start": v(84.76, -10.41) * mm, "end": v(86.31, -10.26) * mm});
            skLineSegment(sketch, "E1452", {"start": v(86.31, -10.26) * mm, "end": v(87.87, -10.1) * mm});
            skLineSegment(sketch, "E1453", {"start": v(87.87, -10.1) * mm, "end": v(89.41, -9.95) * mm});
            skLineSegment(sketch, "E1454", {"start": v(89.41, -9.95) * mm, "end": v(90.96, -9.79) * mm});
            skLineSegment(sketch, "E1455", {"start": v(90.96, -9.79) * mm, "end": v(92.5, -9.63) * mm});
            skLineSegment(sketch, "E1456", {"start": v(92.5, -9.63) * mm, "end": v(94.03, -9.46) * mm});
            skLineSegment(sketch, "E1457", {"start": v(94.03, -9.46) * mm, "end": v(95.55, -9.3) * mm});
            skLineSegment(sketch, "E1458", {"start": v(95.55, -9.3) * mm, "end": v(97.07, -9.13) * mm});
            skLineSegment(sketch, "E1459", {"start": v(97.07, -9.13) * mm, "end": v(98.59, -8.96) * mm});
            skLineSegment(sketch, "E1460", {"start": v(98.59, -8.96) * mm, "end": v(100.1, -8.8) * mm});
            skLineSegment(sketch, "E1461", {"start": v(100.1, -8.8) * mm, "end": v(101.6, -8.63) * mm});
            skLineSegment(sketch, "E1462", {"start": v(101.6, -8.63) * mm, "end": v(103.08, -8.45) * mm});
            skLineSegment(sketch, "E1463", {"start": v(103.08, -8.45) * mm, "end": v(104.56, -8.28) * mm});
            skLineSegment(sketch, "E1464", {"start": v(104.56, -8.28) * mm, "end": v(106.04, -8.1) * mm});
            skLineSegment(sketch, "E1465", {"start": v(106.04, -8.1) * mm, "end": v(107.5, -7.93) * mm});
            skLineSegment(sketch, "E1466", {"start": v(107.5, -7.93) * mm, "end": v(108.96, -7.76) * mm});
            skLineSegment(sketch, "E1467", {"start": v(108.96, -7.76) * mm, "end": v(110.4, -7.58) * mm});
            skLineSegment(sketch, "E1468", {"start": v(110.4, -7.58) * mm, "end": v(111.84, -7.4) * mm});
            skLineSegment(sketch, "E1469", {"start": v(111.84, -7.4) * mm, "end": v(113.26, -7.23) * mm});
            skLineSegment(sketch, "E1470", {"start": v(113.26, -7.23) * mm, "end": v(114.68, -7.05) * mm});
            skLineSegment(sketch, "E1471", {"start": v(114.68, -7.05) * mm, "end": v(116.08, -6.88) * mm});
            skLineSegment(sketch, "E1472", {"start": v(116.08, -6.88) * mm, "end": v(117.47, -6.7) * mm});
            skLineSegment(sketch, "E1473", {"start": v(117.47, -6.7) * mm, "end": v(118.85, -6.52) * mm});
            skLineSegment(sketch, "E1474", {"start": v(118.85, -6.52) * mm, "end": v(120.22, -6.34) * mm});
            skLineSegment(sketch, "E1475", {"start": v(120.22, -6.34) * mm, "end": v(121.58, -6.17) * mm});
            skLineSegment(sketch, "E1476", {"start": v(121.58, -6.17) * mm, "end": v(122.92, -5.99) * mm});
            skLineSegment(sketch, "E1477", {"start": v(122.92, -5.99) * mm, "end": v(124.25, -5.81) * mm});
            skLineSegment(sketch, "E1478", {"start": v(124.25, -5.81) * mm, "end": v(125.56, -5.63) * mm});
            skLineSegment(sketch, "E1479", {"start": v(125.56, -5.63) * mm, "end": v(126.86, -5.46) * mm});
            skLineSegment(sketch, "E1480", {"start": v(126.86, -5.46) * mm, "end": v(128.15, -5.28) * mm});
            skLineSegment(sketch, "E1481", {"start": v(128.15, -5.28) * mm, "end": v(129.42, -5.1) * mm});
            skLineSegment(sketch, "E1482", {"start": v(129.42, -5.1) * mm, "end": v(130.68, -4.93) * mm});
            skLineSegment(sketch, "E1483", {"start": v(130.68, -4.93) * mm, "end": v(131.92, -4.76) * mm});
            skLineSegment(sketch, "E1484", {"start": v(131.92, -4.76) * mm, "end": v(133.15, -4.59) * mm});
            skLineSegment(sketch, "E1485", {"start": v(133.15, -4.59) * mm, "end": v(134.36, -4.41) * mm});
            skLineSegment(sketch, "E1486", {"start": v(134.36, -4.41) * mm, "end": v(135.56, -4.24) * mm});
            skLineSegment(sketch, "E1487", {"start": v(135.56, -4.24) * mm, "end": v(136.74, -4.07) * mm});
            skLineSegment(sketch, "E1488", {"start": v(136.74, -4.07) * mm, "end": v(137.9, -3.9) * mm});
            skLineSegment(sketch, "E1489", {"start": v(137.9, -3.9) * mm, "end": v(139.04, -3.74) * mm});
            skLineSegment(sketch, "E1490", {"start": v(139.04, -3.74) * mm, "end": v(140.17, -3.57) * mm});
            skLineSegment(sketch, "E1491", {"start": v(140.17, -3.57) * mm, "end": v(141.28, -3.4) * mm});
            skLineSegment(sketch, "E1492", {"start": v(141.28, -3.4) * mm, "end": v(142.38, -3.25) * mm});
            skLineSegment(sketch, "E1493", {"start": v(142.38, -3.25) * mm, "end": v(143.45, -3.09) * mm});
            skLineSegment(sketch, "E1494", {"start": v(143.45, -3.09) * mm, "end": v(144.5, -2.93) * mm});
            skLineSegment(sketch, "E1495", {"start": v(144.5, -2.93) * mm, "end": v(145.54, -2.77) * mm});
            skLineSegment(sketch, "E1496", {"start": v(145.54, -2.77) * mm, "end": v(146.56, -2.61) * mm});
            skLineSegment(sketch, "E1497", {"start": v(146.56, -2.61) * mm, "end": v(147.56, -2.46) * mm});
            skLineSegment(sketch, "E1498", {"start": v(147.56, -2.46) * mm, "end": v(148.54, -2.3) * mm});
            skLineSegment(sketch, "E1499", {"start": v(148.54, -2.3) * mm, "end": v(149.5, -2.16) * mm});
            skLineSegment(sketch, "E1500", {"start": v(149.5, -2.16) * mm, "end": v(150.44, -2.01) * mm});
            skLineSegment(sketch, "E1501", {"start": v(150.44, -2.01) * mm, "end": v(151.37, -1.87) * mm});
            skLineSegment(sketch, "E1502", {"start": v(151.37, -1.87) * mm, "end": v(152.27, -1.73) * mm});
            skLineSegment(sketch, "E1503", {"start": v(152.27, -1.73) * mm, "end": v(153.15, -1.59) * mm});
            skLineSegment(sketch, "E1504", {"start": v(153.15, -1.59) * mm, "end": v(154, -1.45) * mm});
            skLineSegment(sketch, "E1505", {"start": v(154, -1.45) * mm, "end": v(154.84, -1.32) * mm});
            skLineSegment(sketch, "E1506", {"start": v(154.84, -1.32) * mm, "end": v(155.66, -1.19) * mm});
            skLineSegment(sketch, "E1507", {"start": v(155.66, -1.19) * mm, "end": v(156.45, -1.06) * mm});
            skLineSegment(sketch, "E1508", {"start": v(156.45, -1.06) * mm, "end": v(157.23, -0.93) * mm});
            skLineSegment(sketch, "E1509", {"start": v(157.23, -0.93) * mm, "end": v(157.98, -0.81) * mm});
            skLineSegment(sketch, "E1510", {"start": v(157.98, -0.81) * mm, "end": v(158.71, -0.7) * mm});
            skLineSegment(sketch, "E1511", {"start": v(158.71, -0.7) * mm, "end": v(159.42, -0.57) * mm});
            skLineSegment(sketch, "E1512", {"start": v(159.42, -0.57) * mm, "end": v(160.1, -0.46) * mm});
            skLineSegment(sketch, "E1513", {"start": v(160.1, -0.46) * mm, "end": v(160.77, -0.35) * mm});
            skLineSegment(sketch, "E1514", {"start": v(160.77, -0.35) * mm, "end": v(161.4, -0.24) * mm});
            skLineSegment(sketch, "E1515", {"start": v(161.4, -0.24) * mm, "end": v(162.02, -0.14) * mm});
            skLineSegment(sketch, "E1516", {"start": v(162.02, -0.14) * mm, "end": v(162.62, -0.04) * mm});
            skLineSegment(sketch, "E1517", {"start": v(162.62, -0.04) * mm, "end": v(162.93, 0.01) * mm});
            skSolve(sketch);
        }
        {
            var Q0;
            Q0=makeQuery(id+"F2.imprint","IMPRINT",FACE,{"disambiguationData":[TD([[makeQuery(id+"F2.imprint","IMPRINT",EDGE,{"derivedFrom":sQuery(id+"F2.wireOp",EDGE,"E1166")}),1.0]])]});
            var Q1;
            Q1=makeQuery(id+"F1.imprint","IMPRINT",FACE,{"disambiguationData":[TD([[makeQuery(id+"F1.imprint","IMPRINT",EDGE,{"derivedFrom":sQuery(id+"F1.wireOp",EDGE,"E400")}),1.0]])]});
            loft(context, id + "F3", {"sheetProfilesArray" : [{ "sheetProfileEntities" : qUnion([Q0]) }, { "sheetProfileEntities" : qUnion([Q1]) }]});
        }
    });
